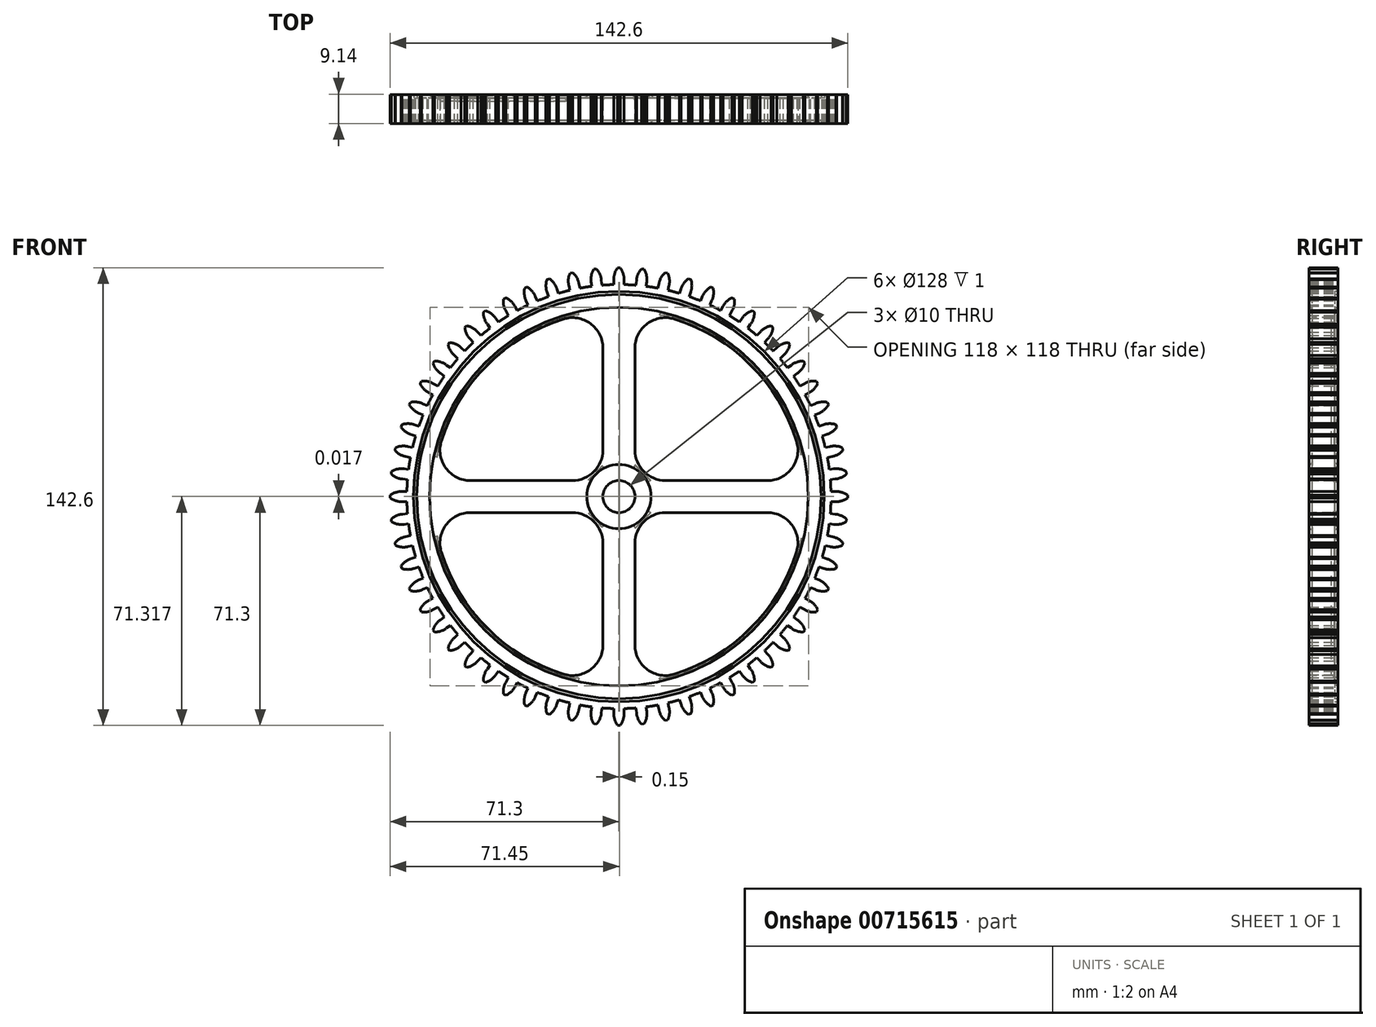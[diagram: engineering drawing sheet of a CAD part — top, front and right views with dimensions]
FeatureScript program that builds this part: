
annotation { "Feature Type Name" : "Feature", "Feature Type Description" : "" }
export const myFeature = defineFeature(function(context is Context, id is Id, definition is map)
    precondition{}
    {
        {
            var Q0;
            Q0=qCreatedBy(makeId("Front.planeOp"),FACE);
            var sketch = newSketch(context, id + "F0", { "sketchPlane" : qUnion([Q0])});
            skCircle(sketch, "E0", {"center": v(0, 0) * mm, "radius": 5 * mm});
            skCircle(sketch, "E1", {"center": v(0, 0) * mm, "radius": 66.1 * mm});
            skLineSegment(sketch, "E2", {"start": v(0, -77.77) * mm, "end": v(0, 74.62) * mm, "construction": true});
            skLineSegment(sketch, "E3", {"start": v(1.6, 66.08) * mm, "end": v(1.6, 67.83) * mm});
            skLineSegment(sketch, "E4", {"start": v(-1.6, 67.83) * mm, "end": v(-1.6, 66.08) * mm});
            skArc(sketch, "E5", {"start": v(-0.4, 71.3) * mm, "mid": v(-1.31, 69.54) * mm, "end": v(-1.6, 67.58) * mm});
            skArc(sketch, "E6.trimOffspring", {"start": v(1.6, 67.58) * mm, "mid": v(1.31, 69.54) * mm, "end": v(0.4, 71.3) * mm});
            skLineSegment(sketch, "E7", {"start": v(-0.4, 71.3) * mm, "end": v(0.4, 71.3) * mm});
            skLineSegment(sketch, "E8.1.0", {"start": v(-7.86, 70.87) * mm, "end": v(-7.05, 70.95) * mm});
            skArc(sketch, "E8.1.1", {"start": v(-5.47, 67.38) * mm, "mid": v(-5.96, 69.3) * mm, "end": v(-7.05, 70.95) * mm});
            skArc(sketch, "E8.1.2", {"start": v(-7.86, 70.87) * mm, "mid": v(-8.58, 69.02) * mm, "end": v(-8.66, 67.05) * mm});
            skLineSegment(sketch, "E8.1.3", {"start": v(-8.68, 67.3) * mm, "end": v(-8.5, 65.55) * mm});
            skLineSegment(sketch, "E8.1.4", {"start": v(-5.32, 65.89) * mm, "end": v(-5.5, 67.63) * mm});
            skLineSegment(sketch, "E8.2.0", {"start": v(-15.22, 69.66) * mm, "end": v(-14.43, 69.83) * mm});
            skArc(sketch, "E8.2.1", {"start": v(-12.49, 66.44) * mm, "mid": v(-13.17, 68.3) * mm, "end": v(-14.43, 69.83) * mm});
            skArc(sketch, "E8.2.2", {"start": v(-15.22, 69.66) * mm, "mid": v(-15.74, 67.75) * mm, "end": v(-15.62, 65.77) * mm});
            skLineSegment(sketch, "E8.2.3", {"start": v(-15.67, 66.02) * mm, "end": v(-15.3, 64.3) * mm});
            skLineSegment(sketch, "E8.2.4", {"start": v(-12.17, 64.97) * mm, "end": v(-12.54, 66.68) * mm});
            skLineSegment(sketch, "E9.1.3.0", {"start": v(-22.42, 67.68) * mm, "end": v(-21.64, 67.94) * mm});
            skArc(sketch, "E9.3.3.0", {"start": v(-19.36, 64.77) * mm, "mid": v(-20.24, 66.54) * mm, "end": v(-21.64, 67.94) * mm});
            skArc(sketch, "E9.7.3.0", {"start": v(-22.42, 67.68) * mm, "mid": v(-22.74, 65.73) * mm, "end": v(-22.4, 63.78) * mm});
            skLineSegment(sketch, "E9.11.3.0", {"start": v(-22.48, 64.02) * mm, "end": v(-21.94, 62.35) * mm});
            skLineSegment(sketch, "E9.14.3.0", {"start": v(-18.9, 63.34) * mm, "end": v(-19.44, 65) * mm});
            skLineSegment(sketch, "E9.1.4.0", {"start": v(-29.37, 64.97) * mm, "end": v(-28.63, 65.3) * mm});
            skArc(sketch, "E9.3.4.0", {"start": v(-26.03, 62.4) * mm, "mid": v(-27.08, 64.06) * mm, "end": v(-28.63, 65.3) * mm});
            skArc(sketch, "E9.7.4.0", {"start": v(-29.37, 64.97) * mm, "mid": v(-29.49, 63) * mm, "end": v(-28.95, 61.09) * mm});
            skLineSegment(sketch, "E9.11.4.0", {"start": v(-29.05, 61.32) * mm, "end": v(-28.34, 59.72) * mm});
            skLineSegment(sketch, "E9.14.4.0", {"start": v(-25.42, 61.02) * mm, "end": v(-26.13, 62.62) * mm});
            skLineSegment(sketch, "E9.1.5.0", {"start": v(-36, 61.54) * mm, "end": v(-35.3, 61.95) * mm});
            skArc(sketch, "E9.3.5.0", {"start": v(-32.4, 59.33) * mm, "mid": v(-33.63, 60.88) * mm, "end": v(-35.3, 61.95) * mm});
            skArc(sketch, "E9.7.5.0", {"start": v(-36, 61.54) * mm, "mid": v(-35.9, 59.57) * mm, "end": v(-35.18, 57.73) * mm});
            skLineSegment(sketch, "E9.11.5.0", {"start": v(-35.3, 57.94) * mm, "end": v(-34.43, 56.43) * mm});
            skLineSegment(sketch, "E9.14.5.0", {"start": v(-31.65, 58.03) * mm, "end": v(-32.53, 59.54) * mm});
            skLineSegment(sketch, "E9.1.6.0", {"start": v(-42.24, 57.44) * mm, "end": v(-41.58, 57.92) * mm});
            skArc(sketch, "E9.3.6.0", {"start": v(-38.43, 55.62) * mm, "mid": v(-39.81, 57.03) * mm, "end": v(-41.58, 57.92) * mm});
            skArc(sketch, "E9.7.6.0", {"start": v(-42.24, 57.44) * mm, "mid": v(-41.94, 55.49) * mm, "end": v(-41.02, 53.74) * mm});
            skLineSegment(sketch, "E9.11.6.0", {"start": v(-41.16, 53.94) * mm, "end": v(-40.14, 52.52) * mm});
            skLineSegment(sketch, "E9.14.6.0", {"start": v(-37.55, 54.4) * mm, "end": v(-38.58, 55.82) * mm});
            skLineSegment(sketch, "E9.1.7.0", {"start": v(-48.01, 52.71) * mm, "end": v(-47.4, 53.26) * mm});
            skArc(sketch, "E9.3.7.0", {"start": v(-44.03, 51.3) * mm, "mid": v(-45.56, 52.56) * mm, "end": v(-47.4, 53.26) * mm});
            skArc(sketch, "E9.7.7.0", {"start": v(-48.01, 52.71) * mm, "mid": v(-47.5, 50.8) * mm, "end": v(-46.41, 49.15) * mm});
            skLineSegment(sketch, "E9.11.7.0", {"start": v(-46.58, 49.34) * mm, "end": v(-45.4, 48.04) * mm});
            skLineSegment(sketch, "E9.14.7.0", {"start": v(-43.03, 50.18) * mm, "end": v(-44.2, 51.48) * mm});
            skLineSegment(sketch, "E9.1.8.0", {"start": v(-53.26, 47.4) * mm, "end": v(-52.71, 48.01) * mm});
            skArc(sketch, "E9.3.8.0", {"start": v(-49.15, 46.41) * mm, "mid": v(-50.8, 47.5) * mm, "end": v(-52.71, 48.01) * mm});
            skArc(sketch, "E9.7.8.0", {"start": v(-53.26, 47.4) * mm, "mid": v(-52.56, 45.56) * mm, "end": v(-51.3, 44.03) * mm});
            skLineSegment(sketch, "E9.11.8.0", {"start": v(-51.48, 44.2) * mm, "end": v(-50.18, 43.03) * mm});
            skLineSegment(sketch, "E9.14.8.0", {"start": v(-48.04, 45.4) * mm, "end": v(-49.34, 46.58) * mm});
            skLineSegment(sketch, "E9.1.9.0", {"start": v(-57.92, 41.58) * mm, "end": v(-57.44, 42.24) * mm});
            skArc(sketch, "E9.3.9.0", {"start": v(-53.74, 41.02) * mm, "mid": v(-55.49, 41.94) * mm, "end": v(-57.44, 42.24) * mm});
            skArc(sketch, "E9.7.9.0", {"start": v(-57.92, 41.58) * mm, "mid": v(-57.03, 39.81) * mm, "end": v(-55.62, 38.43) * mm});
            skLineSegment(sketch, "E9.11.9.0", {"start": v(-55.82, 38.58) * mm, "end": v(-54.4, 37.55) * mm});
            skLineSegment(sketch, "E9.14.9.0", {"start": v(-52.52, 40.14) * mm, "end": v(-53.94, 41.16) * mm});
            skLineSegment(sketch, "E9.1.10.0", {"start": v(-61.95, 35.3) * mm, "end": v(-61.54, 36) * mm});
            skArc(sketch, "E9.3.10.0", {"start": v(-57.73, 35.18) * mm, "mid": v(-59.57, 35.9) * mm, "end": v(-61.54, 36) * mm});
            skArc(sketch, "E9.7.10.0", {"start": v(-61.95, 35.3) * mm, "mid": v(-60.88, 33.63) * mm, "end": v(-59.33, 32.4) * mm});
            skLineSegment(sketch, "E9.11.10.0", {"start": v(-59.54, 32.53) * mm, "end": v(-58.03, 31.65) * mm});
            skLineSegment(sketch, "E9.14.10.0", {"start": v(-56.43, 34.43) * mm, "end": v(-57.94, 35.3) * mm});
            skLineSegment(sketch, "E9.1.11.0", {"start": v(-65.3, 28.63) * mm, "end": v(-64.97, 29.37) * mm});
            skArc(sketch, "E9.3.11.0", {"start": v(-61.09, 28.95) * mm, "mid": v(-63, 29.49) * mm, "end": v(-64.97, 29.37) * mm});
            skArc(sketch, "E9.7.11.0", {"start": v(-65.3, 28.63) * mm, "mid": v(-64.06, 27.08) * mm, "end": v(-62.4, 26.03) * mm});
            skLineSegment(sketch, "E9.11.11.0", {"start": v(-62.62, 26.13) * mm, "end": v(-61.02, 25.42) * mm});
            skLineSegment(sketch, "E9.14.11.0", {"start": v(-59.72, 28.34) * mm, "end": v(-61.32, 29.05) * mm});
            skLineSegment(sketch, "E9.1.12.0", {"start": v(-67.94, 21.64) * mm, "end": v(-67.68, 22.42) * mm});
            skArc(sketch, "E9.3.12.0", {"start": v(-63.78, 22.4) * mm, "mid": v(-65.73, 22.74) * mm, "end": v(-67.68, 22.42) * mm});
            skArc(sketch, "E9.7.12.0", {"start": v(-67.94, 21.64) * mm, "mid": v(-66.54, 20.24) * mm, "end": v(-64.77, 19.36) * mm});
            skLineSegment(sketch, "E9.11.12.0", {"start": v(-65, 19.44) * mm, "end": v(-63.34, 18.9) * mm});
            skLineSegment(sketch, "E9.14.12.0", {"start": v(-62.35, 21.94) * mm, "end": v(-64.02, 22.48) * mm});
            skLineSegment(sketch, "E9.1.13.0", {"start": v(-69.83, 14.43) * mm, "end": v(-69.66, 15.22) * mm});
            skArc(sketch, "E9.3.13.0", {"start": v(-65.77, 15.62) * mm, "mid": v(-67.75, 15.74) * mm, "end": v(-69.66, 15.22) * mm});
            skArc(sketch, "E9.7.13.0", {"start": v(-69.83, 14.43) * mm, "mid": v(-68.3, 13.17) * mm, "end": v(-66.44, 12.49) * mm});
            skLineSegment(sketch, "E9.11.13.0", {"start": v(-66.68, 12.54) * mm, "end": v(-64.97, 12.17) * mm});
            skLineSegment(sketch, "E9.14.13.0", {"start": v(-64.3, 15.3) * mm, "end": v(-66.02, 15.67) * mm});
            skLineSegment(sketch, "E9.1.14.0", {"start": v(-70.95, 7.05) * mm, "end": v(-70.87, 7.86) * mm});
            skArc(sketch, "E9.3.14.0", {"start": v(-67.05, 8.66) * mm, "mid": v(-69.02, 8.58) * mm, "end": v(-70.87, 7.86) * mm});
            skArc(sketch, "E9.7.14.0", {"start": v(-70.95, 7.05) * mm, "mid": v(-69.3, 5.96) * mm, "end": v(-67.38, 5.47) * mm});
            skLineSegment(sketch, "E9.11.14.0", {"start": v(-67.63, 5.5) * mm, "end": v(-65.89, 5.32) * mm});
            skLineSegment(sketch, "E9.14.14.0", {"start": v(-65.55, 8.5) * mm, "end": v(-67.3, 8.68) * mm});
            skLineSegment(sketch, "E9.1.15.0", {"start": v(-71.3, -0.4) * mm, "end": v(-71.3, 0.4) * mm});
            skArc(sketch, "E9.3.15.0", {"start": v(-67.58, 1.6) * mm, "mid": v(-69.54, 1.31) * mm, "end": v(-71.3, 0.4) * mm});
            skArc(sketch, "E9.7.15.0", {"start": v(-71.3, -0.4) * mm, "mid": v(-69.54, -1.31) * mm, "end": v(-67.58, -1.6) * mm});
            skLineSegment(sketch, "E9.11.15.0", {"start": v(-67.83, -1.6) * mm, "end": v(-66.08, -1.6) * mm});
            skLineSegment(sketch, "E9.14.15.0", {"start": v(-66.08, 1.6) * mm, "end": v(-67.83, 1.6) * mm});
            skLineSegment(sketch, "E9.1.16.0", {"start": v(-70.87, -7.86) * mm, "end": v(-70.95, -7.05) * mm});
            skArc(sketch, "E9.3.16.0", {"start": v(-67.38, -5.47) * mm, "mid": v(-69.3, -5.96) * mm, "end": v(-70.95, -7.05) * mm});
            skArc(sketch, "E9.7.16.0", {"start": v(-70.87, -7.86) * mm, "mid": v(-69.02, -8.58) * mm, "end": v(-67.05, -8.66) * mm});
            skLineSegment(sketch, "E9.11.16.0", {"start": v(-67.3, -8.68) * mm, "end": v(-65.55, -8.5) * mm});
            skLineSegment(sketch, "E9.14.16.0", {"start": v(-65.89, -5.32) * mm, "end": v(-67.63, -5.5) * mm});
            skLineSegment(sketch, "E9.1.17.0", {"start": v(-69.66, -15.22) * mm, "end": v(-69.83, -14.43) * mm});
            skArc(sketch, "E9.3.17.0", {"start": v(-66.44, -12.49) * mm, "mid": v(-68.3, -13.17) * mm, "end": v(-69.83, -14.43) * mm});
            skArc(sketch, "E9.7.17.0", {"start": v(-69.66, -15.22) * mm, "mid": v(-67.75, -15.74) * mm, "end": v(-65.77, -15.62) * mm});
            skLineSegment(sketch, "E9.11.17.0", {"start": v(-66.02, -15.67) * mm, "end": v(-64.3, -15.3) * mm});
            skLineSegment(sketch, "E9.14.17.0", {"start": v(-64.97, -12.17) * mm, "end": v(-66.68, -12.54) * mm});
            skLineSegment(sketch, "E9.1.18.0", {"start": v(-67.68, -22.42) * mm, "end": v(-67.94, -21.64) * mm});
            skArc(sketch, "E9.3.18.0", {"start": v(-64.77, -19.36) * mm, "mid": v(-66.54, -20.24) * mm, "end": v(-67.94, -21.64) * mm});
            skArc(sketch, "E9.7.18.0", {"start": v(-67.68, -22.42) * mm, "mid": v(-65.73, -22.74) * mm, "end": v(-63.78, -22.4) * mm});
            skLineSegment(sketch, "E9.11.18.0", {"start": v(-64.02, -22.48) * mm, "end": v(-62.35, -21.94) * mm});
            skLineSegment(sketch, "E9.14.18.0", {"start": v(-63.34, -18.9) * mm, "end": v(-65, -19.44) * mm});
            skLineSegment(sketch, "E9.1.19.0", {"start": v(-64.97, -29.37) * mm, "end": v(-65.3, -28.63) * mm});
            skArc(sketch, "E9.3.19.0", {"start": v(-62.4, -26.03) * mm, "mid": v(-64.06, -27.08) * mm, "end": v(-65.3, -28.63) * mm});
            skArc(sketch, "E9.7.19.0", {"start": v(-64.97, -29.37) * mm, "mid": v(-63, -29.49) * mm, "end": v(-61.09, -28.95) * mm});
            skLineSegment(sketch, "E9.11.19.0", {"start": v(-61.32, -29.05) * mm, "end": v(-59.72, -28.34) * mm});
            skLineSegment(sketch, "E9.14.19.0", {"start": v(-61.02, -25.42) * mm, "end": v(-62.62, -26.13) * mm});
            skLineSegment(sketch, "E9.1.20.0", {"start": v(-61.54, -36) * mm, "end": v(-61.95, -35.3) * mm});
            skArc(sketch, "E9.3.20.0", {"start": v(-59.33, -32.4) * mm, "mid": v(-60.88, -33.63) * mm, "end": v(-61.95, -35.3) * mm});
            skArc(sketch, "E9.7.20.0", {"start": v(-61.54, -36) * mm, "mid": v(-59.57, -35.9) * mm, "end": v(-57.73, -35.18) * mm});
            skLineSegment(sketch, "E9.11.20.0", {"start": v(-57.94, -35.3) * mm, "end": v(-56.43, -34.43) * mm});
            skLineSegment(sketch, "E9.14.20.0", {"start": v(-58.03, -31.65) * mm, "end": v(-59.54, -32.53) * mm});
            skLineSegment(sketch, "E9.1.21.0", {"start": v(-57.44, -42.24) * mm, "end": v(-57.92, -41.58) * mm});
            skArc(sketch, "E9.3.21.0", {"start": v(-55.62, -38.43) * mm, "mid": v(-57.03, -39.81) * mm, "end": v(-57.92, -41.58) * mm});
            skArc(sketch, "E9.7.21.0", {"start": v(-57.44, -42.24) * mm, "mid": v(-55.49, -41.94) * mm, "end": v(-53.74, -41.02) * mm});
            skLineSegment(sketch, "E9.11.21.0", {"start": v(-53.94, -41.16) * mm, "end": v(-52.52, -40.14) * mm});
            skLineSegment(sketch, "E9.14.21.0", {"start": v(-54.4, -37.55) * mm, "end": v(-55.82, -38.58) * mm});
            skLineSegment(sketch, "E9.1.22.0", {"start": v(-52.71, -48.01) * mm, "end": v(-53.26, -47.4) * mm});
            skArc(sketch, "E9.3.22.0", {"start": v(-51.3, -44.03) * mm, "mid": v(-52.56, -45.56) * mm, "end": v(-53.26, -47.4) * mm});
            skArc(sketch, "E9.7.22.0", {"start": v(-52.71, -48.01) * mm, "mid": v(-50.8, -47.5) * mm, "end": v(-49.15, -46.41) * mm});
            skLineSegment(sketch, "E9.11.22.0", {"start": v(-49.34, -46.58) * mm, "end": v(-48.04, -45.4) * mm});
            skLineSegment(sketch, "E9.14.22.0", {"start": v(-50.18, -43.03) * mm, "end": v(-51.48, -44.2) * mm});
            skLineSegment(sketch, "E9.1.23.0", {"start": v(-47.4, -53.26) * mm, "end": v(-48.01, -52.71) * mm});
            skArc(sketch, "E9.3.23.0", {"start": v(-46.41, -49.15) * mm, "mid": v(-47.5, -50.8) * mm, "end": v(-48.01, -52.71) * mm});
            skArc(sketch, "E9.7.23.0", {"start": v(-47.4, -53.26) * mm, "mid": v(-45.56, -52.56) * mm, "end": v(-44.03, -51.3) * mm});
            skLineSegment(sketch, "E9.11.23.0", {"start": v(-44.2, -51.48) * mm, "end": v(-43.03, -50.18) * mm});
            skLineSegment(sketch, "E9.14.23.0", {"start": v(-45.4, -48.04) * mm, "end": v(-46.58, -49.34) * mm});
            skLineSegment(sketch, "E9.1.24.0", {"start": v(-41.58, -57.92) * mm, "end": v(-42.24, -57.44) * mm});
            skArc(sketch, "E9.3.24.0", {"start": v(-41.02, -53.74) * mm, "mid": v(-41.94, -55.49) * mm, "end": v(-42.24, -57.44) * mm});
            skArc(sketch, "E9.7.24.0", {"start": v(-41.58, -57.92) * mm, "mid": v(-39.81, -57.03) * mm, "end": v(-38.43, -55.62) * mm});
            skLineSegment(sketch, "E9.11.24.0", {"start": v(-38.58, -55.82) * mm, "end": v(-37.55, -54.4) * mm});
            skLineSegment(sketch, "E9.14.24.0", {"start": v(-40.14, -52.52) * mm, "end": v(-41.16, -53.94) * mm});
            skLineSegment(sketch, "E9.1.25.0", {"start": v(-35.3, -61.95) * mm, "end": v(-36, -61.54) * mm});
            skArc(sketch, "E9.3.25.0", {"start": v(-35.18, -57.73) * mm, "mid": v(-35.9, -59.57) * mm, "end": v(-36, -61.54) * mm});
            skArc(sketch, "E9.7.25.0", {"start": v(-35.3, -61.95) * mm, "mid": v(-33.63, -60.88) * mm, "end": v(-32.4, -59.33) * mm});
            skLineSegment(sketch, "E9.11.25.0", {"start": v(-32.53, -59.54) * mm, "end": v(-31.65, -58.03) * mm});
            skLineSegment(sketch, "E9.14.25.0", {"start": v(-34.43, -56.43) * mm, "end": v(-35.3, -57.94) * mm});
            skLineSegment(sketch, "E9.1.26.0", {"start": v(-28.63, -65.3) * mm, "end": v(-29.37, -64.97) * mm});
            skArc(sketch, "E9.3.26.0", {"start": v(-28.95, -61.09) * mm, "mid": v(-29.49, -63) * mm, "end": v(-29.37, -64.97) * mm});
            skArc(sketch, "E9.7.26.0", {"start": v(-28.63, -65.3) * mm, "mid": v(-27.08, -64.06) * mm, "end": v(-26.03, -62.4) * mm});
            skLineSegment(sketch, "E9.11.26.0", {"start": v(-26.13, -62.62) * mm, "end": v(-25.42, -61.02) * mm});
            skLineSegment(sketch, "E9.14.26.0", {"start": v(-28.34, -59.72) * mm, "end": v(-29.05, -61.32) * mm});
            skLineSegment(sketch, "E9.1.27.0", {"start": v(-21.64, -67.94) * mm, "end": v(-22.42, -67.68) * mm});
            skArc(sketch, "E9.3.27.0", {"start": v(-22.4, -63.78) * mm, "mid": v(-22.74, -65.73) * mm, "end": v(-22.42, -67.68) * mm});
            skArc(sketch, "E9.7.27.0", {"start": v(-21.64, -67.94) * mm, "mid": v(-20.24, -66.54) * mm, "end": v(-19.36, -64.77) * mm});
            skLineSegment(sketch, "E9.11.27.0", {"start": v(-19.44, -65) * mm, "end": v(-18.9, -63.34) * mm});
            skLineSegment(sketch, "E9.14.27.0", {"start": v(-21.94, -62.35) * mm, "end": v(-22.48, -64.02) * mm});
            skLineSegment(sketch, "E9.1.28.0", {"start": v(-14.43, -69.83) * mm, "end": v(-15.22, -69.66) * mm});
            skArc(sketch, "E9.3.28.0", {"start": v(-15.62, -65.77) * mm, "mid": v(-15.74, -67.75) * mm, "end": v(-15.22, -69.66) * mm});
            skArc(sketch, "E9.7.28.0", {"start": v(-14.43, -69.83) * mm, "mid": v(-13.17, -68.3) * mm, "end": v(-12.49, -66.44) * mm});
            skLineSegment(sketch, "E9.11.28.0", {"start": v(-12.54, -66.68) * mm, "end": v(-12.17, -64.97) * mm});
            skLineSegment(sketch, "E9.14.28.0", {"start": v(-15.3, -64.3) * mm, "end": v(-15.67, -66.02) * mm});
            skLineSegment(sketch, "E9.1.29.0", {"start": v(-7.05, -70.95) * mm, "end": v(-7.86, -70.87) * mm});
            skArc(sketch, "E9.3.29.0", {"start": v(-8.66, -67.05) * mm, "mid": v(-8.58, -69.02) * mm, "end": v(-7.86, -70.87) * mm});
            skArc(sketch, "E9.7.29.0", {"start": v(-7.05, -70.95) * mm, "mid": v(-5.96, -69.3) * mm, "end": v(-5.47, -67.38) * mm});
            skLineSegment(sketch, "E9.11.29.0", {"start": v(-5.5, -67.63) * mm, "end": v(-5.32, -65.89) * mm});
            skLineSegment(sketch, "E9.14.29.0", {"start": v(-8.5, -65.55) * mm, "end": v(-8.68, -67.3) * mm});
            skLineSegment(sketch, "E9.1.30.0", {"start": v(0.4, -71.3) * mm, "end": v(-0.4, -71.3) * mm});
            skArc(sketch, "E9.3.30.0", {"start": v(-1.6, -67.58) * mm, "mid": v(-1.31, -69.54) * mm, "end": v(-0.4, -71.3) * mm});
            skArc(sketch, "E9.7.30.0", {"start": v(0.4, -71.3) * mm, "mid": v(1.31, -69.54) * mm, "end": v(1.6, -67.58) * mm});
            skLineSegment(sketch, "E9.11.30.0", {"start": v(1.6, -67.83) * mm, "end": v(1.6, -66.08) * mm});
            skLineSegment(sketch, "E9.14.30.0", {"start": v(-1.6, -66.08) * mm, "end": v(-1.6, -67.83) * mm});
            skLineSegment(sketch, "E9.1.31.0", {"start": v(7.86, -70.87) * mm, "end": v(7.05, -70.95) * mm});
            skArc(sketch, "E9.3.31.0", {"start": v(5.47, -67.38) * mm, "mid": v(5.96, -69.3) * mm, "end": v(7.05, -70.95) * mm});
            skArc(sketch, "E9.7.31.0", {"start": v(7.86, -70.87) * mm, "mid": v(8.58, -69.02) * mm, "end": v(8.66, -67.05) * mm});
            skLineSegment(sketch, "E9.11.31.0", {"start": v(8.68, -67.3) * mm, "end": v(8.5, -65.55) * mm});
            skLineSegment(sketch, "E9.14.31.0", {"start": v(5.32, -65.89) * mm, "end": v(5.5, -67.63) * mm});
            skLineSegment(sketch, "E9.1.32.0", {"start": v(15.22, -69.66) * mm, "end": v(14.43, -69.83) * mm});
            skArc(sketch, "E9.3.32.0", {"start": v(12.49, -66.44) * mm, "mid": v(13.17, -68.3) * mm, "end": v(14.43, -69.83) * mm});
            skArc(sketch, "E9.7.32.0", {"start": v(15.22, -69.66) * mm, "mid": v(15.74, -67.75) * mm, "end": v(15.62, -65.77) * mm});
            skLineSegment(sketch, "E9.11.32.0", {"start": v(15.67, -66.02) * mm, "end": v(15.3, -64.3) * mm});
            skLineSegment(sketch, "E9.14.32.0", {"start": v(12.17, -64.97) * mm, "end": v(12.54, -66.68) * mm});
            skLineSegment(sketch, "E9.1.33.0", {"start": v(22.42, -67.68) * mm, "end": v(21.64, -67.94) * mm});
            skArc(sketch, "E9.3.33.0", {"start": v(19.36, -64.77) * mm, "mid": v(20.24, -66.54) * mm, "end": v(21.64, -67.94) * mm});
            skArc(sketch, "E9.7.33.0", {"start": v(22.42, -67.68) * mm, "mid": v(22.74, -65.73) * mm, "end": v(22.4, -63.78) * mm});
            skLineSegment(sketch, "E9.11.33.0", {"start": v(22.48, -64.02) * mm, "end": v(21.94, -62.35) * mm});
            skLineSegment(sketch, "E9.14.33.0", {"start": v(18.9, -63.34) * mm, "end": v(19.44, -65) * mm});
            skLineSegment(sketch, "E9.1.34.0", {"start": v(29.37, -64.97) * mm, "end": v(28.63, -65.3) * mm});
            skArc(sketch, "E9.3.34.0", {"start": v(26.03, -62.4) * mm, "mid": v(27.08, -64.06) * mm, "end": v(28.63, -65.3) * mm});
            skArc(sketch, "E9.7.34.0", {"start": v(29.37, -64.97) * mm, "mid": v(29.49, -63) * mm, "end": v(28.95, -61.09) * mm});
            skLineSegment(sketch, "E9.11.34.0", {"start": v(29.05, -61.32) * mm, "end": v(28.34, -59.72) * mm});
            skLineSegment(sketch, "E9.14.34.0", {"start": v(25.42, -61.02) * mm, "end": v(26.13, -62.62) * mm});
            skLineSegment(sketch, "E9.1.35.0", {"start": v(36, -61.54) * mm, "end": v(35.3, -61.95) * mm});
            skArc(sketch, "E9.3.35.0", {"start": v(32.4, -59.33) * mm, "mid": v(33.63, -60.88) * mm, "end": v(35.3, -61.95) * mm});
            skArc(sketch, "E9.7.35.0", {"start": v(36, -61.54) * mm, "mid": v(35.9, -59.57) * mm, "end": v(35.18, -57.73) * mm});
            skLineSegment(sketch, "E9.11.35.0", {"start": v(35.3, -57.94) * mm, "end": v(34.43, -56.43) * mm});
            skLineSegment(sketch, "E9.14.35.0", {"start": v(31.65, -58.03) * mm, "end": v(32.53, -59.54) * mm});
            skLineSegment(sketch, "E9.1.36.0", {"start": v(42.24, -57.44) * mm, "end": v(41.58, -57.92) * mm});
            skArc(sketch, "E9.3.36.0", {"start": v(38.43, -55.62) * mm, "mid": v(39.81, -57.03) * mm, "end": v(41.58, -57.92) * mm});
            skArc(sketch, "E9.7.36.0", {"start": v(42.24, -57.44) * mm, "mid": v(41.94, -55.49) * mm, "end": v(41.02, -53.74) * mm});
            skLineSegment(sketch, "E9.11.36.0", {"start": v(41.16, -53.94) * mm, "end": v(40.14, -52.52) * mm});
            skLineSegment(sketch, "E9.14.36.0", {"start": v(37.55, -54.4) * mm, "end": v(38.58, -55.82) * mm});
            skLineSegment(sketch, "E9.1.37.0", {"start": v(48.01, -52.71) * mm, "end": v(47.4, -53.26) * mm});
            skArc(sketch, "E9.3.37.0", {"start": v(44.03, -51.3) * mm, "mid": v(45.56, -52.56) * mm, "end": v(47.4, -53.26) * mm});
            skArc(sketch, "E9.7.37.0", {"start": v(48.01, -52.71) * mm, "mid": v(47.5, -50.8) * mm, "end": v(46.41, -49.15) * mm});
            skLineSegment(sketch, "E9.11.37.0", {"start": v(46.58, -49.34) * mm, "end": v(45.4, -48.04) * mm});
            skLineSegment(sketch, "E9.14.37.0", {"start": v(43.03, -50.18) * mm, "end": v(44.2, -51.48) * mm});
            skLineSegment(sketch, "E9.1.38.0", {"start": v(53.26, -47.4) * mm, "end": v(52.71, -48.01) * mm});
            skArc(sketch, "E9.3.38.0", {"start": v(49.15, -46.41) * mm, "mid": v(50.8, -47.5) * mm, "end": v(52.71, -48.01) * mm});
            skArc(sketch, "E9.7.38.0", {"start": v(53.26, -47.4) * mm, "mid": v(52.56, -45.56) * mm, "end": v(51.3, -44.03) * mm});
            skLineSegment(sketch, "E9.11.38.0", {"start": v(51.48, -44.2) * mm, "end": v(50.18, -43.03) * mm});
            skLineSegment(sketch, "E9.14.38.0", {"start": v(48.04, -45.4) * mm, "end": v(49.34, -46.58) * mm});
            skLineSegment(sketch, "E9.1.39.0", {"start": v(57.92, -41.58) * mm, "end": v(57.44, -42.24) * mm});
            skArc(sketch, "E9.3.39.0", {"start": v(53.74, -41.02) * mm, "mid": v(55.49, -41.94) * mm, "end": v(57.44, -42.24) * mm});
            skArc(sketch, "E9.7.39.0", {"start": v(57.92, -41.58) * mm, "mid": v(57.03, -39.81) * mm, "end": v(55.62, -38.43) * mm});
            skLineSegment(sketch, "E9.11.39.0", {"start": v(55.82, -38.58) * mm, "end": v(54.4, -37.55) * mm});
            skLineSegment(sketch, "E9.14.39.0", {"start": v(52.52, -40.14) * mm, "end": v(53.94, -41.16) * mm});
            skLineSegment(sketch, "E9.1.40.0", {"start": v(61.95, -35.3) * mm, "end": v(61.54, -36) * mm});
            skArc(sketch, "E9.3.40.0", {"start": v(57.73, -35.18) * mm, "mid": v(59.57, -35.9) * mm, "end": v(61.54, -36) * mm});
            skArc(sketch, "E9.7.40.0", {"start": v(61.95, -35.3) * mm, "mid": v(60.88, -33.63) * mm, "end": v(59.33, -32.4) * mm});
            skLineSegment(sketch, "E9.11.40.0", {"start": v(59.54, -32.53) * mm, "end": v(58.03, -31.65) * mm});
            skLineSegment(sketch, "E9.14.40.0", {"start": v(56.43, -34.43) * mm, "end": v(57.94, -35.3) * mm});
            skLineSegment(sketch, "E9.1.41.0", {"start": v(65.3, -28.63) * mm, "end": v(64.97, -29.37) * mm});
            skArc(sketch, "E9.3.41.0", {"start": v(61.09, -28.95) * mm, "mid": v(63, -29.49) * mm, "end": v(64.97, -29.37) * mm});
            skArc(sketch, "E9.7.41.0", {"start": v(65.3, -28.63) * mm, "mid": v(64.06, -27.08) * mm, "end": v(62.4, -26.03) * mm});
            skLineSegment(sketch, "E9.11.41.0", {"start": v(62.62, -26.13) * mm, "end": v(61.02, -25.42) * mm});
            skLineSegment(sketch, "E9.14.41.0", {"start": v(59.72, -28.34) * mm, "end": v(61.32, -29.05) * mm});
            skLineSegment(sketch, "E9.1.42.0", {"start": v(67.94, -21.64) * mm, "end": v(67.68, -22.42) * mm});
            skArc(sketch, "E9.3.42.0", {"start": v(63.78, -22.4) * mm, "mid": v(65.73, -22.74) * mm, "end": v(67.68, -22.42) * mm});
            skArc(sketch, "E9.7.42.0", {"start": v(67.94, -21.64) * mm, "mid": v(66.54, -20.24) * mm, "end": v(64.77, -19.36) * mm});
            skLineSegment(sketch, "E9.11.42.0", {"start": v(65, -19.44) * mm, "end": v(63.34, -18.9) * mm});
            skLineSegment(sketch, "E9.14.42.0", {"start": v(62.35, -21.94) * mm, "end": v(64.02, -22.48) * mm});
            skLineSegment(sketch, "E9.1.43.0", {"start": v(69.83, -14.43) * mm, "end": v(69.66, -15.22) * mm});
            skArc(sketch, "E9.3.43.0", {"start": v(65.77, -15.62) * mm, "mid": v(67.75, -15.74) * mm, "end": v(69.66, -15.22) * mm});
            skArc(sketch, "E9.7.43.0", {"start": v(69.83, -14.43) * mm, "mid": v(68.3, -13.17) * mm, "end": v(66.44, -12.49) * mm});
            skLineSegment(sketch, "E9.11.43.0", {"start": v(66.68, -12.54) * mm, "end": v(64.97, -12.17) * mm});
            skLineSegment(sketch, "E9.14.43.0", {"start": v(64.3, -15.3) * mm, "end": v(66.02, -15.67) * mm});
            skLineSegment(sketch, "E9.1.44.0", {"start": v(70.95, -7.05) * mm, "end": v(70.87, -7.86) * mm});
            skArc(sketch, "E9.3.44.0", {"start": v(67.05, -8.66) * mm, "mid": v(69.02, -8.58) * mm, "end": v(70.87, -7.86) * mm});
            skArc(sketch, "E9.7.44.0", {"start": v(70.95, -7.05) * mm, "mid": v(69.3, -5.96) * mm, "end": v(67.38, -5.47) * mm});
            skLineSegment(sketch, "E9.11.44.0", {"start": v(67.63, -5.5) * mm, "end": v(65.89, -5.32) * mm});
            skLineSegment(sketch, "E9.14.44.0", {"start": v(65.55, -8.5) * mm, "end": v(67.3, -8.68) * mm});
            skLineSegment(sketch, "E9.1.45.0", {"start": v(71.3, 0.4) * mm, "end": v(71.3, -0.4) * mm});
            skArc(sketch, "E9.3.45.0", {"start": v(67.58, -1.6) * mm, "mid": v(69.54, -1.31) * mm, "end": v(71.3, -0.4) * mm});
            skArc(sketch, "E9.7.45.0", {"start": v(71.3, 0.4) * mm, "mid": v(69.54, 1.31) * mm, "end": v(67.58, 1.6) * mm});
            skLineSegment(sketch, "E9.11.45.0", {"start": v(67.83, 1.6) * mm, "end": v(66.08, 1.6) * mm});
            skLineSegment(sketch, "E9.14.45.0", {"start": v(66.08, -1.6) * mm, "end": v(67.83, -1.6) * mm});
            skLineSegment(sketch, "E9.1.46.0", {"start": v(70.87, 7.86) * mm, "end": v(70.95, 7.05) * mm});
            skArc(sketch, "E9.3.46.0", {"start": v(67.38, 5.47) * mm, "mid": v(69.3, 5.96) * mm, "end": v(70.95, 7.05) * mm});
            skArc(sketch, "E9.7.46.0", {"start": v(70.87, 7.86) * mm, "mid": v(69.02, 8.58) * mm, "end": v(67.05, 8.66) * mm});
            skLineSegment(sketch, "E9.11.46.0", {"start": v(67.3, 8.68) * mm, "end": v(65.55, 8.5) * mm});
            skLineSegment(sketch, "E9.14.46.0", {"start": v(65.89, 5.32) * mm, "end": v(67.63, 5.5) * mm});
            skLineSegment(sketch, "E9.1.47.0", {"start": v(69.66, 15.22) * mm, "end": v(69.83, 14.43) * mm});
            skArc(sketch, "E9.3.47.0", {"start": v(66.44, 12.49) * mm, "mid": v(68.3, 13.17) * mm, "end": v(69.83, 14.43) * mm});
            skArc(sketch, "E9.7.47.0", {"start": v(69.66, 15.22) * mm, "mid": v(67.75, 15.74) * mm, "end": v(65.77, 15.62) * mm});
            skLineSegment(sketch, "E9.11.47.0", {"start": v(66.02, 15.67) * mm, "end": v(64.3, 15.3) * mm});
            skLineSegment(sketch, "E9.14.47.0", {"start": v(64.97, 12.17) * mm, "end": v(66.68, 12.54) * mm});
            skLineSegment(sketch, "E9.1.48.0", {"start": v(67.68, 22.42) * mm, "end": v(67.94, 21.64) * mm});
            skArc(sketch, "E9.3.48.0", {"start": v(64.77, 19.36) * mm, "mid": v(66.54, 20.24) * mm, "end": v(67.94, 21.64) * mm});
            skArc(sketch, "E9.7.48.0", {"start": v(67.68, 22.42) * mm, "mid": v(65.73, 22.74) * mm, "end": v(63.78, 22.4) * mm});
            skLineSegment(sketch, "E9.11.48.0", {"start": v(64.02, 22.48) * mm, "end": v(62.35, 21.94) * mm});
            skLineSegment(sketch, "E9.14.48.0", {"start": v(63.34, 18.9) * mm, "end": v(65, 19.44) * mm});
            skLineSegment(sketch, "E9.1.49.0", {"start": v(64.97, 29.37) * mm, "end": v(65.3, 28.63) * mm});
            skArc(sketch, "E9.3.49.0", {"start": v(62.4, 26.03) * mm, "mid": v(64.06, 27.08) * mm, "end": v(65.3, 28.63) * mm});
            skArc(sketch, "E9.7.49.0", {"start": v(64.97, 29.37) * mm, "mid": v(63, 29.49) * mm, "end": v(61.09, 28.95) * mm});
            skLineSegment(sketch, "E9.11.49.0", {"start": v(61.32, 29.05) * mm, "end": v(59.72, 28.34) * mm});
            skLineSegment(sketch, "E9.14.49.0", {"start": v(61.02, 25.42) * mm, "end": v(62.62, 26.13) * mm});
            skLineSegment(sketch, "E9.1.50.0", {"start": v(61.54, 36) * mm, "end": v(61.95, 35.3) * mm});
            skArc(sketch, "E9.3.50.0", {"start": v(59.33, 32.4) * mm, "mid": v(60.88, 33.63) * mm, "end": v(61.95, 35.3) * mm});
            skArc(sketch, "E9.7.50.0", {"start": v(61.54, 36) * mm, "mid": v(59.57, 35.9) * mm, "end": v(57.73, 35.18) * mm});
            skLineSegment(sketch, "E9.11.50.0", {"start": v(57.94, 35.3) * mm, "end": v(56.43, 34.43) * mm});
            skLineSegment(sketch, "E9.14.50.0", {"start": v(58.03, 31.65) * mm, "end": v(59.54, 32.53) * mm});
            skLineSegment(sketch, "E9.1.51.0", {"start": v(57.44, 42.24) * mm, "end": v(57.92, 41.58) * mm});
            skArc(sketch, "E9.3.51.0", {"start": v(55.62, 38.43) * mm, "mid": v(57.03, 39.81) * mm, "end": v(57.92, 41.58) * mm});
            skArc(sketch, "E9.7.51.0", {"start": v(57.44, 42.24) * mm, "mid": v(55.49, 41.94) * mm, "end": v(53.74, 41.02) * mm});
            skLineSegment(sketch, "E9.11.51.0", {"start": v(53.94, 41.16) * mm, "end": v(52.52, 40.14) * mm});
            skLineSegment(sketch, "E9.14.51.0", {"start": v(54.4, 37.55) * mm, "end": v(55.82, 38.58) * mm});
            skLineSegment(sketch, "E9.1.52.0", {"start": v(52.71, 48.01) * mm, "end": v(53.26, 47.4) * mm});
            skArc(sketch, "E9.3.52.0", {"start": v(51.3, 44.03) * mm, "mid": v(52.56, 45.56) * mm, "end": v(53.26, 47.4) * mm});
            skArc(sketch, "E9.7.52.0", {"start": v(52.71, 48.01) * mm, "mid": v(50.8, 47.5) * mm, "end": v(49.15, 46.41) * mm});
            skLineSegment(sketch, "E9.11.52.0", {"start": v(49.34, 46.58) * mm, "end": v(48.04, 45.4) * mm});
            skLineSegment(sketch, "E9.14.52.0", {"start": v(50.18, 43.03) * mm, "end": v(51.48, 44.2) * mm});
            skLineSegment(sketch, "E9.1.53.0", {"start": v(47.4, 53.26) * mm, "end": v(48.01, 52.71) * mm});
            skArc(sketch, "E9.3.53.0", {"start": v(46.41, 49.15) * mm, "mid": v(47.5, 50.8) * mm, "end": v(48.01, 52.71) * mm});
            skArc(sketch, "E9.7.53.0", {"start": v(47.4, 53.26) * mm, "mid": v(45.56, 52.56) * mm, "end": v(44.03, 51.3) * mm});
            skLineSegment(sketch, "E9.11.53.0", {"start": v(44.2, 51.48) * mm, "end": v(43.03, 50.18) * mm});
            skLineSegment(sketch, "E9.14.53.0", {"start": v(45.4, 48.04) * mm, "end": v(46.58, 49.34) * mm});
            skLineSegment(sketch, "E9.1.54.0", {"start": v(41.58, 57.92) * mm, "end": v(42.24, 57.44) * mm});
            skArc(sketch, "E9.3.54.0", {"start": v(41.02, 53.74) * mm, "mid": v(41.94, 55.49) * mm, "end": v(42.24, 57.44) * mm});
            skArc(sketch, "E9.7.54.0", {"start": v(41.58, 57.92) * mm, "mid": v(39.81, 57.03) * mm, "end": v(38.43, 55.62) * mm});
            skLineSegment(sketch, "E9.11.54.0", {"start": v(38.58, 55.82) * mm, "end": v(37.55, 54.4) * mm});
            skLineSegment(sketch, "E9.14.54.0", {"start": v(40.14, 52.52) * mm, "end": v(41.16, 53.94) * mm});
            skLineSegment(sketch, "E9.1.55.0", {"start": v(35.3, 61.95) * mm, "end": v(36, 61.54) * mm});
            skArc(sketch, "E9.3.55.0", {"start": v(35.18, 57.73) * mm, "mid": v(35.9, 59.57) * mm, "end": v(36, 61.54) * mm});
            skArc(sketch, "E9.7.55.0", {"start": v(35.3, 61.95) * mm, "mid": v(33.63, 60.88) * mm, "end": v(32.4, 59.33) * mm});
            skLineSegment(sketch, "E9.11.55.0", {"start": v(32.53, 59.54) * mm, "end": v(31.65, 58.03) * mm});
            skLineSegment(sketch, "E9.14.55.0", {"start": v(34.43, 56.43) * mm, "end": v(35.3, 57.94) * mm});
            skLineSegment(sketch, "E9.1.56.0", {"start": v(28.63, 65.3) * mm, "end": v(29.37, 64.97) * mm});
            skArc(sketch, "E9.3.56.0", {"start": v(28.95, 61.09) * mm, "mid": v(29.49, 63) * mm, "end": v(29.37, 64.97) * mm});
            skArc(sketch, "E9.7.56.0", {"start": v(28.63, 65.3) * mm, "mid": v(27.08, 64.06) * mm, "end": v(26.03, 62.4) * mm});
            skLineSegment(sketch, "E9.11.56.0", {"start": v(26.13, 62.62) * mm, "end": v(25.42, 61.02) * mm});
            skLineSegment(sketch, "E9.14.56.0", {"start": v(28.34, 59.72) * mm, "end": v(29.05, 61.32) * mm});
            skLineSegment(sketch, "E9.1.57.0", {"start": v(21.64, 67.94) * mm, "end": v(22.42, 67.68) * mm});
            skArc(sketch, "E9.3.57.0", {"start": v(22.4, 63.78) * mm, "mid": v(22.74, 65.73) * mm, "end": v(22.42, 67.68) * mm});
            skArc(sketch, "E9.7.57.0", {"start": v(21.64, 67.94) * mm, "mid": v(20.24, 66.54) * mm, "end": v(19.36, 64.77) * mm});
            skLineSegment(sketch, "E9.11.57.0", {"start": v(19.44, 65) * mm, "end": v(18.9, 63.34) * mm});
            skLineSegment(sketch, "E9.14.57.0", {"start": v(21.94, 62.35) * mm, "end": v(22.48, 64.02) * mm});
            skLineSegment(sketch, "E9.1.58.0", {"start": v(14.43, 69.83) * mm, "end": v(15.22, 69.66) * mm});
            skArc(sketch, "E9.3.58.0", {"start": v(15.62, 65.77) * mm, "mid": v(15.74, 67.75) * mm, "end": v(15.22, 69.66) * mm});
            skArc(sketch, "E9.7.58.0", {"start": v(14.43, 69.83) * mm, "mid": v(13.17, 68.3) * mm, "end": v(12.49, 66.44) * mm});
            skLineSegment(sketch, "E9.11.58.0", {"start": v(12.54, 66.68) * mm, "end": v(12.17, 64.97) * mm});
            skLineSegment(sketch, "E9.14.58.0", {"start": v(15.3, 64.3) * mm, "end": v(15.67, 66.02) * mm});
            skLineSegment(sketch, "E9.1.59.0", {"start": v(7.05, 70.95) * mm, "end": v(7.86, 70.87) * mm});
            skArc(sketch, "E9.3.59.0", {"start": v(8.66, 67.05) * mm, "mid": v(8.58, 69.02) * mm, "end": v(7.86, 70.87) * mm});
            skArc(sketch, "E9.7.59.0", {"start": v(7.05, 70.95) * mm, "mid": v(5.96, 69.3) * mm, "end": v(5.47, 67.38) * mm});
            skLineSegment(sketch, "E9.11.59.0", {"start": v(5.5, 67.63) * mm, "end": v(5.32, 65.89) * mm});
            skLineSegment(sketch, "E9.14.59.0", {"start": v(8.5, 65.55) * mm, "end": v(8.68, 67.3) * mm});
            skSolve(sketch);
        }
        {
            var Q0;
            Q0 = qSketchRegion(id + "F0", true);
            extrude(context, id + "F1", {"entities" : qUnion([Q0]), "depth" : 10 * mm, "offsetDistance" : 25 * mm});
        }
        {
            var Q0;
            Q0=makeQuery(id+"F1.opExtrude","CAP_FACE",FACE,{"disambiguationData":[OSD([sQuery(id+"F0.wireOp",EDGE,"E0"),sQuery(id+"F0.wireOp",EDGE,"E1"),sQuery(id+"F0.wireOp",EDGE,"E3"),sQuery(id+"F0.wireOp",EDGE,"E4"),sQuery(id+"F0.wireOp",EDGE,"E5"),sQuery(id+"F0.wireOp",EDGE,"E6.trimOffspring"),sQuery(id+"F0.wireOp",EDGE,"E7"),sQuery(id+"F0.wireOp",EDGE,"E8.1.0"),sQuery(id+"F0.wireOp",EDGE,"E8.1.1"),sQuery(id+"F0.wireOp",EDGE,"E8.1.2"),sQuery(id+"F0.wireOp",EDGE,"E8.1.3"),sQuery(id+"F0.wireOp",EDGE,"E8.1.4"),sQuery(id+"F0.wireOp",EDGE,"E8.2.0"),sQuery(id+"F0.wireOp",EDGE,"E8.2.1"),sQuery(id+"F0.wireOp",EDGE,"E8.2.2"),sQuery(id+"F0.wireOp",EDGE,"E8.2.3"),sQuery(id+"F0.wireOp",EDGE,"E8.2.4"),sQuery(id+"F0.wireOp",EDGE,"E9.1.3.0"),sQuery(id+"F0.wireOp",EDGE,"E9.3.3.0"),sQuery(id+"F0.wireOp",EDGE,"E9.7.3.0"),sQuery(id+"F0.wireOp",EDGE,"E9.11.3.0"),sQuery(id+"F0.wireOp",EDGE,"E9.14.3.0"),sQuery(id+"F0.wireOp",EDGE,"E9.1.4.0"),sQuery(id+"F0.wireOp",EDGE,"E9.3.4.0"),sQuery(id+"F0.wireOp",EDGE,"E9.7.4.0"),sQuery(id+"F0.wireOp",EDGE,"E9.11.4.0"),sQuery(id+"F0.wireOp",EDGE,"E9.14.4.0"),sQuery(id+"F0.wireOp",EDGE,"E9.1.5.0"),sQuery(id+"F0.wireOp",EDGE,"E9.3.5.0"),sQuery(id+"F0.wireOp",EDGE,"E9.7.5.0"),sQuery(id+"F0.wireOp",EDGE,"E9.11.5.0"),sQuery(id+"F0.wireOp",EDGE,"E9.14.5.0"),sQuery(id+"F0.wireOp",EDGE,"E9.1.6.0"),sQuery(id+"F0.wireOp",EDGE,"E9.3.6.0"),sQuery(id+"F0.wireOp",EDGE,"E9.7.6.0"),sQuery(id+"F0.wireOp",EDGE,"E9.11.6.0"),sQuery(id+"F0.wireOp",EDGE,"E9.14.6.0"),sQuery(id+"F0.wireOp",EDGE,"E9.1.7.0"),sQuery(id+"F0.wireOp",EDGE,"E9.3.7.0"),sQuery(id+"F0.wireOp",EDGE,"E9.7.7.0"),sQuery(id+"F0.wireOp",EDGE,"E9.11.7.0"),sQuery(id+"F0.wireOp",EDGE,"E9.14.7.0"),sQuery(id+"F0.wireOp",EDGE,"E9.1.8.0"),sQuery(id+"F0.wireOp",EDGE,"E9.3.8.0"),sQuery(id+"F0.wireOp",EDGE,"E9.7.8.0"),sQuery(id+"F0.wireOp",EDGE,"E9.11.8.0"),sQuery(id+"F0.wireOp",EDGE,"E9.14.8.0"),sQuery(id+"F0.wireOp",EDGE,"E9.1.9.0"),sQuery(id+"F0.wireOp",EDGE,"E9.3.9.0"),sQuery(id+"F0.wireOp",EDGE,"E9.7.9.0"),sQuery(id+"F0.wireOp",EDGE,"E9.11.9.0"),sQuery(id+"F0.wireOp",EDGE,"E9.14.9.0"),sQuery(id+"F0.wireOp",EDGE,"E9.1.10.0"),sQuery(id+"F0.wireOp",EDGE,"E9.3.10.0"),sQuery(id+"F0.wireOp",EDGE,"E9.7.10.0"),sQuery(id+"F0.wireOp",EDGE,"E9.11.10.0"),sQuery(id+"F0.wireOp",EDGE,"E9.14.10.0"),sQuery(id+"F0.wireOp",EDGE,"E9.1.11.0"),sQuery(id+"F0.wireOp",EDGE,"E9.3.11.0"),sQuery(id+"F0.wireOp",EDGE,"E9.7.11.0"),sQuery(id+"F0.wireOp",EDGE,"E9.11.11.0"),sQuery(id+"F0.wireOp",EDGE,"E9.14.11.0"),sQuery(id+"F0.wireOp",EDGE,"E9.1.12.0"),sQuery(id+"F0.wireOp",EDGE,"E9.3.12.0"),sQuery(id+"F0.wireOp",EDGE,"E9.7.12.0"),sQuery(id+"F0.wireOp",EDGE,"E9.11.12.0"),sQuery(id+"F0.wireOp",EDGE,"E9.14.12.0"),sQuery(id+"F0.wireOp",EDGE,"E9.1.13.0"),sQuery(id+"F0.wireOp",EDGE,"E9.3.13.0"),sQuery(id+"F0.wireOp",EDGE,"E9.7.13.0"),sQuery(id+"F0.wireOp",EDGE,"E9.11.13.0"),sQuery(id+"F0.wireOp",EDGE,"E9.14.13.0"),sQuery(id+"F0.wireOp",EDGE,"E9.1.14.0"),sQuery(id+"F0.wireOp",EDGE,"E9.3.14.0"),sQuery(id+"F0.wireOp",EDGE,"E9.7.14.0"),sQuery(id+"F0.wireOp",EDGE,"E9.11.14.0"),sQuery(id+"F0.wireOp",EDGE,"E9.14.14.0"),sQuery(id+"F0.wireOp",EDGE,"E9.1.15.0"),sQuery(id+"F0.wireOp",EDGE,"E9.3.15.0"),sQuery(id+"F0.wireOp",EDGE,"E9.7.15.0"),sQuery(id+"F0.wireOp",EDGE,"E9.11.15.0"),sQuery(id+"F0.wireOp",EDGE,"E9.14.15.0"),sQuery(id+"F0.wireOp",EDGE,"E9.1.16.0"),sQuery(id+"F0.wireOp",EDGE,"E9.3.16.0"),sQuery(id+"F0.wireOp",EDGE,"E9.7.16.0"),sQuery(id+"F0.wireOp",EDGE,"E9.11.16.0"),sQuery(id+"F0.wireOp",EDGE,"E9.14.16.0"),sQuery(id+"F0.wireOp",EDGE,"E9.1.17.0"),sQuery(id+"F0.wireOp",EDGE,"E9.3.17.0"),sQuery(id+"F0.wireOp",EDGE,"E9.7.17.0"),sQuery(id+"F0.wireOp",EDGE,"E9.11.17.0"),sQuery(id+"F0.wireOp",EDGE,"E9.14.17.0"),sQuery(id+"F0.wireOp",EDGE,"E9.1.18.0"),sQuery(id+"F0.wireOp",EDGE,"E9.3.18.0"),sQuery(id+"F0.wireOp",EDGE,"E9.7.18.0"),sQuery(id+"F0.wireOp",EDGE,"E9.11.18.0"),sQuery(id+"F0.wireOp",EDGE,"E9.14.18.0"),sQuery(id+"F0.wireOp",EDGE,"E9.1.19.0"),sQuery(id+"F0.wireOp",EDGE,"E9.3.19.0"),sQuery(id+"F0.wireOp",EDGE,"E9.7.19.0"),sQuery(id+"F0.wireOp",EDGE,"E9.11.19.0"),sQuery(id+"F0.wireOp",EDGE,"E9.14.19.0"),sQuery(id+"F0.wireOp",EDGE,"E9.1.20.0"),sQuery(id+"F0.wireOp",EDGE,"E9.3.20.0"),sQuery(id+"F0.wireOp",EDGE,"E9.7.20.0"),sQuery(id+"F0.wireOp",EDGE,"E9.11.20.0"),sQuery(id+"F0.wireOp",EDGE,"E9.14.20.0"),sQuery(id+"F0.wireOp",EDGE,"E9.1.21.0"),sQuery(id+"F0.wireOp",EDGE,"E9.3.21.0"),sQuery(id+"F0.wireOp",EDGE,"E9.7.21.0"),sQuery(id+"F0.wireOp",EDGE,"E9.11.21.0"),sQuery(id+"F0.wireOp",EDGE,"E9.14.21.0"),sQuery(id+"F0.wireOp",EDGE,"E9.1.22.0"),sQuery(id+"F0.wireOp",EDGE,"E9.3.22.0"),sQuery(id+"F0.wireOp",EDGE,"E9.7.22.0"),sQuery(id+"F0.wireOp",EDGE,"E9.11.22.0"),sQuery(id+"F0.wireOp",EDGE,"E9.14.22.0"),sQuery(id+"F0.wireOp",EDGE,"E9.1.23.0"),sQuery(id+"F0.wireOp",EDGE,"E9.3.23.0"),sQuery(id+"F0.wireOp",EDGE,"E9.7.23.0"),sQuery(id+"F0.wireOp",EDGE,"E9.11.23.0"),sQuery(id+"F0.wireOp",EDGE,"E9.14.23.0"),sQuery(id+"F0.wireOp",EDGE,"E9.1.24.0"),sQuery(id+"F0.wireOp",EDGE,"E9.3.24.0"),sQuery(id+"F0.wireOp",EDGE,"E9.7.24.0"),sQuery(id+"F0.wireOp",EDGE,"E9.11.24.0"),sQuery(id+"F0.wireOp",EDGE,"E9.14.24.0"),sQuery(id+"F0.wireOp",EDGE,"E9.1.25.0"),sQuery(id+"F0.wireOp",EDGE,"E9.3.25.0"),sQuery(id+"F0.wireOp",EDGE,"E9.7.25.0"),sQuery(id+"F0.wireOp",EDGE,"E9.11.25.0"),sQuery(id+"F0.wireOp",EDGE,"E9.14.25.0"),sQuery(id+"F0.wireOp",EDGE,"E9.1.26.0"),sQuery(id+"F0.wireOp",EDGE,"E9.3.26.0"),sQuery(id+"F0.wireOp",EDGE,"E9.7.26.0"),sQuery(id+"F0.wireOp",EDGE,"E9.11.26.0"),sQuery(id+"F0.wireOp",EDGE,"E9.14.26.0"),sQuery(id+"F0.wireOp",EDGE,"E9.1.27.0"),sQuery(id+"F0.wireOp",EDGE,"E9.3.27.0"),sQuery(id+"F0.wireOp",EDGE,"E9.7.27.0"),sQuery(id+"F0.wireOp",EDGE,"E9.11.27.0"),sQuery(id+"F0.wireOp",EDGE,"E9.14.27.0"),sQuery(id+"F0.wireOp",EDGE,"E9.1.28.0"),sQuery(id+"F0.wireOp",EDGE,"E9.3.28.0"),sQuery(id+"F0.wireOp",EDGE,"E9.7.28.0"),sQuery(id+"F0.wireOp",EDGE,"E9.11.28.0"),sQuery(id+"F0.wireOp",EDGE,"E9.14.28.0"),sQuery(id+"F0.wireOp",EDGE,"E9.1.29.0"),sQuery(id+"F0.wireOp",EDGE,"E9.3.29.0"),sQuery(id+"F0.wireOp",EDGE,"E9.7.29.0"),sQuery(id+"F0.wireOp",EDGE,"E9.11.29.0"),sQuery(id+"F0.wireOp",EDGE,"E9.14.29.0"),sQuery(id+"F0.wireOp",EDGE,"E9.1.30.0"),sQuery(id+"F0.wireOp",EDGE,"E9.3.30.0"),sQuery(id+"F0.wireOp",EDGE,"E9.7.30.0"),sQuery(id+"F0.wireOp",EDGE,"E9.11.30.0"),sQuery(id+"F0.wireOp",EDGE,"E9.14.30.0"),sQuery(id+"F0.wireOp",EDGE,"E9.1.31.0"),sQuery(id+"F0.wireOp",EDGE,"E9.3.31.0"),sQuery(id+"F0.wireOp",EDGE,"E9.7.31.0"),sQuery(id+"F0.wireOp",EDGE,"E9.11.31.0"),sQuery(id+"F0.wireOp",EDGE,"E9.14.31.0"),sQuery(id+"F0.wireOp",EDGE,"E9.1.32.0"),sQuery(id+"F0.wireOp",EDGE,"E9.3.32.0"),sQuery(id+"F0.wireOp",EDGE,"E9.7.32.0"),sQuery(id+"F0.wireOp",EDGE,"E9.11.32.0"),sQuery(id+"F0.wireOp",EDGE,"E9.14.32.0"),sQuery(id+"F0.wireOp",EDGE,"E9.1.33.0"),sQuery(id+"F0.wireOp",EDGE,"E9.3.33.0"),sQuery(id+"F0.wireOp",EDGE,"E9.7.33.0"),sQuery(id+"F0.wireOp",EDGE,"E9.11.33.0"),sQuery(id+"F0.wireOp",EDGE,"E9.14.33.0"),sQuery(id+"F0.wireOp",EDGE,"E9.1.34.0"),sQuery(id+"F0.wireOp",EDGE,"E9.3.34.0"),sQuery(id+"F0.wireOp",EDGE,"E9.7.34.0"),sQuery(id+"F0.wireOp",EDGE,"E9.11.34.0"),sQuery(id+"F0.wireOp",EDGE,"E9.14.34.0"),sQuery(id+"F0.wireOp",EDGE,"E9.1.35.0"),sQuery(id+"F0.wireOp",EDGE,"E9.3.35.0"),sQuery(id+"F0.wireOp",EDGE,"E9.7.35.0"),sQuery(id+"F0.wireOp",EDGE,"E9.11.35.0"),sQuery(id+"F0.wireOp",EDGE,"E9.14.35.0"),sQuery(id+"F0.wireOp",EDGE,"E9.1.36.0"),sQuery(id+"F0.wireOp",EDGE,"E9.3.36.0"),sQuery(id+"F0.wireOp",EDGE,"E9.7.36.0"),sQuery(id+"F0.wireOp",EDGE,"E9.11.36.0"),sQuery(id+"F0.wireOp",EDGE,"E9.14.36.0"),sQuery(id+"F0.wireOp",EDGE,"E9.1.37.0"),sQuery(id+"F0.wireOp",EDGE,"E9.3.37.0"),sQuery(id+"F0.wireOp",EDGE,"E9.7.37.0"),sQuery(id+"F0.wireOp",EDGE,"E9.11.37.0"),sQuery(id+"F0.wireOp",EDGE,"E9.14.37.0"),sQuery(id+"F0.wireOp",EDGE,"E9.1.38.0"),sQuery(id+"F0.wireOp",EDGE,"E9.3.38.0"),sQuery(id+"F0.wireOp",EDGE,"E9.7.38.0"),sQuery(id+"F0.wireOp",EDGE,"E9.11.38.0"),sQuery(id+"F0.wireOp",EDGE,"E9.14.38.0"),sQuery(id+"F0.wireOp",EDGE,"E9.1.39.0"),sQuery(id+"F0.wireOp",EDGE,"E9.3.39.0"),sQuery(id+"F0.wireOp",EDGE,"E9.7.39.0"),sQuery(id+"F0.wireOp",EDGE,"E9.11.39.0"),sQuery(id+"F0.wireOp",EDGE,"E9.14.39.0"),sQuery(id+"F0.wireOp",EDGE,"E9.1.40.0"),sQuery(id+"F0.wireOp",EDGE,"E9.3.40.0"),sQuery(id+"F0.wireOp",EDGE,"E9.7.40.0"),sQuery(id+"F0.wireOp",EDGE,"E9.11.40.0"),sQuery(id+"F0.wireOp",EDGE,"E9.14.40.0"),sQuery(id+"F0.wireOp",EDGE,"E9.1.41.0"),sQuery(id+"F0.wireOp",EDGE,"E9.3.41.0"),sQuery(id+"F0.wireOp",EDGE,"E9.7.41.0"),sQuery(id+"F0.wireOp",EDGE,"E9.11.41.0"),sQuery(id+"F0.wireOp",EDGE,"E9.14.41.0"),sQuery(id+"F0.wireOp",EDGE,"E9.1.42.0"),sQuery(id+"F0.wireOp",EDGE,"E9.3.42.0"),sQuery(id+"F0.wireOp",EDGE,"E9.7.42.0"),sQuery(id+"F0.wireOp",EDGE,"E9.11.42.0"),sQuery(id+"F0.wireOp",EDGE,"E9.14.42.0"),sQuery(id+"F0.wireOp",EDGE,"E9.1.43.0"),sQuery(id+"F0.wireOp",EDGE,"E9.3.43.0"),sQuery(id+"F0.wireOp",EDGE,"E9.7.43.0"),sQuery(id+"F0.wireOp",EDGE,"E9.11.43.0"),sQuery(id+"F0.wireOp",EDGE,"E9.14.43.0"),sQuery(id+"F0.wireOp",EDGE,"E9.1.44.0"),sQuery(id+"F0.wireOp",EDGE,"E9.3.44.0"),sQuery(id+"F0.wireOp",EDGE,"E9.7.44.0"),sQuery(id+"F0.wireOp",EDGE,"E9.11.44.0"),sQuery(id+"F0.wireOp",EDGE,"E9.14.44.0"),sQuery(id+"F0.wireOp",EDGE,"E9.1.45.0"),sQuery(id+"F0.wireOp",EDGE,"E9.3.45.0"),sQuery(id+"F0.wireOp",EDGE,"E9.7.45.0"),sQuery(id+"F0.wireOp",EDGE,"E9.11.45.0"),sQuery(id+"F0.wireOp",EDGE,"E9.14.45.0"),sQuery(id+"F0.wireOp",EDGE,"E9.1.46.0"),sQuery(id+"F0.wireOp",EDGE,"E9.3.46.0"),sQuery(id+"F0.wireOp",EDGE,"E9.7.46.0"),sQuery(id+"F0.wireOp",EDGE,"E9.11.46.0"),sQuery(id+"F0.wireOp",EDGE,"E9.14.46.0"),sQuery(id+"F0.wireOp",EDGE,"E9.1.47.0"),sQuery(id+"F0.wireOp",EDGE,"E9.3.47.0"),sQuery(id+"F0.wireOp",EDGE,"E9.7.47.0"),sQuery(id+"F0.wireOp",EDGE,"E9.11.47.0"),sQuery(id+"F0.wireOp",EDGE,"E9.14.47.0"),sQuery(id+"F0.wireOp",EDGE,"E9.1.48.0"),sQuery(id+"F0.wireOp",EDGE,"E9.3.48.0"),sQuery(id+"F0.wireOp",EDGE,"E9.7.48.0"),sQuery(id+"F0.wireOp",EDGE,"E9.11.48.0"),sQuery(id+"F0.wireOp",EDGE,"E9.14.48.0"),sQuery(id+"F0.wireOp",EDGE,"E9.1.49.0"),sQuery(id+"F0.wireOp",EDGE,"E9.3.49.0"),sQuery(id+"F0.wireOp",EDGE,"E9.7.49.0"),sQuery(id+"F0.wireOp",EDGE,"E9.11.49.0"),sQuery(id+"F0.wireOp",EDGE,"E9.14.49.0"),sQuery(id+"F0.wireOp",EDGE,"E9.1.50.0"),sQuery(id+"F0.wireOp",EDGE,"E9.3.50.0"),sQuery(id+"F0.wireOp",EDGE,"E9.7.50.0"),sQuery(id+"F0.wireOp",EDGE,"E9.11.50.0"),sQuery(id+"F0.wireOp",EDGE,"E9.14.50.0"),sQuery(id+"F0.wireOp",EDGE,"E9.1.51.0"),sQuery(id+"F0.wireOp",EDGE,"E9.3.51.0"),sQuery(id+"F0.wireOp",EDGE,"E9.7.51.0"),sQuery(id+"F0.wireOp",EDGE,"E9.11.51.0"),sQuery(id+"F0.wireOp",EDGE,"E9.14.51.0"),sQuery(id+"F0.wireOp",EDGE,"E9.1.52.0"),sQuery(id+"F0.wireOp",EDGE,"E9.3.52.0"),sQuery(id+"F0.wireOp",EDGE,"E9.7.52.0"),sQuery(id+"F0.wireOp",EDGE,"E9.11.52.0"),sQuery(id+"F0.wireOp",EDGE,"E9.14.52.0"),sQuery(id+"F0.wireOp",EDGE,"E9.1.53.0"),sQuery(id+"F0.wireOp",EDGE,"E9.3.53.0"),sQuery(id+"F0.wireOp",EDGE,"E9.7.53.0"),sQuery(id+"F0.wireOp",EDGE,"E9.11.53.0"),sQuery(id+"F0.wireOp",EDGE,"E9.14.53.0"),sQuery(id+"F0.wireOp",EDGE,"E9.1.54.0"),sQuery(id+"F0.wireOp",EDGE,"E9.3.54.0"),sQuery(id+"F0.wireOp",EDGE,"E9.7.54.0"),sQuery(id+"F0.wireOp",EDGE,"E9.11.54.0"),sQuery(id+"F0.wireOp",EDGE,"E9.14.54.0"),sQuery(id+"F0.wireOp",EDGE,"E9.1.55.0"),sQuery(id+"F0.wireOp",EDGE,"E9.3.55.0"),sQuery(id+"F0.wireOp",EDGE,"E9.7.55.0"),sQuery(id+"F0.wireOp",EDGE,"E9.11.55.0"),sQuery(id+"F0.wireOp",EDGE,"E9.14.55.0"),sQuery(id+"F0.wireOp",EDGE,"E9.1.56.0"),sQuery(id+"F0.wireOp",EDGE,"E9.3.56.0"),sQuery(id+"F0.wireOp",EDGE,"E9.7.56.0"),sQuery(id+"F0.wireOp",EDGE,"E9.11.56.0"),sQuery(id+"F0.wireOp",EDGE,"E9.14.56.0"),sQuery(id+"F0.wireOp",EDGE,"E9.1.57.0"),sQuery(id+"F0.wireOp",EDGE,"E9.3.57.0"),sQuery(id+"F0.wireOp",EDGE,"E9.7.57.0"),sQuery(id+"F0.wireOp",EDGE,"E9.11.57.0"),sQuery(id+"F0.wireOp",EDGE,"E9.14.57.0"),sQuery(id+"F0.wireOp",EDGE,"E9.1.58.0"),sQuery(id+"F0.wireOp",EDGE,"E9.3.58.0"),sQuery(id+"F0.wireOp",EDGE,"E9.7.58.0"),sQuery(id+"F0.wireOp",EDGE,"E9.11.58.0"),sQuery(id+"F0.wireOp",EDGE,"E9.14.58.0"),sQuery(id+"F0.wireOp",EDGE,"E9.1.59.0"),sQuery(id+"F0.wireOp",EDGE,"E9.3.59.0"),sQuery(id+"F0.wireOp",EDGE,"E9.7.59.0"),sQuery(id+"F0.wireOp",EDGE,"E9.11.59.0"),sQuery(id+"F0.wireOp",EDGE,"E9.14.59.0")])],"isStart":false});
            var sketch = newSketch(context, id + "F2", { "sketchPlane" : qUnion([Q0])});
            skCircle(sketch, "E10", {"center": v(0, 0) * mm, "radius": 64 * mm});
            skCircle(sketch, "E11", {"center": v(0, 0) * mm, "radius": 63 * mm});
            skCircle(sketch, "E12", {"center": v(0, 0) * mm, "radius": 60 * mm});
            skCircle(sketch, "E13", {"center": v(0, 0) * mm, "radius": 59 * mm});
            skCircle(sketch, "E14", {"center": v(0, 0) * mm, "radius": 10 * mm});
            skCircle(sketch, "E15", {"center": v(0, 0) * mm, "radius": 58 * mm});
            skCircle(sketch, "E16", {"center": v(0, 0) * mm, "radius": 11 * mm});
            skLineSegment(sketch, "E17", {"start": v(0, -58) * mm, "end": v(0, 58) * mm, "construction": true});
            skLineSegment(sketch, "E18", {"start": v(58, 0) * mm, "end": v(-58, 0) * mm, "construction": true});
            skLineSegment(sketch, "E19", {"start": v(-46.28, 5) * mm, "end": v(-14.5, 5) * mm});
            skLineSegment(sketch, "E20.0", {"start": v(-46.28, -5) * mm, "end": v(-14.5, -5) * mm});
            skLineSegment(sketch, "E21", {"start": v(-5, -46.28) * mm, "end": v(-5, -14.5) * mm});
            skLineSegment(sketch, "E22.0", {"start": v(5, -46.28) * mm, "end": v(5, -14.5) * mm});
            skArc(sketch, "E23", {"start": v(5, 14.5) * mm, "mid": v(7.78, 7.78) * mm, "end": v(14.5, 5) * mm});
            skArc(sketch, "E24", {"start": v(-14.5, 5) * mm, "mid": v(-7.78, 7.78) * mm, "end": v(-5, 14.5) * mm});
            skArc(sketch, "E25", {"start": v(-5, -14.5) * mm, "mid": v(-7.78, -7.78) * mm, "end": v(-14.5, -5) * mm});
            skArc(sketch, "E26", {"start": v(14.5, -5) * mm, "mid": v(7.78, -7.78) * mm, "end": v(5, -14.5) * mm});
            skArc(sketch, "E27", {"start": v(46.28, 5) * mm, "mid": v(53.94, 8.88) * mm, "end": v(55.35, 17.34) * mm});
            skArc(sketch, "E28", {"start": v(17.34, 55.35) * mm, "mid": v(8.88, 53.94) * mm, "end": v(5, 46.28) * mm});
            skArc(sketch, "E29", {"start": v(-5, 46.28) * mm, "mid": v(-8.88, 53.94) * mm, "end": v(-17.34, 55.35) * mm});
            skArc(sketch, "E30", {"start": v(-55.35, 17.34) * mm, "mid": v(-53.94, 8.88) * mm, "end": v(-46.28, 5) * mm});
            skArc(sketch, "E31", {"start": v(-46.28, -5) * mm, "mid": v(-53.94, -8.88) * mm, "end": v(-55.35, -17.34) * mm});
            skArc(sketch, "E32", {"start": v(-17.34, -55.35) * mm, "mid": v(-8.88, -53.94) * mm, "end": v(-5, -46.28) * mm});
            skArc(sketch, "E33", {"start": v(5, -46.28) * mm, "mid": v(8.88, -53.94) * mm, "end": v(17.34, -55.35) * mm});
            skArc(sketch, "E34", {"start": v(55.35, -17.34) * mm, "mid": v(53.94, -8.88) * mm, "end": v(46.28, -5) * mm});
            skLineSegment(sketch, "E35.trimOffspring", {"start": v(-5, 14.5) * mm, "end": v(-5, 46.28) * mm});
            skLineSegment(sketch, "E36.trimOffspring", {"start": v(14.5, 5) * mm, "end": v(46.28, 5) * mm});
            skLineSegment(sketch, "E37.trimOffspring", {"start": v(5, 14.5) * mm, "end": v(5, 46.28) * mm});
            skLineSegment(sketch, "E38.trimOffspring", {"start": v(14.5, -5) * mm, "end": v(46.28, -5) * mm});
            skSolve(sketch);
        }
        {
            var Q0;
            Q0=makeQuery(id+"F1.opExtrude","CAP_FACE",FACE,{"disambiguationData":[OSD([sQuery(id+"F0.wireOp",EDGE,"E0"),sQuery(id+"F0.wireOp",EDGE,"E1"),sQuery(id+"F0.wireOp",EDGE,"E3"),sQuery(id+"F0.wireOp",EDGE,"E4"),sQuery(id+"F0.wireOp",EDGE,"E5"),sQuery(id+"F0.wireOp",EDGE,"E6.trimOffspring"),sQuery(id+"F0.wireOp",EDGE,"E7"),sQuery(id+"F0.wireOp",EDGE,"E8.1.0"),sQuery(id+"F0.wireOp",EDGE,"E8.1.1"),sQuery(id+"F0.wireOp",EDGE,"E8.1.2"),sQuery(id+"F0.wireOp",EDGE,"E8.1.3"),sQuery(id+"F0.wireOp",EDGE,"E8.1.4"),sQuery(id+"F0.wireOp",EDGE,"E8.2.0"),sQuery(id+"F0.wireOp",EDGE,"E8.2.1"),sQuery(id+"F0.wireOp",EDGE,"E8.2.2"),sQuery(id+"F0.wireOp",EDGE,"E8.2.3"),sQuery(id+"F0.wireOp",EDGE,"E8.2.4"),sQuery(id+"F0.wireOp",EDGE,"E9.1.3.0"),sQuery(id+"F0.wireOp",EDGE,"E9.3.3.0"),sQuery(id+"F0.wireOp",EDGE,"E9.7.3.0"),sQuery(id+"F0.wireOp",EDGE,"E9.11.3.0"),sQuery(id+"F0.wireOp",EDGE,"E9.14.3.0"),sQuery(id+"F0.wireOp",EDGE,"E9.1.4.0"),sQuery(id+"F0.wireOp",EDGE,"E9.3.4.0"),sQuery(id+"F0.wireOp",EDGE,"E9.7.4.0"),sQuery(id+"F0.wireOp",EDGE,"E9.11.4.0"),sQuery(id+"F0.wireOp",EDGE,"E9.14.4.0"),sQuery(id+"F0.wireOp",EDGE,"E9.1.5.0"),sQuery(id+"F0.wireOp",EDGE,"E9.3.5.0"),sQuery(id+"F0.wireOp",EDGE,"E9.7.5.0"),sQuery(id+"F0.wireOp",EDGE,"E9.11.5.0"),sQuery(id+"F0.wireOp",EDGE,"E9.14.5.0"),sQuery(id+"F0.wireOp",EDGE,"E9.1.6.0"),sQuery(id+"F0.wireOp",EDGE,"E9.3.6.0"),sQuery(id+"F0.wireOp",EDGE,"E9.7.6.0"),sQuery(id+"F0.wireOp",EDGE,"E9.11.6.0"),sQuery(id+"F0.wireOp",EDGE,"E9.14.6.0"),sQuery(id+"F0.wireOp",EDGE,"E9.1.7.0"),sQuery(id+"F0.wireOp",EDGE,"E9.3.7.0"),sQuery(id+"F0.wireOp",EDGE,"E9.7.7.0"),sQuery(id+"F0.wireOp",EDGE,"E9.11.7.0"),sQuery(id+"F0.wireOp",EDGE,"E9.14.7.0"),sQuery(id+"F0.wireOp",EDGE,"E9.1.8.0"),sQuery(id+"F0.wireOp",EDGE,"E9.3.8.0"),sQuery(id+"F0.wireOp",EDGE,"E9.7.8.0"),sQuery(id+"F0.wireOp",EDGE,"E9.11.8.0"),sQuery(id+"F0.wireOp",EDGE,"E9.14.8.0"),sQuery(id+"F0.wireOp",EDGE,"E9.1.9.0"),sQuery(id+"F0.wireOp",EDGE,"E9.3.9.0"),sQuery(id+"F0.wireOp",EDGE,"E9.7.9.0"),sQuery(id+"F0.wireOp",EDGE,"E9.11.9.0"),sQuery(id+"F0.wireOp",EDGE,"E9.14.9.0"),sQuery(id+"F0.wireOp",EDGE,"E9.1.10.0"),sQuery(id+"F0.wireOp",EDGE,"E9.3.10.0"),sQuery(id+"F0.wireOp",EDGE,"E9.7.10.0"),sQuery(id+"F0.wireOp",EDGE,"E9.11.10.0"),sQuery(id+"F0.wireOp",EDGE,"E9.14.10.0"),sQuery(id+"F0.wireOp",EDGE,"E9.1.11.0"),sQuery(id+"F0.wireOp",EDGE,"E9.3.11.0"),sQuery(id+"F0.wireOp",EDGE,"E9.7.11.0"),sQuery(id+"F0.wireOp",EDGE,"E9.11.11.0"),sQuery(id+"F0.wireOp",EDGE,"E9.14.11.0"),sQuery(id+"F0.wireOp",EDGE,"E9.1.12.0"),sQuery(id+"F0.wireOp",EDGE,"E9.3.12.0"),sQuery(id+"F0.wireOp",EDGE,"E9.7.12.0"),sQuery(id+"F0.wireOp",EDGE,"E9.11.12.0"),sQuery(id+"F0.wireOp",EDGE,"E9.14.12.0"),sQuery(id+"F0.wireOp",EDGE,"E9.1.13.0"),sQuery(id+"F0.wireOp",EDGE,"E9.3.13.0"),sQuery(id+"F0.wireOp",EDGE,"E9.7.13.0"),sQuery(id+"F0.wireOp",EDGE,"E9.11.13.0"),sQuery(id+"F0.wireOp",EDGE,"E9.14.13.0"),sQuery(id+"F0.wireOp",EDGE,"E9.1.14.0"),sQuery(id+"F0.wireOp",EDGE,"E9.3.14.0"),sQuery(id+"F0.wireOp",EDGE,"E9.7.14.0"),sQuery(id+"F0.wireOp",EDGE,"E9.11.14.0"),sQuery(id+"F0.wireOp",EDGE,"E9.14.14.0"),sQuery(id+"F0.wireOp",EDGE,"E9.1.15.0"),sQuery(id+"F0.wireOp",EDGE,"E9.3.15.0"),sQuery(id+"F0.wireOp",EDGE,"E9.7.15.0"),sQuery(id+"F0.wireOp",EDGE,"E9.11.15.0"),sQuery(id+"F0.wireOp",EDGE,"E9.14.15.0"),sQuery(id+"F0.wireOp",EDGE,"E9.1.16.0"),sQuery(id+"F0.wireOp",EDGE,"E9.3.16.0"),sQuery(id+"F0.wireOp",EDGE,"E9.7.16.0"),sQuery(id+"F0.wireOp",EDGE,"E9.11.16.0"),sQuery(id+"F0.wireOp",EDGE,"E9.14.16.0"),sQuery(id+"F0.wireOp",EDGE,"E9.1.17.0"),sQuery(id+"F0.wireOp",EDGE,"E9.3.17.0"),sQuery(id+"F0.wireOp",EDGE,"E9.7.17.0"),sQuery(id+"F0.wireOp",EDGE,"E9.11.17.0"),sQuery(id+"F0.wireOp",EDGE,"E9.14.17.0"),sQuery(id+"F0.wireOp",EDGE,"E9.1.18.0"),sQuery(id+"F0.wireOp",EDGE,"E9.3.18.0"),sQuery(id+"F0.wireOp",EDGE,"E9.7.18.0"),sQuery(id+"F0.wireOp",EDGE,"E9.11.18.0"),sQuery(id+"F0.wireOp",EDGE,"E9.14.18.0"),sQuery(id+"F0.wireOp",EDGE,"E9.1.19.0"),sQuery(id+"F0.wireOp",EDGE,"E9.3.19.0"),sQuery(id+"F0.wireOp",EDGE,"E9.7.19.0"),sQuery(id+"F0.wireOp",EDGE,"E9.11.19.0"),sQuery(id+"F0.wireOp",EDGE,"E9.14.19.0"),sQuery(id+"F0.wireOp",EDGE,"E9.1.20.0"),sQuery(id+"F0.wireOp",EDGE,"E9.3.20.0"),sQuery(id+"F0.wireOp",EDGE,"E9.7.20.0"),sQuery(id+"F0.wireOp",EDGE,"E9.11.20.0"),sQuery(id+"F0.wireOp",EDGE,"E9.14.20.0"),sQuery(id+"F0.wireOp",EDGE,"E9.1.21.0"),sQuery(id+"F0.wireOp",EDGE,"E9.3.21.0"),sQuery(id+"F0.wireOp",EDGE,"E9.7.21.0"),sQuery(id+"F0.wireOp",EDGE,"E9.11.21.0"),sQuery(id+"F0.wireOp",EDGE,"E9.14.21.0"),sQuery(id+"F0.wireOp",EDGE,"E9.1.22.0"),sQuery(id+"F0.wireOp",EDGE,"E9.3.22.0"),sQuery(id+"F0.wireOp",EDGE,"E9.7.22.0"),sQuery(id+"F0.wireOp",EDGE,"E9.11.22.0"),sQuery(id+"F0.wireOp",EDGE,"E9.14.22.0"),sQuery(id+"F0.wireOp",EDGE,"E9.1.23.0"),sQuery(id+"F0.wireOp",EDGE,"E9.3.23.0"),sQuery(id+"F0.wireOp",EDGE,"E9.7.23.0"),sQuery(id+"F0.wireOp",EDGE,"E9.11.23.0"),sQuery(id+"F0.wireOp",EDGE,"E9.14.23.0"),sQuery(id+"F0.wireOp",EDGE,"E9.1.24.0"),sQuery(id+"F0.wireOp",EDGE,"E9.3.24.0"),sQuery(id+"F0.wireOp",EDGE,"E9.7.24.0"),sQuery(id+"F0.wireOp",EDGE,"E9.11.24.0"),sQuery(id+"F0.wireOp",EDGE,"E9.14.24.0"),sQuery(id+"F0.wireOp",EDGE,"E9.1.25.0"),sQuery(id+"F0.wireOp",EDGE,"E9.3.25.0"),sQuery(id+"F0.wireOp",EDGE,"E9.7.25.0"),sQuery(id+"F0.wireOp",EDGE,"E9.11.25.0"),sQuery(id+"F0.wireOp",EDGE,"E9.14.25.0"),sQuery(id+"F0.wireOp",EDGE,"E9.1.26.0"),sQuery(id+"F0.wireOp",EDGE,"E9.3.26.0"),sQuery(id+"F0.wireOp",EDGE,"E9.7.26.0"),sQuery(id+"F0.wireOp",EDGE,"E9.11.26.0"),sQuery(id+"F0.wireOp",EDGE,"E9.14.26.0"),sQuery(id+"F0.wireOp",EDGE,"E9.1.27.0"),sQuery(id+"F0.wireOp",EDGE,"E9.3.27.0"),sQuery(id+"F0.wireOp",EDGE,"E9.7.27.0"),sQuery(id+"F0.wireOp",EDGE,"E9.11.27.0"),sQuery(id+"F0.wireOp",EDGE,"E9.14.27.0"),sQuery(id+"F0.wireOp",EDGE,"E9.1.28.0"),sQuery(id+"F0.wireOp",EDGE,"E9.3.28.0"),sQuery(id+"F0.wireOp",EDGE,"E9.7.28.0"),sQuery(id+"F0.wireOp",EDGE,"E9.11.28.0"),sQuery(id+"F0.wireOp",EDGE,"E9.14.28.0"),sQuery(id+"F0.wireOp",EDGE,"E9.1.29.0"),sQuery(id+"F0.wireOp",EDGE,"E9.3.29.0"),sQuery(id+"F0.wireOp",EDGE,"E9.7.29.0"),sQuery(id+"F0.wireOp",EDGE,"E9.11.29.0"),sQuery(id+"F0.wireOp",EDGE,"E9.14.29.0"),sQuery(id+"F0.wireOp",EDGE,"E9.1.30.0"),sQuery(id+"F0.wireOp",EDGE,"E9.3.30.0"),sQuery(id+"F0.wireOp",EDGE,"E9.7.30.0"),sQuery(id+"F0.wireOp",EDGE,"E9.11.30.0"),sQuery(id+"F0.wireOp",EDGE,"E9.14.30.0"),sQuery(id+"F0.wireOp",EDGE,"E9.1.31.0"),sQuery(id+"F0.wireOp",EDGE,"E9.3.31.0"),sQuery(id+"F0.wireOp",EDGE,"E9.7.31.0"),sQuery(id+"F0.wireOp",EDGE,"E9.11.31.0"),sQuery(id+"F0.wireOp",EDGE,"E9.14.31.0"),sQuery(id+"F0.wireOp",EDGE,"E9.1.32.0"),sQuery(id+"F0.wireOp",EDGE,"E9.3.32.0"),sQuery(id+"F0.wireOp",EDGE,"E9.7.32.0"),sQuery(id+"F0.wireOp",EDGE,"E9.11.32.0"),sQuery(id+"F0.wireOp",EDGE,"E9.14.32.0"),sQuery(id+"F0.wireOp",EDGE,"E9.1.33.0"),sQuery(id+"F0.wireOp",EDGE,"E9.3.33.0"),sQuery(id+"F0.wireOp",EDGE,"E9.7.33.0"),sQuery(id+"F0.wireOp",EDGE,"E9.11.33.0"),sQuery(id+"F0.wireOp",EDGE,"E9.14.33.0"),sQuery(id+"F0.wireOp",EDGE,"E9.1.34.0"),sQuery(id+"F0.wireOp",EDGE,"E9.3.34.0"),sQuery(id+"F0.wireOp",EDGE,"E9.7.34.0"),sQuery(id+"F0.wireOp",EDGE,"E9.11.34.0"),sQuery(id+"F0.wireOp",EDGE,"E9.14.34.0"),sQuery(id+"F0.wireOp",EDGE,"E9.1.35.0"),sQuery(id+"F0.wireOp",EDGE,"E9.3.35.0"),sQuery(id+"F0.wireOp",EDGE,"E9.7.35.0"),sQuery(id+"F0.wireOp",EDGE,"E9.11.35.0"),sQuery(id+"F0.wireOp",EDGE,"E9.14.35.0"),sQuery(id+"F0.wireOp",EDGE,"E9.1.36.0"),sQuery(id+"F0.wireOp",EDGE,"E9.3.36.0"),sQuery(id+"F0.wireOp",EDGE,"E9.7.36.0"),sQuery(id+"F0.wireOp",EDGE,"E9.11.36.0"),sQuery(id+"F0.wireOp",EDGE,"E9.14.36.0"),sQuery(id+"F0.wireOp",EDGE,"E9.1.37.0"),sQuery(id+"F0.wireOp",EDGE,"E9.3.37.0"),sQuery(id+"F0.wireOp",EDGE,"E9.7.37.0"),sQuery(id+"F0.wireOp",EDGE,"E9.11.37.0"),sQuery(id+"F0.wireOp",EDGE,"E9.14.37.0"),sQuery(id+"F0.wireOp",EDGE,"E9.1.38.0"),sQuery(id+"F0.wireOp",EDGE,"E9.3.38.0"),sQuery(id+"F0.wireOp",EDGE,"E9.7.38.0"),sQuery(id+"F0.wireOp",EDGE,"E9.11.38.0"),sQuery(id+"F0.wireOp",EDGE,"E9.14.38.0"),sQuery(id+"F0.wireOp",EDGE,"E9.1.39.0"),sQuery(id+"F0.wireOp",EDGE,"E9.3.39.0"),sQuery(id+"F0.wireOp",EDGE,"E9.7.39.0"),sQuery(id+"F0.wireOp",EDGE,"E9.11.39.0"),sQuery(id+"F0.wireOp",EDGE,"E9.14.39.0"),sQuery(id+"F0.wireOp",EDGE,"E9.1.40.0"),sQuery(id+"F0.wireOp",EDGE,"E9.3.40.0"),sQuery(id+"F0.wireOp",EDGE,"E9.7.40.0"),sQuery(id+"F0.wireOp",EDGE,"E9.11.40.0"),sQuery(id+"F0.wireOp",EDGE,"E9.14.40.0"),sQuery(id+"F0.wireOp",EDGE,"E9.1.41.0"),sQuery(id+"F0.wireOp",EDGE,"E9.3.41.0"),sQuery(id+"F0.wireOp",EDGE,"E9.7.41.0"),sQuery(id+"F0.wireOp",EDGE,"E9.11.41.0"),sQuery(id+"F0.wireOp",EDGE,"E9.14.41.0"),sQuery(id+"F0.wireOp",EDGE,"E9.1.42.0"),sQuery(id+"F0.wireOp",EDGE,"E9.3.42.0"),sQuery(id+"F0.wireOp",EDGE,"E9.7.42.0"),sQuery(id+"F0.wireOp",EDGE,"E9.11.42.0"),sQuery(id+"F0.wireOp",EDGE,"E9.14.42.0"),sQuery(id+"F0.wireOp",EDGE,"E9.1.43.0"),sQuery(id+"F0.wireOp",EDGE,"E9.3.43.0"),sQuery(id+"F0.wireOp",EDGE,"E9.7.43.0"),sQuery(id+"F0.wireOp",EDGE,"E9.11.43.0"),sQuery(id+"F0.wireOp",EDGE,"E9.14.43.0"),sQuery(id+"F0.wireOp",EDGE,"E9.1.44.0"),sQuery(id+"F0.wireOp",EDGE,"E9.3.44.0"),sQuery(id+"F0.wireOp",EDGE,"E9.7.44.0"),sQuery(id+"F0.wireOp",EDGE,"E9.11.44.0"),sQuery(id+"F0.wireOp",EDGE,"E9.14.44.0"),sQuery(id+"F0.wireOp",EDGE,"E9.1.45.0"),sQuery(id+"F0.wireOp",EDGE,"E9.3.45.0"),sQuery(id+"F0.wireOp",EDGE,"E9.7.45.0"),sQuery(id+"F0.wireOp",EDGE,"E9.11.45.0"),sQuery(id+"F0.wireOp",EDGE,"E9.14.45.0"),sQuery(id+"F0.wireOp",EDGE,"E9.1.46.0"),sQuery(id+"F0.wireOp",EDGE,"E9.3.46.0"),sQuery(id+"F0.wireOp",EDGE,"E9.7.46.0"),sQuery(id+"F0.wireOp",EDGE,"E9.11.46.0"),sQuery(id+"F0.wireOp",EDGE,"E9.14.46.0"),sQuery(id+"F0.wireOp",EDGE,"E9.1.47.0"),sQuery(id+"F0.wireOp",EDGE,"E9.3.47.0"),sQuery(id+"F0.wireOp",EDGE,"E9.7.47.0"),sQuery(id+"F0.wireOp",EDGE,"E9.11.47.0"),sQuery(id+"F0.wireOp",EDGE,"E9.14.47.0"),sQuery(id+"F0.wireOp",EDGE,"E9.1.48.0"),sQuery(id+"F0.wireOp",EDGE,"E9.3.48.0"),sQuery(id+"F0.wireOp",EDGE,"E9.7.48.0"),sQuery(id+"F0.wireOp",EDGE,"E9.11.48.0"),sQuery(id+"F0.wireOp",EDGE,"E9.14.48.0"),sQuery(id+"F0.wireOp",EDGE,"E9.1.49.0"),sQuery(id+"F0.wireOp",EDGE,"E9.3.49.0"),sQuery(id+"F0.wireOp",EDGE,"E9.7.49.0"),sQuery(id+"F0.wireOp",EDGE,"E9.11.49.0"),sQuery(id+"F0.wireOp",EDGE,"E9.14.49.0"),sQuery(id+"F0.wireOp",EDGE,"E9.1.50.0"),sQuery(id+"F0.wireOp",EDGE,"E9.3.50.0"),sQuery(id+"F0.wireOp",EDGE,"E9.7.50.0"),sQuery(id+"F0.wireOp",EDGE,"E9.11.50.0"),sQuery(id+"F0.wireOp",EDGE,"E9.14.50.0"),sQuery(id+"F0.wireOp",EDGE,"E9.1.51.0"),sQuery(id+"F0.wireOp",EDGE,"E9.3.51.0"),sQuery(id+"F0.wireOp",EDGE,"E9.7.51.0"),sQuery(id+"F0.wireOp",EDGE,"E9.11.51.0"),sQuery(id+"F0.wireOp",EDGE,"E9.14.51.0"),sQuery(id+"F0.wireOp",EDGE,"E9.1.52.0"),sQuery(id+"F0.wireOp",EDGE,"E9.3.52.0"),sQuery(id+"F0.wireOp",EDGE,"E9.7.52.0"),sQuery(id+"F0.wireOp",EDGE,"E9.11.52.0"),sQuery(id+"F0.wireOp",EDGE,"E9.14.52.0"),sQuery(id+"F0.wireOp",EDGE,"E9.1.53.0"),sQuery(id+"F0.wireOp",EDGE,"E9.3.53.0"),sQuery(id+"F0.wireOp",EDGE,"E9.7.53.0"),sQuery(id+"F0.wireOp",EDGE,"E9.11.53.0"),sQuery(id+"F0.wireOp",EDGE,"E9.14.53.0"),sQuery(id+"F0.wireOp",EDGE,"E9.1.54.0"),sQuery(id+"F0.wireOp",EDGE,"E9.3.54.0"),sQuery(id+"F0.wireOp",EDGE,"E9.7.54.0"),sQuery(id+"F0.wireOp",EDGE,"E9.11.54.0"),sQuery(id+"F0.wireOp",EDGE,"E9.14.54.0"),sQuery(id+"F0.wireOp",EDGE,"E9.1.55.0"),sQuery(id+"F0.wireOp",EDGE,"E9.3.55.0"),sQuery(id+"F0.wireOp",EDGE,"E9.7.55.0"),sQuery(id+"F0.wireOp",EDGE,"E9.11.55.0"),sQuery(id+"F0.wireOp",EDGE,"E9.14.55.0"),sQuery(id+"F0.wireOp",EDGE,"E9.1.56.0"),sQuery(id+"F0.wireOp",EDGE,"E9.3.56.0"),sQuery(id+"F0.wireOp",EDGE,"E9.7.56.0"),sQuery(id+"F0.wireOp",EDGE,"E9.11.56.0"),sQuery(id+"F0.wireOp",EDGE,"E9.14.56.0"),sQuery(id+"F0.wireOp",EDGE,"E9.1.57.0"),sQuery(id+"F0.wireOp",EDGE,"E9.3.57.0"),sQuery(id+"F0.wireOp",EDGE,"E9.7.57.0"),sQuery(id+"F0.wireOp",EDGE,"E9.11.57.0"),sQuery(id+"F0.wireOp",EDGE,"E9.14.57.0"),sQuery(id+"F0.wireOp",EDGE,"E9.1.58.0"),sQuery(id+"F0.wireOp",EDGE,"E9.3.58.0"),sQuery(id+"F0.wireOp",EDGE,"E9.7.58.0"),sQuery(id+"F0.wireOp",EDGE,"E9.11.58.0"),sQuery(id+"F0.wireOp",EDGE,"E9.14.58.0"),sQuery(id+"F0.wireOp",EDGE,"E9.1.59.0"),sQuery(id+"F0.wireOp",EDGE,"E9.3.59.0"),sQuery(id+"F0.wireOp",EDGE,"E9.7.59.0"),sQuery(id+"F0.wireOp",EDGE,"E9.11.59.0"),sQuery(id+"F0.wireOp",EDGE,"E9.14.59.0")])],"isStart":true});
            var sketch = newSketch(context, id + "F3", { "sketchPlane" : qUnion([Q0])});
            skCircle(sketch, "E39", {"center": v(-0.15, 0.02) * mm, "radius": 64 * mm});
            skCircle(sketch, "E40", {"center": v(-0.15, 0.02) * mm, "radius": 63 * mm});
            skCircle(sketch, "E41", {"center": v(-0.15, 0.02) * mm, "radius": 60 * mm});
            skCircle(sketch, "E42", {"center": v(-0.15, 0.02) * mm, "radius": 59 * mm});
            skCircle(sketch, "E43", {"center": v(-0.15, 0.02) * mm, "radius": 10 * mm});
            skSolve(sketch);
        }
        {
            var Q0;
            Q0=makeQuery(id+"F3.imprint","IMPRINT",FACE,{"disambiguationData":[TD([[makeQuery(id+"F3.imprint","IMPRINT",EDGE,{"derivedFrom":sQuery(id+"F3.wireOp",EDGE,"E39")}),1.0]])]});
            var Q1;
            Q1=makeQuery(id+"F3.imprint","IMPRINT",FACE,{"disambiguationData":[TD([[makeQuery(id+"F3.imprint","IMPRINT",EDGE,{"derivedFrom":sQuery(id+"F3.wireOp",EDGE,"E42")}),1.0]])]});
            var Q2;
            Q2 = qConstructionFilter(qBodyType(qCreatedBy(id + "F3" ,EDGE), BodyType.WIRE), ConstructionObject.NO);
            extrude(context, id + "F4", {"entities" : qUnion([Q0, Q1]), "operationType" : NewBodyOperationType.REMOVE, "surfaceEntities" : qUnion([Q2]), "oppositeDirection" : true, "depth" : 1 * mm, "offsetDistance" : 25 * mm});
        }
        {
            var Q0;
            Q0=makeQuery(id+"FLAiNYIGUJVPJrN_1.boolean.opBoolean","SPLIT",FACE,{"disambiguationData":[TD([makeQuery(id+"FLAiNYIGUJVPJrN_1.opExtrude","SWEPT_FACE",FACE,{"disambiguationData":[OSD([sQuery(id+"F2.wireOp",EDGE,"E15")])]})])],"derivedFrom":makeQuery(id+"F1.opExtrude","CAP_FACE",FACE,{"disambiguationData":[OSD([sQuery(id+"F0.wireOp",EDGE,"E0"),sQuery(id+"F0.wireOp",EDGE,"E1"),sQuery(id+"F0.wireOp",EDGE,"E3"),sQuery(id+"F0.wireOp",EDGE,"E4"),sQuery(id+"F0.wireOp",EDGE,"E5"),sQuery(id+"F0.wireOp",EDGE,"E6.trimOffspring"),sQuery(id+"F0.wireOp",EDGE,"E7"),sQuery(id+"F0.wireOp",EDGE,"E8.1.0"),sQuery(id+"F0.wireOp",EDGE,"E8.1.1"),sQuery(id+"F0.wireOp",EDGE,"E8.1.2"),sQuery(id+"F0.wireOp",EDGE,"E8.1.3"),sQuery(id+"F0.wireOp",EDGE,"E8.1.4"),sQuery(id+"F0.wireOp",EDGE,"E8.2.0"),sQuery(id+"F0.wireOp",EDGE,"E8.2.1"),sQuery(id+"F0.wireOp",EDGE,"E8.2.2"),sQuery(id+"F0.wireOp",EDGE,"E8.2.3"),sQuery(id+"F0.wireOp",EDGE,"E8.2.4"),sQuery(id+"F0.wireOp",EDGE,"E9.1.3.0"),sQuery(id+"F0.wireOp",EDGE,"E9.3.3.0"),sQuery(id+"F0.wireOp",EDGE,"E9.7.3.0"),sQuery(id+"F0.wireOp",EDGE,"E9.11.3.0"),sQuery(id+"F0.wireOp",EDGE,"E9.14.3.0"),sQuery(id+"F0.wireOp",EDGE,"E9.1.4.0"),sQuery(id+"F0.wireOp",EDGE,"E9.3.4.0"),sQuery(id+"F0.wireOp",EDGE,"E9.7.4.0"),sQuery(id+"F0.wireOp",EDGE,"E9.11.4.0"),sQuery(id+"F0.wireOp",EDGE,"E9.14.4.0"),sQuery(id+"F0.wireOp",EDGE,"E9.1.5.0"),sQuery(id+"F0.wireOp",EDGE,"E9.3.5.0"),sQuery(id+"F0.wireOp",EDGE,"E9.7.5.0"),sQuery(id+"F0.wireOp",EDGE,"E9.11.5.0"),sQuery(id+"F0.wireOp",EDGE,"E9.14.5.0"),sQuery(id+"F0.wireOp",EDGE,"E9.1.6.0"),sQuery(id+"F0.wireOp",EDGE,"E9.3.6.0"),sQuery(id+"F0.wireOp",EDGE,"E9.7.6.0"),sQuery(id+"F0.wireOp",EDGE,"E9.11.6.0"),sQuery(id+"F0.wireOp",EDGE,"E9.14.6.0"),sQuery(id+"F0.wireOp",EDGE,"E9.1.7.0"),sQuery(id+"F0.wireOp",EDGE,"E9.3.7.0"),sQuery(id+"F0.wireOp",EDGE,"E9.7.7.0"),sQuery(id+"F0.wireOp",EDGE,"E9.11.7.0"),sQuery(id+"F0.wireOp",EDGE,"E9.14.7.0"),sQuery(id+"F0.wireOp",EDGE,"E9.1.8.0"),sQuery(id+"F0.wireOp",EDGE,"E9.3.8.0"),sQuery(id+"F0.wireOp",EDGE,"E9.7.8.0"),sQuery(id+"F0.wireOp",EDGE,"E9.11.8.0"),sQuery(id+"F0.wireOp",EDGE,"E9.14.8.0"),sQuery(id+"F0.wireOp",EDGE,"E9.1.9.0"),sQuery(id+"F0.wireOp",EDGE,"E9.3.9.0"),sQuery(id+"F0.wireOp",EDGE,"E9.7.9.0"),sQuery(id+"F0.wireOp",EDGE,"E9.11.9.0"),sQuery(id+"F0.wireOp",EDGE,"E9.14.9.0"),sQuery(id+"F0.wireOp",EDGE,"E9.1.10.0"),sQuery(id+"F0.wireOp",EDGE,"E9.3.10.0"),sQuery(id+"F0.wireOp",EDGE,"E9.7.10.0"),sQuery(id+"F0.wireOp",EDGE,"E9.11.10.0"),sQuery(id+"F0.wireOp",EDGE,"E9.14.10.0"),sQuery(id+"F0.wireOp",EDGE,"E9.1.11.0"),sQuery(id+"F0.wireOp",EDGE,"E9.3.11.0"),sQuery(id+"F0.wireOp",EDGE,"E9.7.11.0"),sQuery(id+"F0.wireOp",EDGE,"E9.11.11.0"),sQuery(id+"F0.wireOp",EDGE,"E9.14.11.0"),sQuery(id+"F0.wireOp",EDGE,"E9.1.12.0"),sQuery(id+"F0.wireOp",EDGE,"E9.3.12.0"),sQuery(id+"F0.wireOp",EDGE,"E9.7.12.0"),sQuery(id+"F0.wireOp",EDGE,"E9.11.12.0"),sQuery(id+"F0.wireOp",EDGE,"E9.14.12.0"),sQuery(id+"F0.wireOp",EDGE,"E9.1.13.0"),sQuery(id+"F0.wireOp",EDGE,"E9.3.13.0"),sQuery(id+"F0.wireOp",EDGE,"E9.7.13.0"),sQuery(id+"F0.wireOp",EDGE,"E9.11.13.0"),sQuery(id+"F0.wireOp",EDGE,"E9.14.13.0"),sQuery(id+"F0.wireOp",EDGE,"E9.1.14.0"),sQuery(id+"F0.wireOp",EDGE,"E9.3.14.0"),sQuery(id+"F0.wireOp",EDGE,"E9.7.14.0"),sQuery(id+"F0.wireOp",EDGE,"E9.11.14.0"),sQuery(id+"F0.wireOp",EDGE,"E9.14.14.0"),sQuery(id+"F0.wireOp",EDGE,"E9.1.15.0"),sQuery(id+"F0.wireOp",EDGE,"E9.3.15.0"),sQuery(id+"F0.wireOp",EDGE,"E9.7.15.0"),sQuery(id+"F0.wireOp",EDGE,"E9.11.15.0"),sQuery(id+"F0.wireOp",EDGE,"E9.14.15.0"),sQuery(id+"F0.wireOp",EDGE,"E9.1.16.0"),sQuery(id+"F0.wireOp",EDGE,"E9.3.16.0"),sQuery(id+"F0.wireOp",EDGE,"E9.7.16.0"),sQuery(id+"F0.wireOp",EDGE,"E9.11.16.0"),sQuery(id+"F0.wireOp",EDGE,"E9.14.16.0"),sQuery(id+"F0.wireOp",EDGE,"E9.1.17.0"),sQuery(id+"F0.wireOp",EDGE,"E9.3.17.0"),sQuery(id+"F0.wireOp",EDGE,"E9.7.17.0"),sQuery(id+"F0.wireOp",EDGE,"E9.11.17.0"),sQuery(id+"F0.wireOp",EDGE,"E9.14.17.0"),sQuery(id+"F0.wireOp",EDGE,"E9.1.18.0"),sQuery(id+"F0.wireOp",EDGE,"E9.3.18.0"),sQuery(id+"F0.wireOp",EDGE,"E9.7.18.0"),sQuery(id+"F0.wireOp",EDGE,"E9.11.18.0"),sQuery(id+"F0.wireOp",EDGE,"E9.14.18.0"),sQuery(id+"F0.wireOp",EDGE,"E9.1.19.0"),sQuery(id+"F0.wireOp",EDGE,"E9.3.19.0"),sQuery(id+"F0.wireOp",EDGE,"E9.7.19.0"),sQuery(id+"F0.wireOp",EDGE,"E9.11.19.0"),sQuery(id+"F0.wireOp",EDGE,"E9.14.19.0"),sQuery(id+"F0.wireOp",EDGE,"E9.1.20.0"),sQuery(id+"F0.wireOp",EDGE,"E9.3.20.0"),sQuery(id+"F0.wireOp",EDGE,"E9.7.20.0"),sQuery(id+"F0.wireOp",EDGE,"E9.11.20.0"),sQuery(id+"F0.wireOp",EDGE,"E9.14.20.0"),sQuery(id+"F0.wireOp",EDGE,"E9.1.21.0"),sQuery(id+"F0.wireOp",EDGE,"E9.3.21.0"),sQuery(id+"F0.wireOp",EDGE,"E9.7.21.0"),sQuery(id+"F0.wireOp",EDGE,"E9.11.21.0"),sQuery(id+"F0.wireOp",EDGE,"E9.14.21.0"),sQuery(id+"F0.wireOp",EDGE,"E9.1.22.0"),sQuery(id+"F0.wireOp",EDGE,"E9.3.22.0"),sQuery(id+"F0.wireOp",EDGE,"E9.7.22.0"),sQuery(id+"F0.wireOp",EDGE,"E9.11.22.0"),sQuery(id+"F0.wireOp",EDGE,"E9.14.22.0"),sQuery(id+"F0.wireOp",EDGE,"E9.1.23.0"),sQuery(id+"F0.wireOp",EDGE,"E9.3.23.0"),sQuery(id+"F0.wireOp",EDGE,"E9.7.23.0"),sQuery(id+"F0.wireOp",EDGE,"E9.11.23.0"),sQuery(id+"F0.wireOp",EDGE,"E9.14.23.0"),sQuery(id+"F0.wireOp",EDGE,"E9.1.24.0"),sQuery(id+"F0.wireOp",EDGE,"E9.3.24.0"),sQuery(id+"F0.wireOp",EDGE,"E9.7.24.0"),sQuery(id+"F0.wireOp",EDGE,"E9.11.24.0"),sQuery(id+"F0.wireOp",EDGE,"E9.14.24.0"),sQuery(id+"F0.wireOp",EDGE,"E9.1.25.0"),sQuery(id+"F0.wireOp",EDGE,"E9.3.25.0"),sQuery(id+"F0.wireOp",EDGE,"E9.7.25.0"),sQuery(id+"F0.wireOp",EDGE,"E9.11.25.0"),sQuery(id+"F0.wireOp",EDGE,"E9.14.25.0"),sQuery(id+"F0.wireOp",EDGE,"E9.1.26.0"),sQuery(id+"F0.wireOp",EDGE,"E9.3.26.0"),sQuery(id+"F0.wireOp",EDGE,"E9.7.26.0"),sQuery(id+"F0.wireOp",EDGE,"E9.11.26.0"),sQuery(id+"F0.wireOp",EDGE,"E9.14.26.0"),sQuery(id+"F0.wireOp",EDGE,"E9.1.27.0"),sQuery(id+"F0.wireOp",EDGE,"E9.3.27.0"),sQuery(id+"F0.wireOp",EDGE,"E9.7.27.0"),sQuery(id+"F0.wireOp",EDGE,"E9.11.27.0"),sQuery(id+"F0.wireOp",EDGE,"E9.14.27.0"),sQuery(id+"F0.wireOp",EDGE,"E9.1.28.0"),sQuery(id+"F0.wireOp",EDGE,"E9.3.28.0"),sQuery(id+"F0.wireOp",EDGE,"E9.7.28.0"),sQuery(id+"F0.wireOp",EDGE,"E9.11.28.0"),sQuery(id+"F0.wireOp",EDGE,"E9.14.28.0"),sQuery(id+"F0.wireOp",EDGE,"E9.1.29.0"),sQuery(id+"F0.wireOp",EDGE,"E9.3.29.0"),sQuery(id+"F0.wireOp",EDGE,"E9.7.29.0"),sQuery(id+"F0.wireOp",EDGE,"E9.11.29.0"),sQuery(id+"F0.wireOp",EDGE,"E9.14.29.0"),sQuery(id+"F0.wireOp",EDGE,"E9.1.30.0"),sQuery(id+"F0.wireOp",EDGE,"E9.3.30.0"),sQuery(id+"F0.wireOp",EDGE,"E9.7.30.0"),sQuery(id+"F0.wireOp",EDGE,"E9.11.30.0"),sQuery(id+"F0.wireOp",EDGE,"E9.14.30.0"),sQuery(id+"F0.wireOp",EDGE,"E9.1.31.0"),sQuery(id+"F0.wireOp",EDGE,"E9.3.31.0"),sQuery(id+"F0.wireOp",EDGE,"E9.7.31.0"),sQuery(id+"F0.wireOp",EDGE,"E9.11.31.0"),sQuery(id+"F0.wireOp",EDGE,"E9.14.31.0"),sQuery(id+"F0.wireOp",EDGE,"E9.1.32.0"),sQuery(id+"F0.wireOp",EDGE,"E9.3.32.0"),sQuery(id+"F0.wireOp",EDGE,"E9.7.32.0"),sQuery(id+"F0.wireOp",EDGE,"E9.11.32.0"),sQuery(id+"F0.wireOp",EDGE,"E9.14.32.0"),sQuery(id+"F0.wireOp",EDGE,"E9.1.33.0"),sQuery(id+"F0.wireOp",EDGE,"E9.3.33.0"),sQuery(id+"F0.wireOp",EDGE,"E9.7.33.0"),sQuery(id+"F0.wireOp",EDGE,"E9.11.33.0"),sQuery(id+"F0.wireOp",EDGE,"E9.14.33.0"),sQuery(id+"F0.wireOp",EDGE,"E9.1.34.0"),sQuery(id+"F0.wireOp",EDGE,"E9.3.34.0"),sQuery(id+"F0.wireOp",EDGE,"E9.7.34.0"),sQuery(id+"F0.wireOp",EDGE,"E9.11.34.0"),sQuery(id+"F0.wireOp",EDGE,"E9.14.34.0"),sQuery(id+"F0.wireOp",EDGE,"E9.1.35.0"),sQuery(id+"F0.wireOp",EDGE,"E9.3.35.0"),sQuery(id+"F0.wireOp",EDGE,"E9.7.35.0"),sQuery(id+"F0.wireOp",EDGE,"E9.11.35.0"),sQuery(id+"F0.wireOp",EDGE,"E9.14.35.0"),sQuery(id+"F0.wireOp",EDGE,"E9.1.36.0"),sQuery(id+"F0.wireOp",EDGE,"E9.3.36.0"),sQuery(id+"F0.wireOp",EDGE,"E9.7.36.0"),sQuery(id+"F0.wireOp",EDGE,"E9.11.36.0"),sQuery(id+"F0.wireOp",EDGE,"E9.14.36.0"),sQuery(id+"F0.wireOp",EDGE,"E9.1.37.0"),sQuery(id+"F0.wireOp",EDGE,"E9.3.37.0"),sQuery(id+"F0.wireOp",EDGE,"E9.7.37.0"),sQuery(id+"F0.wireOp",EDGE,"E9.11.37.0"),sQuery(id+"F0.wireOp",EDGE,"E9.14.37.0"),sQuery(id+"F0.wireOp",EDGE,"E9.1.38.0"),sQuery(id+"F0.wireOp",EDGE,"E9.3.38.0"),sQuery(id+"F0.wireOp",EDGE,"E9.7.38.0"),sQuery(id+"F0.wireOp",EDGE,"E9.11.38.0"),sQuery(id+"F0.wireOp",EDGE,"E9.14.38.0"),sQuery(id+"F0.wireOp",EDGE,"E9.1.39.0"),sQuery(id+"F0.wireOp",EDGE,"E9.3.39.0"),sQuery(id+"F0.wireOp",EDGE,"E9.7.39.0"),sQuery(id+"F0.wireOp",EDGE,"E9.11.39.0"),sQuery(id+"F0.wireOp",EDGE,"E9.14.39.0"),sQuery(id+"F0.wireOp",EDGE,"E9.1.40.0"),sQuery(id+"F0.wireOp",EDGE,"E9.3.40.0"),sQuery(id+"F0.wireOp",EDGE,"E9.7.40.0"),sQuery(id+"F0.wireOp",EDGE,"E9.11.40.0"),sQuery(id+"F0.wireOp",EDGE,"E9.14.40.0"),sQuery(id+"F0.wireOp",EDGE,"E9.1.41.0"),sQuery(id+"F0.wireOp",EDGE,"E9.3.41.0"),sQuery(id+"F0.wireOp",EDGE,"E9.7.41.0"),sQuery(id+"F0.wireOp",EDGE,"E9.11.41.0"),sQuery(id+"F0.wireOp",EDGE,"E9.14.41.0"),sQuery(id+"F0.wireOp",EDGE,"E9.1.42.0"),sQuery(id+"F0.wireOp",EDGE,"E9.3.42.0"),sQuery(id+"F0.wireOp",EDGE,"E9.7.42.0"),sQuery(id+"F0.wireOp",EDGE,"E9.11.42.0"),sQuery(id+"F0.wireOp",EDGE,"E9.14.42.0"),sQuery(id+"F0.wireOp",EDGE,"E9.1.43.0"),sQuery(id+"F0.wireOp",EDGE,"E9.3.43.0"),sQuery(id+"F0.wireOp",EDGE,"E9.7.43.0"),sQuery(id+"F0.wireOp",EDGE,"E9.11.43.0"),sQuery(id+"F0.wireOp",EDGE,"E9.14.43.0"),sQuery(id+"F0.wireOp",EDGE,"E9.1.44.0"),sQuery(id+"F0.wireOp",EDGE,"E9.3.44.0"),sQuery(id+"F0.wireOp",EDGE,"E9.7.44.0"),sQuery(id+"F0.wireOp",EDGE,"E9.11.44.0"),sQuery(id+"F0.wireOp",EDGE,"E9.14.44.0"),sQuery(id+"F0.wireOp",EDGE,"E9.1.45.0"),sQuery(id+"F0.wireOp",EDGE,"E9.3.45.0"),sQuery(id+"F0.wireOp",EDGE,"E9.7.45.0"),sQuery(id+"F0.wireOp",EDGE,"E9.11.45.0"),sQuery(id+"F0.wireOp",EDGE,"E9.14.45.0"),sQuery(id+"F0.wireOp",EDGE,"E9.1.46.0"),sQuery(id+"F0.wireOp",EDGE,"E9.3.46.0"),sQuery(id+"F0.wireOp",EDGE,"E9.7.46.0"),sQuery(id+"F0.wireOp",EDGE,"E9.11.46.0"),sQuery(id+"F0.wireOp",EDGE,"E9.14.46.0"),sQuery(id+"F0.wireOp",EDGE,"E9.1.47.0"),sQuery(id+"F0.wireOp",EDGE,"E9.3.47.0"),sQuery(id+"F0.wireOp",EDGE,"E9.7.47.0"),sQuery(id+"F0.wireOp",EDGE,"E9.11.47.0"),sQuery(id+"F0.wireOp",EDGE,"E9.14.47.0"),sQuery(id+"F0.wireOp",EDGE,"E9.1.48.0"),sQuery(id+"F0.wireOp",EDGE,"E9.3.48.0"),sQuery(id+"F0.wireOp",EDGE,"E9.7.48.0"),sQuery(id+"F0.wireOp",EDGE,"E9.11.48.0"),sQuery(id+"F0.wireOp",EDGE,"E9.14.48.0"),sQuery(id+"F0.wireOp",EDGE,"E9.1.49.0"),sQuery(id+"F0.wireOp",EDGE,"E9.3.49.0"),sQuery(id+"F0.wireOp",EDGE,"E9.7.49.0"),sQuery(id+"F0.wireOp",EDGE,"E9.11.49.0"),sQuery(id+"F0.wireOp",EDGE,"E9.14.49.0"),sQuery(id+"F0.wireOp",EDGE,"E9.1.50.0"),sQuery(id+"F0.wireOp",EDGE,"E9.3.50.0"),sQuery(id+"F0.wireOp",EDGE,"E9.7.50.0"),sQuery(id+"F0.wireOp",EDGE,"E9.11.50.0"),sQuery(id+"F0.wireOp",EDGE,"E9.14.50.0"),sQuery(id+"F0.wireOp",EDGE,"E9.1.51.0"),sQuery(id+"F0.wireOp",EDGE,"E9.3.51.0"),sQuery(id+"F0.wireOp",EDGE,"E9.7.51.0"),sQuery(id+"F0.wireOp",EDGE,"E9.11.51.0"),sQuery(id+"F0.wireOp",EDGE,"E9.14.51.0"),sQuery(id+"F0.wireOp",EDGE,"E9.1.52.0"),sQuery(id+"F0.wireOp",EDGE,"E9.3.52.0"),sQuery(id+"F0.wireOp",EDGE,"E9.7.52.0"),sQuery(id+"F0.wireOp",EDGE,"E9.11.52.0"),sQuery(id+"F0.wireOp",EDGE,"E9.14.52.0"),sQuery(id+"F0.wireOp",EDGE,"E9.1.53.0"),sQuery(id+"F0.wireOp",EDGE,"E9.3.53.0"),sQuery(id+"F0.wireOp",EDGE,"E9.7.53.0"),sQuery(id+"F0.wireOp",EDGE,"E9.11.53.0"),sQuery(id+"F0.wireOp",EDGE,"E9.14.53.0"),sQuery(id+"F0.wireOp",EDGE,"E9.1.54.0"),sQuery(id+"F0.wireOp",EDGE,"E9.3.54.0"),sQuery(id+"F0.wireOp",EDGE,"E9.7.54.0"),sQuery(id+"F0.wireOp",EDGE,"E9.11.54.0"),sQuery(id+"F0.wireOp",EDGE,"E9.14.54.0"),sQuery(id+"F0.wireOp",EDGE,"E9.1.55.0"),sQuery(id+"F0.wireOp",EDGE,"E9.3.55.0"),sQuery(id+"F0.wireOp",EDGE,"E9.7.55.0"),sQuery(id+"F0.wireOp",EDGE,"E9.11.55.0"),sQuery(id+"F0.wireOp",EDGE,"E9.14.55.0"),sQuery(id+"F0.wireOp",EDGE,"E9.1.56.0"),sQuery(id+"F0.wireOp",EDGE,"E9.3.56.0"),sQuery(id+"F0.wireOp",EDGE,"E9.7.56.0"),sQuery(id+"F0.wireOp",EDGE,"E9.11.56.0"),sQuery(id+"F0.wireOp",EDGE,"E9.14.56.0"),sQuery(id+"F0.wireOp",EDGE,"E9.1.57.0"),sQuery(id+"F0.wireOp",EDGE,"E9.3.57.0"),sQuery(id+"F0.wireOp",EDGE,"E9.7.57.0"),sQuery(id+"F0.wireOp",EDGE,"E9.11.57.0"),sQuery(id+"F0.wireOp",EDGE,"E9.14.57.0"),sQuery(id+"F0.wireOp",EDGE,"E9.1.58.0"),sQuery(id+"F0.wireOp",EDGE,"E9.3.58.0"),sQuery(id+"F0.wireOp",EDGE,"E9.7.58.0"),sQuery(id+"F0.wireOp",EDGE,"E9.11.58.0"),sQuery(id+"F0.wireOp",EDGE,"E9.14.58.0"),sQuery(id+"F0.wireOp",EDGE,"E9.1.59.0"),sQuery(id+"F0.wireOp",EDGE,"E9.3.59.0"),sQuery(id+"F0.wireOp",EDGE,"E9.7.59.0"),sQuery(id+"F0.wireOp",EDGE,"E9.11.59.0"),sQuery(id+"F0.wireOp",EDGE,"E9.14.59.0")])],"isStart":false})});
            extrude(context, id + "F5", {"entities" : qUnion([Q0]), "operationType" : NewBodyOperationType.REMOVE, "oppositeDirection" : true, "depth" : 1 * mm, "offsetDistance" : 25 * mm});
        }
        {
            var Q0;
            Q0=makeQuery(id+"F2.imprint","IMPRINT",FACE,{"disambiguationData":[TD([[makeQuery(id+"F2.imprint","IMPRINT",EDGE,{"derivedFrom":sQuery(id+"F2.wireOp",EDGE,"E19")}),1.0]])]});
            var Q1;
            Q1=makeQuery(id+"F2.imprint","IMPRINT",FACE,{"disambiguationData":[TD([[makeQuery(id+"F2.imprint","IMPRINT",EDGE,{"derivedFrom":sQuery(id+"F2.wireOp",EDGE,"E23")}),1.0]])]});
            var Q2;
            Q2=makeQuery(id+"F2.imprint","IMPRINT",FACE,{"disambiguationData":[TD([[makeQuery(id+"F2.imprint","IMPRINT",EDGE,{"derivedFrom":sQuery(id+"F2.wireOp",EDGE,"E22.0")}),-1.0]])]});
            var Q3;
            Q3=makeQuery(id+"F2.imprint","IMPRINT",FACE,{"disambiguationData":[TD([[makeQuery(id+"F2.imprint","IMPRINT",EDGE,{"derivedFrom":sQuery(id+"F2.wireOp",EDGE,"E20.0")}),-1.0]])]});
            extrude(context, id + "F6", {"entities" : qUnion([Q0, Q1, Q2, Q3]), "operationType" : NewBodyOperationType.REMOVE, "endBound" : BoundingType.THROUGH_ALL, "oppositeDirection" : true, "depth" : 25 * mm, "offsetDistance" : 25 * mm});
        }
        {
            var Q0;
            Q0=makeQuery(id+"F5.boolean.opBoolean","COPY",FACE,{"derivedFrom":makeQuery(id+"F5.opExtrude","CAP_FACE",FACE,{"disambiguationData":[OSD([sQuery(id+"F0.wireOp",EDGE,"E0"),sQuery(id+"F0.wireOp",EDGE,"E1"),sQuery(id+"F0.wireOp",EDGE,"E3"),sQuery(id+"F0.wireOp",EDGE,"E4"),sQuery(id+"F0.wireOp",EDGE,"E5"),sQuery(id+"F0.wireOp",EDGE,"E6.trimOffspring"),sQuery(id+"F0.wireOp",EDGE,"E7"),sQuery(id+"F0.wireOp",EDGE,"E8.1.0"),sQuery(id+"F0.wireOp",EDGE,"E8.1.1"),sQuery(id+"F0.wireOp",EDGE,"E8.1.2"),sQuery(id+"F0.wireOp",EDGE,"E8.1.3"),sQuery(id+"F0.wireOp",EDGE,"E8.1.4"),sQuery(id+"F0.wireOp",EDGE,"E8.2.0"),sQuery(id+"F0.wireOp",EDGE,"E8.2.1"),sQuery(id+"F0.wireOp",EDGE,"E8.2.2"),sQuery(id+"F0.wireOp",EDGE,"E8.2.3"),sQuery(id+"F0.wireOp",EDGE,"E8.2.4"),sQuery(id+"F0.wireOp",EDGE,"E9.1.3.0"),sQuery(id+"F0.wireOp",EDGE,"E9.3.3.0"),sQuery(id+"F0.wireOp",EDGE,"E9.7.3.0"),sQuery(id+"F0.wireOp",EDGE,"E9.11.3.0"),sQuery(id+"F0.wireOp",EDGE,"E9.14.3.0"),sQuery(id+"F0.wireOp",EDGE,"E9.1.4.0"),sQuery(id+"F0.wireOp",EDGE,"E9.3.4.0"),sQuery(id+"F0.wireOp",EDGE,"E9.7.4.0"),sQuery(id+"F0.wireOp",EDGE,"E9.11.4.0"),sQuery(id+"F0.wireOp",EDGE,"E9.14.4.0"),sQuery(id+"F0.wireOp",EDGE,"E9.1.5.0"),sQuery(id+"F0.wireOp",EDGE,"E9.3.5.0"),sQuery(id+"F0.wireOp",EDGE,"E9.7.5.0"),sQuery(id+"F0.wireOp",EDGE,"E9.11.5.0"),sQuery(id+"F0.wireOp",EDGE,"E9.14.5.0"),sQuery(id+"F0.wireOp",EDGE,"E9.1.6.0"),sQuery(id+"F0.wireOp",EDGE,"E9.3.6.0"),sQuery(id+"F0.wireOp",EDGE,"E9.7.6.0"),sQuery(id+"F0.wireOp",EDGE,"E9.11.6.0"),sQuery(id+"F0.wireOp",EDGE,"E9.14.6.0"),sQuery(id+"F0.wireOp",EDGE,"E9.1.7.0"),sQuery(id+"F0.wireOp",EDGE,"E9.3.7.0"),sQuery(id+"F0.wireOp",EDGE,"E9.7.7.0"),sQuery(id+"F0.wireOp",EDGE,"E9.11.7.0"),sQuery(id+"F0.wireOp",EDGE,"E9.14.7.0"),sQuery(id+"F0.wireOp",EDGE,"E9.1.8.0"),sQuery(id+"F0.wireOp",EDGE,"E9.3.8.0"),sQuery(id+"F0.wireOp",EDGE,"E9.7.8.0"),sQuery(id+"F0.wireOp",EDGE,"E9.11.8.0"),sQuery(id+"F0.wireOp",EDGE,"E9.14.8.0"),sQuery(id+"F0.wireOp",EDGE,"E9.1.9.0"),sQuery(id+"F0.wireOp",EDGE,"E9.3.9.0"),sQuery(id+"F0.wireOp",EDGE,"E9.7.9.0"),sQuery(id+"F0.wireOp",EDGE,"E9.11.9.0"),sQuery(id+"F0.wireOp",EDGE,"E9.14.9.0"),sQuery(id+"F0.wireOp",EDGE,"E9.1.10.0"),sQuery(id+"F0.wireOp",EDGE,"E9.3.10.0"),sQuery(id+"F0.wireOp",EDGE,"E9.7.10.0"),sQuery(id+"F0.wireOp",EDGE,"E9.11.10.0"),sQuery(id+"F0.wireOp",EDGE,"E9.14.10.0"),sQuery(id+"F0.wireOp",EDGE,"E9.1.11.0"),sQuery(id+"F0.wireOp",EDGE,"E9.3.11.0"),sQuery(id+"F0.wireOp",EDGE,"E9.7.11.0"),sQuery(id+"F0.wireOp",EDGE,"E9.11.11.0"),sQuery(id+"F0.wireOp",EDGE,"E9.14.11.0"),sQuery(id+"F0.wireOp",EDGE,"E9.1.12.0"),sQuery(id+"F0.wireOp",EDGE,"E9.3.12.0"),sQuery(id+"F0.wireOp",EDGE,"E9.7.12.0"),sQuery(id+"F0.wireOp",EDGE,"E9.11.12.0"),sQuery(id+"F0.wireOp",EDGE,"E9.14.12.0"),sQuery(id+"F0.wireOp",EDGE,"E9.1.13.0"),sQuery(id+"F0.wireOp",EDGE,"E9.3.13.0"),sQuery(id+"F0.wireOp",EDGE,"E9.7.13.0"),sQuery(id+"F0.wireOp",EDGE,"E9.11.13.0"),sQuery(id+"F0.wireOp",EDGE,"E9.14.13.0"),sQuery(id+"F0.wireOp",EDGE,"E9.1.14.0"),sQuery(id+"F0.wireOp",EDGE,"E9.3.14.0"),sQuery(id+"F0.wireOp",EDGE,"E9.7.14.0"),sQuery(id+"F0.wireOp",EDGE,"E9.11.14.0"),sQuery(id+"F0.wireOp",EDGE,"E9.14.14.0"),sQuery(id+"F0.wireOp",EDGE,"E9.1.15.0"),sQuery(id+"F0.wireOp",EDGE,"E9.3.15.0"),sQuery(id+"F0.wireOp",EDGE,"E9.7.15.0"),sQuery(id+"F0.wireOp",EDGE,"E9.11.15.0"),sQuery(id+"F0.wireOp",EDGE,"E9.14.15.0"),sQuery(id+"F0.wireOp",EDGE,"E9.1.16.0"),sQuery(id+"F0.wireOp",EDGE,"E9.3.16.0"),sQuery(id+"F0.wireOp",EDGE,"E9.7.16.0"),sQuery(id+"F0.wireOp",EDGE,"E9.11.16.0"),sQuery(id+"F0.wireOp",EDGE,"E9.14.16.0"),sQuery(id+"F0.wireOp",EDGE,"E9.1.17.0"),sQuery(id+"F0.wireOp",EDGE,"E9.3.17.0"),sQuery(id+"F0.wireOp",EDGE,"E9.7.17.0"),sQuery(id+"F0.wireOp",EDGE,"E9.11.17.0"),sQuery(id+"F0.wireOp",EDGE,"E9.14.17.0"),sQuery(id+"F0.wireOp",EDGE,"E9.1.18.0"),sQuery(id+"F0.wireOp",EDGE,"E9.3.18.0"),sQuery(id+"F0.wireOp",EDGE,"E9.7.18.0"),sQuery(id+"F0.wireOp",EDGE,"E9.11.18.0"),sQuery(id+"F0.wireOp",EDGE,"E9.14.18.0"),sQuery(id+"F0.wireOp",EDGE,"E9.1.19.0"),sQuery(id+"F0.wireOp",EDGE,"E9.3.19.0"),sQuery(id+"F0.wireOp",EDGE,"E9.7.19.0"),sQuery(id+"F0.wireOp",EDGE,"E9.11.19.0"),sQuery(id+"F0.wireOp",EDGE,"E9.14.19.0"),sQuery(id+"F0.wireOp",EDGE,"E9.1.20.0"),sQuery(id+"F0.wireOp",EDGE,"E9.3.20.0"),sQuery(id+"F0.wireOp",EDGE,"E9.7.20.0"),sQuery(id+"F0.wireOp",EDGE,"E9.11.20.0"),sQuery(id+"F0.wireOp",EDGE,"E9.14.20.0"),sQuery(id+"F0.wireOp",EDGE,"E9.1.21.0"),sQuery(id+"F0.wireOp",EDGE,"E9.3.21.0"),sQuery(id+"F0.wireOp",EDGE,"E9.7.21.0"),sQuery(id+"F0.wireOp",EDGE,"E9.11.21.0"),sQuery(id+"F0.wireOp",EDGE,"E9.14.21.0"),sQuery(id+"F0.wireOp",EDGE,"E9.1.22.0"),sQuery(id+"F0.wireOp",EDGE,"E9.3.22.0"),sQuery(id+"F0.wireOp",EDGE,"E9.7.22.0"),sQuery(id+"F0.wireOp",EDGE,"E9.11.22.0"),sQuery(id+"F0.wireOp",EDGE,"E9.14.22.0"),sQuery(id+"F0.wireOp",EDGE,"E9.1.23.0"),sQuery(id+"F0.wireOp",EDGE,"E9.3.23.0"),sQuery(id+"F0.wireOp",EDGE,"E9.7.23.0"),sQuery(id+"F0.wireOp",EDGE,"E9.11.23.0"),sQuery(id+"F0.wireOp",EDGE,"E9.14.23.0"),sQuery(id+"F0.wireOp",EDGE,"E9.1.24.0"),sQuery(id+"F0.wireOp",EDGE,"E9.3.24.0"),sQuery(id+"F0.wireOp",EDGE,"E9.7.24.0"),sQuery(id+"F0.wireOp",EDGE,"E9.11.24.0"),sQuery(id+"F0.wireOp",EDGE,"E9.14.24.0"),sQuery(id+"F0.wireOp",EDGE,"E9.1.25.0"),sQuery(id+"F0.wireOp",EDGE,"E9.3.25.0"),sQuery(id+"F0.wireOp",EDGE,"E9.7.25.0"),sQuery(id+"F0.wireOp",EDGE,"E9.11.25.0"),sQuery(id+"F0.wireOp",EDGE,"E9.14.25.0"),sQuery(id+"F0.wireOp",EDGE,"E9.1.26.0"),sQuery(id+"F0.wireOp",EDGE,"E9.3.26.0"),sQuery(id+"F0.wireOp",EDGE,"E9.7.26.0"),sQuery(id+"F0.wireOp",EDGE,"E9.11.26.0"),sQuery(id+"F0.wireOp",EDGE,"E9.14.26.0"),sQuery(id+"F0.wireOp",EDGE,"E9.1.27.0"),sQuery(id+"F0.wireOp",EDGE,"E9.3.27.0"),sQuery(id+"F0.wireOp",EDGE,"E9.7.27.0"),sQuery(id+"F0.wireOp",EDGE,"E9.11.27.0"),sQuery(id+"F0.wireOp",EDGE,"E9.14.27.0"),sQuery(id+"F0.wireOp",EDGE,"E9.1.28.0"),sQuery(id+"F0.wireOp",EDGE,"E9.3.28.0"),sQuery(id+"F0.wireOp",EDGE,"E9.7.28.0"),sQuery(id+"F0.wireOp",EDGE,"E9.11.28.0"),sQuery(id+"F0.wireOp",EDGE,"E9.14.28.0"),sQuery(id+"F0.wireOp",EDGE,"E9.1.29.0"),sQuery(id+"F0.wireOp",EDGE,"E9.3.29.0"),sQuery(id+"F0.wireOp",EDGE,"E9.7.29.0"),sQuery(id+"F0.wireOp",EDGE,"E9.11.29.0"),sQuery(id+"F0.wireOp",EDGE,"E9.14.29.0"),sQuery(id+"F0.wireOp",EDGE,"E9.1.30.0"),sQuery(id+"F0.wireOp",EDGE,"E9.3.30.0"),sQuery(id+"F0.wireOp",EDGE,"E9.7.30.0"),sQuery(id+"F0.wireOp",EDGE,"E9.11.30.0"),sQuery(id+"F0.wireOp",EDGE,"E9.14.30.0"),sQuery(id+"F0.wireOp",EDGE,"E9.1.31.0"),sQuery(id+"F0.wireOp",EDGE,"E9.3.31.0"),sQuery(id+"F0.wireOp",EDGE,"E9.7.31.0"),sQuery(id+"F0.wireOp",EDGE,"E9.11.31.0"),sQuery(id+"F0.wireOp",EDGE,"E9.14.31.0"),sQuery(id+"F0.wireOp",EDGE,"E9.1.32.0"),sQuery(id+"F0.wireOp",EDGE,"E9.3.32.0"),sQuery(id+"F0.wireOp",EDGE,"E9.7.32.0"),sQuery(id+"F0.wireOp",EDGE,"E9.11.32.0"),sQuery(id+"F0.wireOp",EDGE,"E9.14.32.0"),sQuery(id+"F0.wireOp",EDGE,"E9.1.33.0"),sQuery(id+"F0.wireOp",EDGE,"E9.3.33.0"),sQuery(id+"F0.wireOp",EDGE,"E9.7.33.0"),sQuery(id+"F0.wireOp",EDGE,"E9.11.33.0"),sQuery(id+"F0.wireOp",EDGE,"E9.14.33.0"),sQuery(id+"F0.wireOp",EDGE,"E9.1.34.0"),sQuery(id+"F0.wireOp",EDGE,"E9.3.34.0"),sQuery(id+"F0.wireOp",EDGE,"E9.7.34.0"),sQuery(id+"F0.wireOp",EDGE,"E9.11.34.0"),sQuery(id+"F0.wireOp",EDGE,"E9.14.34.0"),sQuery(id+"F0.wireOp",EDGE,"E9.1.35.0"),sQuery(id+"F0.wireOp",EDGE,"E9.3.35.0"),sQuery(id+"F0.wireOp",EDGE,"E9.7.35.0"),sQuery(id+"F0.wireOp",EDGE,"E9.11.35.0"),sQuery(id+"F0.wireOp",EDGE,"E9.14.35.0"),sQuery(id+"F0.wireOp",EDGE,"E9.1.36.0"),sQuery(id+"F0.wireOp",EDGE,"E9.3.36.0"),sQuery(id+"F0.wireOp",EDGE,"E9.7.36.0"),sQuery(id+"F0.wireOp",EDGE,"E9.11.36.0"),sQuery(id+"F0.wireOp",EDGE,"E9.14.36.0"),sQuery(id+"F0.wireOp",EDGE,"E9.1.37.0"),sQuery(id+"F0.wireOp",EDGE,"E9.3.37.0"),sQuery(id+"F0.wireOp",EDGE,"E9.7.37.0"),sQuery(id+"F0.wireOp",EDGE,"E9.11.37.0"),sQuery(id+"F0.wireOp",EDGE,"E9.14.37.0"),sQuery(id+"F0.wireOp",EDGE,"E9.1.38.0"),sQuery(id+"F0.wireOp",EDGE,"E9.3.38.0"),sQuery(id+"F0.wireOp",EDGE,"E9.7.38.0"),sQuery(id+"F0.wireOp",EDGE,"E9.11.38.0"),sQuery(id+"F0.wireOp",EDGE,"E9.14.38.0"),sQuery(id+"F0.wireOp",EDGE,"E9.1.39.0"),sQuery(id+"F0.wireOp",EDGE,"E9.3.39.0"),sQuery(id+"F0.wireOp",EDGE,"E9.7.39.0"),sQuery(id+"F0.wireOp",EDGE,"E9.11.39.0"),sQuery(id+"F0.wireOp",EDGE,"E9.14.39.0"),sQuery(id+"F0.wireOp",EDGE,"E9.1.40.0"),sQuery(id+"F0.wireOp",EDGE,"E9.3.40.0"),sQuery(id+"F0.wireOp",EDGE,"E9.7.40.0"),sQuery(id+"F0.wireOp",EDGE,"E9.11.40.0"),sQuery(id+"F0.wireOp",EDGE,"E9.14.40.0"),sQuery(id+"F0.wireOp",EDGE,"E9.1.41.0"),sQuery(id+"F0.wireOp",EDGE,"E9.3.41.0"),sQuery(id+"F0.wireOp",EDGE,"E9.7.41.0"),sQuery(id+"F0.wireOp",EDGE,"E9.11.41.0"),sQuery(id+"F0.wireOp",EDGE,"E9.14.41.0"),sQuery(id+"F0.wireOp",EDGE,"E9.1.42.0"),sQuery(id+"F0.wireOp",EDGE,"E9.3.42.0"),sQuery(id+"F0.wireOp",EDGE,"E9.7.42.0"),sQuery(id+"F0.wireOp",EDGE,"E9.11.42.0"),sQuery(id+"F0.wireOp",EDGE,"E9.14.42.0"),sQuery(id+"F0.wireOp",EDGE,"E9.1.43.0"),sQuery(id+"F0.wireOp",EDGE,"E9.3.43.0"),sQuery(id+"F0.wireOp",EDGE,"E9.7.43.0"),sQuery(id+"F0.wireOp",EDGE,"E9.11.43.0"),sQuery(id+"F0.wireOp",EDGE,"E9.14.43.0"),sQuery(id+"F0.wireOp",EDGE,"E9.1.44.0"),sQuery(id+"F0.wireOp",EDGE,"E9.3.44.0"),sQuery(id+"F0.wireOp",EDGE,"E9.7.44.0"),sQuery(id+"F0.wireOp",EDGE,"E9.11.44.0"),sQuery(id+"F0.wireOp",EDGE,"E9.14.44.0"),sQuery(id+"F0.wireOp",EDGE,"E9.1.45.0"),sQuery(id+"F0.wireOp",EDGE,"E9.3.45.0"),sQuery(id+"F0.wireOp",EDGE,"E9.7.45.0"),sQuery(id+"F0.wireOp",EDGE,"E9.11.45.0"),sQuery(id+"F0.wireOp",EDGE,"E9.14.45.0"),sQuery(id+"F0.wireOp",EDGE,"E9.1.46.0"),sQuery(id+"F0.wireOp",EDGE,"E9.3.46.0"),sQuery(id+"F0.wireOp",EDGE,"E9.7.46.0"),sQuery(id+"F0.wireOp",EDGE,"E9.11.46.0"),sQuery(id+"F0.wireOp",EDGE,"E9.14.46.0"),sQuery(id+"F0.wireOp",EDGE,"E9.1.47.0"),sQuery(id+"F0.wireOp",EDGE,"E9.3.47.0"),sQuery(id+"F0.wireOp",EDGE,"E9.7.47.0"),sQuery(id+"F0.wireOp",EDGE,"E9.11.47.0"),sQuery(id+"F0.wireOp",EDGE,"E9.14.47.0"),sQuery(id+"F0.wireOp",EDGE,"E9.1.48.0"),sQuery(id+"F0.wireOp",EDGE,"E9.3.48.0"),sQuery(id+"F0.wireOp",EDGE,"E9.7.48.0"),sQuery(id+"F0.wireOp",EDGE,"E9.11.48.0"),sQuery(id+"F0.wireOp",EDGE,"E9.14.48.0"),sQuery(id+"F0.wireOp",EDGE,"E9.1.49.0"),sQuery(id+"F0.wireOp",EDGE,"E9.3.49.0"),sQuery(id+"F0.wireOp",EDGE,"E9.7.49.0"),sQuery(id+"F0.wireOp",EDGE,"E9.11.49.0"),sQuery(id+"F0.wireOp",EDGE,"E9.14.49.0"),sQuery(id+"F0.wireOp",EDGE,"E9.1.50.0"),sQuery(id+"F0.wireOp",EDGE,"E9.3.50.0"),sQuery(id+"F0.wireOp",EDGE,"E9.7.50.0"),sQuery(id+"F0.wireOp",EDGE,"E9.11.50.0"),sQuery(id+"F0.wireOp",EDGE,"E9.14.50.0"),sQuery(id+"F0.wireOp",EDGE,"E9.1.51.0"),sQuery(id+"F0.wireOp",EDGE,"E9.3.51.0"),sQuery(id+"F0.wireOp",EDGE,"E9.7.51.0"),sQuery(id+"F0.wireOp",EDGE,"E9.11.51.0"),sQuery(id+"F0.wireOp",EDGE,"E9.14.51.0"),sQuery(id+"F0.wireOp",EDGE,"E9.1.52.0"),sQuery(id+"F0.wireOp",EDGE,"E9.3.52.0"),sQuery(id+"F0.wireOp",EDGE,"E9.7.52.0"),sQuery(id+"F0.wireOp",EDGE,"E9.11.52.0"),sQuery(id+"F0.wireOp",EDGE,"E9.14.52.0"),sQuery(id+"F0.wireOp",EDGE,"E9.1.53.0"),sQuery(id+"F0.wireOp",EDGE,"E9.3.53.0"),sQuery(id+"F0.wireOp",EDGE,"E9.7.53.0"),sQuery(id+"F0.wireOp",EDGE,"E9.11.53.0"),sQuery(id+"F0.wireOp",EDGE,"E9.14.53.0"),sQuery(id+"F0.wireOp",EDGE,"E9.1.54.0"),sQuery(id+"F0.wireOp",EDGE,"E9.3.54.0"),sQuery(id+"F0.wireOp",EDGE,"E9.7.54.0"),sQuery(id+"F0.wireOp",EDGE,"E9.11.54.0"),sQuery(id+"F0.wireOp",EDGE,"E9.14.54.0"),sQuery(id+"F0.wireOp",EDGE,"E9.1.55.0"),sQuery(id+"F0.wireOp",EDGE,"E9.3.55.0"),sQuery(id+"F0.wireOp",EDGE,"E9.7.55.0"),sQuery(id+"F0.wireOp",EDGE,"E9.11.55.0"),sQuery(id+"F0.wireOp",EDGE,"E9.14.55.0"),sQuery(id+"F0.wireOp",EDGE,"E9.1.56.0"),sQuery(id+"F0.wireOp",EDGE,"E9.3.56.0"),sQuery(id+"F0.wireOp",EDGE,"E9.7.56.0"),sQuery(id+"F0.wireOp",EDGE,"E9.11.56.0"),sQuery(id+"F0.wireOp",EDGE,"E9.14.56.0"),sQuery(id+"F0.wireOp",EDGE,"E9.1.57.0"),sQuery(id+"F0.wireOp",EDGE,"E9.3.57.0"),sQuery(id+"F0.wireOp",EDGE,"E9.7.57.0"),sQuery(id+"F0.wireOp",EDGE,"E9.11.57.0"),sQuery(id+"F0.wireOp",EDGE,"E9.14.57.0"),sQuery(id+"F0.wireOp",EDGE,"E9.1.58.0"),sQuery(id+"F0.wireOp",EDGE,"E9.3.58.0"),sQuery(id+"F0.wireOp",EDGE,"E9.7.58.0"),sQuery(id+"F0.wireOp",EDGE,"E9.11.58.0"),sQuery(id+"F0.wireOp",EDGE,"E9.14.58.0"),sQuery(id+"F0.wireOp",EDGE,"E9.1.59.0"),sQuery(id+"F0.wireOp",EDGE,"E9.3.59.0"),sQuery(id+"F0.wireOp",EDGE,"E9.7.59.0"),sQuery(id+"F0.wireOp",EDGE,"E9.11.59.0"),sQuery(id+"F0.wireOp",EDGE,"E9.14.59.0")])],"isStart":false})});
            var sketch = newSketch(context, id + "F7", { "sketchPlane" : qUnion([Q0])});
            skCircle(sketch, "E44", {"center": v(0, 0) * mm, "radius": 59 * mm});
            skCircle(sketch, "E45", {"center": v(0, 0) * mm, "radius": 64 * mm});
            skCircle(sketch, "E46", {"center": v(0, 0) * mm, "radius": 63 * mm});
            skCircle(sketch, "E47", {"center": v(0, 0) * mm, "radius": 10 * mm});
            skSolve(sketch);
        }
        {
            var Q0;
            Q0 = qSketchRegion(id + "F7", true);
            var Q1;
            Q1=makeQuery(id+"F7.imprint","IMPRINT",FACE,{"disambiguationData":[TD([[makeQuery(id+"F7.imprint","IMPRINT",EDGE,{"derivedFrom":sQuery(id+"F7.wireOp",EDGE,"E44")}),1.0]])]});
            extrude(context, id + "F8", {"entities" : qUnion([Q0, Q1]), "operationType" : NewBodyOperationType.REMOVE, "oppositeDirection" : true, "depth" : 1 * mm, "offsetDistance" : 25 * mm});
        }
        {
            var Q0;
            Q0=makeQuery(id+"F8.boolean.opBoolean","COPY",EDGE,{"derivedFrom":makeQuery(id+"F8.opExtrude","CAP_EDGE",EDGE,{"disambiguationData":[OSD([sQuery(id+"F0.wireOp",EDGE,"E0"),sQuery(id+"F0.wireOp",EDGE,"E1"),sQuery(id+"F0.wireOp",EDGE,"E3"),sQuery(id+"F0.wireOp",EDGE,"E4"),sQuery(id+"F0.wireOp",EDGE,"E5"),sQuery(id+"F0.wireOp",EDGE,"E6.trimOffspring"),sQuery(id+"F0.wireOp",EDGE,"E7"),sQuery(id+"F0.wireOp",EDGE,"E8.1.0"),sQuery(id+"F0.wireOp",EDGE,"E8.1.1"),sQuery(id+"F0.wireOp",EDGE,"E8.1.2"),sQuery(id+"F0.wireOp",EDGE,"E8.1.3"),sQuery(id+"F0.wireOp",EDGE,"E8.1.4"),sQuery(id+"F0.wireOp",EDGE,"E8.2.0"),sQuery(id+"F0.wireOp",EDGE,"E8.2.1"),sQuery(id+"F0.wireOp",EDGE,"E8.2.2"),sQuery(id+"F0.wireOp",EDGE,"E8.2.3"),sQuery(id+"F0.wireOp",EDGE,"E8.2.4"),sQuery(id+"F0.wireOp",EDGE,"E9.1.3.0"),sQuery(id+"F0.wireOp",EDGE,"E9.3.3.0"),sQuery(id+"F0.wireOp",EDGE,"E9.7.3.0"),sQuery(id+"F0.wireOp",EDGE,"E9.11.3.0"),sQuery(id+"F0.wireOp",EDGE,"E9.14.3.0"),sQuery(id+"F0.wireOp",EDGE,"E9.1.4.0"),sQuery(id+"F0.wireOp",EDGE,"E9.3.4.0"),sQuery(id+"F0.wireOp",EDGE,"E9.7.4.0"),sQuery(id+"F0.wireOp",EDGE,"E9.11.4.0"),sQuery(id+"F0.wireOp",EDGE,"E9.14.4.0"),sQuery(id+"F0.wireOp",EDGE,"E9.1.5.0"),sQuery(id+"F0.wireOp",EDGE,"E9.3.5.0"),sQuery(id+"F0.wireOp",EDGE,"E9.7.5.0"),sQuery(id+"F0.wireOp",EDGE,"E9.11.5.0"),sQuery(id+"F0.wireOp",EDGE,"E9.14.5.0"),sQuery(id+"F0.wireOp",EDGE,"E9.1.6.0"),sQuery(id+"F0.wireOp",EDGE,"E9.3.6.0"),sQuery(id+"F0.wireOp",EDGE,"E9.7.6.0"),sQuery(id+"F0.wireOp",EDGE,"E9.11.6.0"),sQuery(id+"F0.wireOp",EDGE,"E9.14.6.0"),sQuery(id+"F0.wireOp",EDGE,"E9.1.7.0"),sQuery(id+"F0.wireOp",EDGE,"E9.3.7.0"),sQuery(id+"F0.wireOp",EDGE,"E9.7.7.0"),sQuery(id+"F0.wireOp",EDGE,"E9.11.7.0"),sQuery(id+"F0.wireOp",EDGE,"E9.14.7.0"),sQuery(id+"F0.wireOp",EDGE,"E9.1.8.0"),sQuery(id+"F0.wireOp",EDGE,"E9.3.8.0"),sQuery(id+"F0.wireOp",EDGE,"E9.7.8.0"),sQuery(id+"F0.wireOp",EDGE,"E9.11.8.0"),sQuery(id+"F0.wireOp",EDGE,"E9.14.8.0"),sQuery(id+"F0.wireOp",EDGE,"E9.1.9.0"),sQuery(id+"F0.wireOp",EDGE,"E9.3.9.0"),sQuery(id+"F0.wireOp",EDGE,"E9.7.9.0"),sQuery(id+"F0.wireOp",EDGE,"E9.11.9.0"),sQuery(id+"F0.wireOp",EDGE,"E9.14.9.0"),sQuery(id+"F0.wireOp",EDGE,"E9.1.10.0"),sQuery(id+"F0.wireOp",EDGE,"E9.3.10.0"),sQuery(id+"F0.wireOp",EDGE,"E9.7.10.0"),sQuery(id+"F0.wireOp",EDGE,"E9.11.10.0"),sQuery(id+"F0.wireOp",EDGE,"E9.14.10.0"),sQuery(id+"F0.wireOp",EDGE,"E9.1.11.0"),sQuery(id+"F0.wireOp",EDGE,"E9.3.11.0"),sQuery(id+"F0.wireOp",EDGE,"E9.7.11.0"),sQuery(id+"F0.wireOp",EDGE,"E9.11.11.0"),sQuery(id+"F0.wireOp",EDGE,"E9.14.11.0"),sQuery(id+"F0.wireOp",EDGE,"E9.1.12.0"),sQuery(id+"F0.wireOp",EDGE,"E9.3.12.0"),sQuery(id+"F0.wireOp",EDGE,"E9.7.12.0"),sQuery(id+"F0.wireOp",EDGE,"E9.11.12.0"),sQuery(id+"F0.wireOp",EDGE,"E9.14.12.0"),sQuery(id+"F0.wireOp",EDGE,"E9.1.13.0"),sQuery(id+"F0.wireOp",EDGE,"E9.3.13.0"),sQuery(id+"F0.wireOp",EDGE,"E9.7.13.0"),sQuery(id+"F0.wireOp",EDGE,"E9.11.13.0"),sQuery(id+"F0.wireOp",EDGE,"E9.14.13.0"),sQuery(id+"F0.wireOp",EDGE,"E9.1.14.0"),sQuery(id+"F0.wireOp",EDGE,"E9.3.14.0"),sQuery(id+"F0.wireOp",EDGE,"E9.7.14.0"),sQuery(id+"F0.wireOp",EDGE,"E9.11.14.0"),sQuery(id+"F0.wireOp",EDGE,"E9.14.14.0"),sQuery(id+"F0.wireOp",EDGE,"E9.1.15.0"),sQuery(id+"F0.wireOp",EDGE,"E9.3.15.0"),sQuery(id+"F0.wireOp",EDGE,"E9.7.15.0"),sQuery(id+"F0.wireOp",EDGE,"E9.11.15.0"),sQuery(id+"F0.wireOp",EDGE,"E9.14.15.0"),sQuery(id+"F0.wireOp",EDGE,"E9.1.16.0"),sQuery(id+"F0.wireOp",EDGE,"E9.3.16.0"),sQuery(id+"F0.wireOp",EDGE,"E9.7.16.0"),sQuery(id+"F0.wireOp",EDGE,"E9.11.16.0"),sQuery(id+"F0.wireOp",EDGE,"E9.14.16.0"),sQuery(id+"F0.wireOp",EDGE,"E9.1.17.0"),sQuery(id+"F0.wireOp",EDGE,"E9.3.17.0"),sQuery(id+"F0.wireOp",EDGE,"E9.7.17.0"),sQuery(id+"F0.wireOp",EDGE,"E9.11.17.0"),sQuery(id+"F0.wireOp",EDGE,"E9.14.17.0"),sQuery(id+"F0.wireOp",EDGE,"E9.1.18.0"),sQuery(id+"F0.wireOp",EDGE,"E9.3.18.0"),sQuery(id+"F0.wireOp",EDGE,"E9.7.18.0"),sQuery(id+"F0.wireOp",EDGE,"E9.11.18.0"),sQuery(id+"F0.wireOp",EDGE,"E9.14.18.0"),sQuery(id+"F0.wireOp",EDGE,"E9.1.19.0"),sQuery(id+"F0.wireOp",EDGE,"E9.3.19.0"),sQuery(id+"F0.wireOp",EDGE,"E9.7.19.0"),sQuery(id+"F0.wireOp",EDGE,"E9.11.19.0"),sQuery(id+"F0.wireOp",EDGE,"E9.14.19.0"),sQuery(id+"F0.wireOp",EDGE,"E9.1.20.0"),sQuery(id+"F0.wireOp",EDGE,"E9.3.20.0"),sQuery(id+"F0.wireOp",EDGE,"E9.7.20.0"),sQuery(id+"F0.wireOp",EDGE,"E9.11.20.0"),sQuery(id+"F0.wireOp",EDGE,"E9.14.20.0"),sQuery(id+"F0.wireOp",EDGE,"E9.1.21.0"),sQuery(id+"F0.wireOp",EDGE,"E9.3.21.0"),sQuery(id+"F0.wireOp",EDGE,"E9.7.21.0"),sQuery(id+"F0.wireOp",EDGE,"E9.11.21.0"),sQuery(id+"F0.wireOp",EDGE,"E9.14.21.0"),sQuery(id+"F0.wireOp",EDGE,"E9.1.22.0"),sQuery(id+"F0.wireOp",EDGE,"E9.3.22.0"),sQuery(id+"F0.wireOp",EDGE,"E9.7.22.0"),sQuery(id+"F0.wireOp",EDGE,"E9.11.22.0"),sQuery(id+"F0.wireOp",EDGE,"E9.14.22.0"),sQuery(id+"F0.wireOp",EDGE,"E9.1.23.0"),sQuery(id+"F0.wireOp",EDGE,"E9.3.23.0"),sQuery(id+"F0.wireOp",EDGE,"E9.7.23.0"),sQuery(id+"F0.wireOp",EDGE,"E9.11.23.0"),sQuery(id+"F0.wireOp",EDGE,"E9.14.23.0"),sQuery(id+"F0.wireOp",EDGE,"E9.1.24.0"),sQuery(id+"F0.wireOp",EDGE,"E9.3.24.0"),sQuery(id+"F0.wireOp",EDGE,"E9.7.24.0"),sQuery(id+"F0.wireOp",EDGE,"E9.11.24.0"),sQuery(id+"F0.wireOp",EDGE,"E9.14.24.0"),sQuery(id+"F0.wireOp",EDGE,"E9.1.25.0"),sQuery(id+"F0.wireOp",EDGE,"E9.3.25.0"),sQuery(id+"F0.wireOp",EDGE,"E9.7.25.0"),sQuery(id+"F0.wireOp",EDGE,"E9.11.25.0"),sQuery(id+"F0.wireOp",EDGE,"E9.14.25.0"),sQuery(id+"F0.wireOp",EDGE,"E9.1.26.0"),sQuery(id+"F0.wireOp",EDGE,"E9.3.26.0"),sQuery(id+"F0.wireOp",EDGE,"E9.7.26.0"),sQuery(id+"F0.wireOp",EDGE,"E9.11.26.0"),sQuery(id+"F0.wireOp",EDGE,"E9.14.26.0"),sQuery(id+"F0.wireOp",EDGE,"E9.1.27.0"),sQuery(id+"F0.wireOp",EDGE,"E9.3.27.0"),sQuery(id+"F0.wireOp",EDGE,"E9.7.27.0"),sQuery(id+"F0.wireOp",EDGE,"E9.11.27.0"),sQuery(id+"F0.wireOp",EDGE,"E9.14.27.0"),sQuery(id+"F0.wireOp",EDGE,"E9.1.28.0"),sQuery(id+"F0.wireOp",EDGE,"E9.3.28.0"),sQuery(id+"F0.wireOp",EDGE,"E9.7.28.0"),sQuery(id+"F0.wireOp",EDGE,"E9.11.28.0"),sQuery(id+"F0.wireOp",EDGE,"E9.14.28.0"),sQuery(id+"F0.wireOp",EDGE,"E9.1.29.0"),sQuery(id+"F0.wireOp",EDGE,"E9.3.29.0"),sQuery(id+"F0.wireOp",EDGE,"E9.7.29.0"),sQuery(id+"F0.wireOp",EDGE,"E9.11.29.0"),sQuery(id+"F0.wireOp",EDGE,"E9.14.29.0"),sQuery(id+"F0.wireOp",EDGE,"E9.1.30.0"),sQuery(id+"F0.wireOp",EDGE,"E9.3.30.0"),sQuery(id+"F0.wireOp",EDGE,"E9.7.30.0"),sQuery(id+"F0.wireOp",EDGE,"E9.11.30.0"),sQuery(id+"F0.wireOp",EDGE,"E9.14.30.0"),sQuery(id+"F0.wireOp",EDGE,"E9.1.31.0"),sQuery(id+"F0.wireOp",EDGE,"E9.3.31.0"),sQuery(id+"F0.wireOp",EDGE,"E9.7.31.0"),sQuery(id+"F0.wireOp",EDGE,"E9.11.31.0"),sQuery(id+"F0.wireOp",EDGE,"E9.14.31.0"),sQuery(id+"F0.wireOp",EDGE,"E9.1.32.0"),sQuery(id+"F0.wireOp",EDGE,"E9.3.32.0"),sQuery(id+"F0.wireOp",EDGE,"E9.7.32.0"),sQuery(id+"F0.wireOp",EDGE,"E9.11.32.0"),sQuery(id+"F0.wireOp",EDGE,"E9.14.32.0"),sQuery(id+"F0.wireOp",EDGE,"E9.1.33.0"),sQuery(id+"F0.wireOp",EDGE,"E9.3.33.0"),sQuery(id+"F0.wireOp",EDGE,"E9.7.33.0"),sQuery(id+"F0.wireOp",EDGE,"E9.11.33.0"),sQuery(id+"F0.wireOp",EDGE,"E9.14.33.0"),sQuery(id+"F0.wireOp",EDGE,"E9.1.34.0"),sQuery(id+"F0.wireOp",EDGE,"E9.3.34.0"),sQuery(id+"F0.wireOp",EDGE,"E9.7.34.0"),sQuery(id+"F0.wireOp",EDGE,"E9.11.34.0"),sQuery(id+"F0.wireOp",EDGE,"E9.14.34.0"),sQuery(id+"F0.wireOp",EDGE,"E9.1.35.0"),sQuery(id+"F0.wireOp",EDGE,"E9.3.35.0"),sQuery(id+"F0.wireOp",EDGE,"E9.7.35.0"),sQuery(id+"F0.wireOp",EDGE,"E9.11.35.0"),sQuery(id+"F0.wireOp",EDGE,"E9.14.35.0"),sQuery(id+"F0.wireOp",EDGE,"E9.1.36.0"),sQuery(id+"F0.wireOp",EDGE,"E9.3.36.0"),sQuery(id+"F0.wireOp",EDGE,"E9.7.36.0"),sQuery(id+"F0.wireOp",EDGE,"E9.11.36.0"),sQuery(id+"F0.wireOp",EDGE,"E9.14.36.0"),sQuery(id+"F0.wireOp",EDGE,"E9.1.37.0"),sQuery(id+"F0.wireOp",EDGE,"E9.3.37.0"),sQuery(id+"F0.wireOp",EDGE,"E9.7.37.0"),sQuery(id+"F0.wireOp",EDGE,"E9.11.37.0"),sQuery(id+"F0.wireOp",EDGE,"E9.14.37.0"),sQuery(id+"F0.wireOp",EDGE,"E9.1.38.0"),sQuery(id+"F0.wireOp",EDGE,"E9.3.38.0"),sQuery(id+"F0.wireOp",EDGE,"E9.7.38.0"),sQuery(id+"F0.wireOp",EDGE,"E9.11.38.0"),sQuery(id+"F0.wireOp",EDGE,"E9.14.38.0"),sQuery(id+"F0.wireOp",EDGE,"E9.1.39.0"),sQuery(id+"F0.wireOp",EDGE,"E9.3.39.0"),sQuery(id+"F0.wireOp",EDGE,"E9.7.39.0"),sQuery(id+"F0.wireOp",EDGE,"E9.11.39.0"),sQuery(id+"F0.wireOp",EDGE,"E9.14.39.0"),sQuery(id+"F0.wireOp",EDGE,"E9.1.40.0"),sQuery(id+"F0.wireOp",EDGE,"E9.3.40.0"),sQuery(id+"F0.wireOp",EDGE,"E9.7.40.0"),sQuery(id+"F0.wireOp",EDGE,"E9.11.40.0"),sQuery(id+"F0.wireOp",EDGE,"E9.14.40.0"),sQuery(id+"F0.wireOp",EDGE,"E9.1.41.0"),sQuery(id+"F0.wireOp",EDGE,"E9.3.41.0"),sQuery(id+"F0.wireOp",EDGE,"E9.7.41.0"),sQuery(id+"F0.wireOp",EDGE,"E9.11.41.0"),sQuery(id+"F0.wireOp",EDGE,"E9.14.41.0"),sQuery(id+"F0.wireOp",EDGE,"E9.1.42.0"),sQuery(id+"F0.wireOp",EDGE,"E9.3.42.0"),sQuery(id+"F0.wireOp",EDGE,"E9.7.42.0"),sQuery(id+"F0.wireOp",EDGE,"E9.11.42.0"),sQuery(id+"F0.wireOp",EDGE,"E9.14.42.0"),sQuery(id+"F0.wireOp",EDGE,"E9.1.43.0"),sQuery(id+"F0.wireOp",EDGE,"E9.3.43.0"),sQuery(id+"F0.wireOp",EDGE,"E9.7.43.0"),sQuery(id+"F0.wireOp",EDGE,"E9.11.43.0"),sQuery(id+"F0.wireOp",EDGE,"E9.14.43.0"),sQuery(id+"F0.wireOp",EDGE,"E9.1.44.0"),sQuery(id+"F0.wireOp",EDGE,"E9.3.44.0"),sQuery(id+"F0.wireOp",EDGE,"E9.7.44.0"),sQuery(id+"F0.wireOp",EDGE,"E9.11.44.0"),sQuery(id+"F0.wireOp",EDGE,"E9.14.44.0"),sQuery(id+"F0.wireOp",EDGE,"E9.1.45.0"),sQuery(id+"F0.wireOp",EDGE,"E9.3.45.0"),sQuery(id+"F0.wireOp",EDGE,"E9.7.45.0"),sQuery(id+"F0.wireOp",EDGE,"E9.11.45.0"),sQuery(id+"F0.wireOp",EDGE,"E9.14.45.0"),sQuery(id+"F0.wireOp",EDGE,"E9.1.46.0"),sQuery(id+"F0.wireOp",EDGE,"E9.3.46.0"),sQuery(id+"F0.wireOp",EDGE,"E9.7.46.0"),sQuery(id+"F0.wireOp",EDGE,"E9.11.46.0"),sQuery(id+"F0.wireOp",EDGE,"E9.14.46.0"),sQuery(id+"F0.wireOp",EDGE,"E9.1.47.0"),sQuery(id+"F0.wireOp",EDGE,"E9.3.47.0"),sQuery(id+"F0.wireOp",EDGE,"E9.7.47.0"),sQuery(id+"F0.wireOp",EDGE,"E9.11.47.0"),sQuery(id+"F0.wireOp",EDGE,"E9.14.47.0"),sQuery(id+"F0.wireOp",EDGE,"E9.1.48.0"),sQuery(id+"F0.wireOp",EDGE,"E9.3.48.0"),sQuery(id+"F0.wireOp",EDGE,"E9.7.48.0"),sQuery(id+"F0.wireOp",EDGE,"E9.11.48.0"),sQuery(id+"F0.wireOp",EDGE,"E9.14.48.0"),sQuery(id+"F0.wireOp",EDGE,"E9.1.49.0"),sQuery(id+"F0.wireOp",EDGE,"E9.3.49.0"),sQuery(id+"F0.wireOp",EDGE,"E9.7.49.0"),sQuery(id+"F0.wireOp",EDGE,"E9.11.49.0"),sQuery(id+"F0.wireOp",EDGE,"E9.14.49.0"),sQuery(id+"F0.wireOp",EDGE,"E9.1.50.0"),sQuery(id+"F0.wireOp",EDGE,"E9.3.50.0"),sQuery(id+"F0.wireOp",EDGE,"E9.7.50.0"),sQuery(id+"F0.wireOp",EDGE,"E9.11.50.0"),sQuery(id+"F0.wireOp",EDGE,"E9.14.50.0"),sQuery(id+"F0.wireOp",EDGE,"E9.1.51.0"),sQuery(id+"F0.wireOp",EDGE,"E9.3.51.0"),sQuery(id+"F0.wireOp",EDGE,"E9.7.51.0"),sQuery(id+"F0.wireOp",EDGE,"E9.11.51.0"),sQuery(id+"F0.wireOp",EDGE,"E9.14.51.0"),sQuery(id+"F0.wireOp",EDGE,"E9.1.52.0"),sQuery(id+"F0.wireOp",EDGE,"E9.3.52.0"),sQuery(id+"F0.wireOp",EDGE,"E9.7.52.0"),sQuery(id+"F0.wireOp",EDGE,"E9.11.52.0"),sQuery(id+"F0.wireOp",EDGE,"E9.14.52.0"),sQuery(id+"F0.wireOp",EDGE,"E9.1.53.0"),sQuery(id+"F0.wireOp",EDGE,"E9.3.53.0"),sQuery(id+"F0.wireOp",EDGE,"E9.7.53.0"),sQuery(id+"F0.wireOp",EDGE,"E9.11.53.0"),sQuery(id+"F0.wireOp",EDGE,"E9.14.53.0"),sQuery(id+"F0.wireOp",EDGE,"E9.1.54.0"),sQuery(id+"F0.wireOp",EDGE,"E9.3.54.0"),sQuery(id+"F0.wireOp",EDGE,"E9.7.54.0"),sQuery(id+"F0.wireOp",EDGE,"E9.11.54.0"),sQuery(id+"F0.wireOp",EDGE,"E9.14.54.0"),sQuery(id+"F0.wireOp",EDGE,"E9.1.55.0"),sQuery(id+"F0.wireOp",EDGE,"E9.3.55.0"),sQuery(id+"F0.wireOp",EDGE,"E9.7.55.0"),sQuery(id+"F0.wireOp",EDGE,"E9.11.55.0"),sQuery(id+"F0.wireOp",EDGE,"E9.14.55.0"),sQuery(id+"F0.wireOp",EDGE,"E9.1.56.0"),sQuery(id+"F0.wireOp",EDGE,"E9.3.56.0"),sQuery(id+"F0.wireOp",EDGE,"E9.7.56.0"),sQuery(id+"F0.wireOp",EDGE,"E9.11.56.0"),sQuery(id+"F0.wireOp",EDGE,"E9.14.56.0"),sQuery(id+"F0.wireOp",EDGE,"E9.1.57.0"),sQuery(id+"F0.wireOp",EDGE,"E9.3.57.0"),sQuery(id+"F0.wireOp",EDGE,"E9.7.57.0"),sQuery(id+"F0.wireOp",EDGE,"E9.11.57.0"),sQuery(id+"F0.wireOp",EDGE,"E9.14.57.0"),sQuery(id+"F0.wireOp",EDGE,"E9.1.58.0"),sQuery(id+"F0.wireOp",EDGE,"E9.3.58.0"),sQuery(id+"F0.wireOp",EDGE,"E9.7.58.0"),sQuery(id+"F0.wireOp",EDGE,"E9.11.58.0"),sQuery(id+"F0.wireOp",EDGE,"E9.14.58.0"),sQuery(id+"F0.wireOp",EDGE,"E9.1.59.0"),sQuery(id+"F0.wireOp",EDGE,"E9.3.59.0"),sQuery(id+"F0.wireOp",EDGE,"E9.7.59.0"),sQuery(id+"F0.wireOp",EDGE,"E9.11.59.0"),sQuery(id+"F0.wireOp",EDGE,"E9.14.59.0"),sQuery(id+"F2.wireOp",EDGE,"E19")])],"isStart":false})});
            var Q1;
            Q1=makeQuery(id+"F8.boolean.opBoolean","COPY",EDGE,{"derivedFrom":makeQuery(id+"F8.opExtrude","CAP_EDGE",EDGE,{"disambiguationData":[OSD([sQuery(id+"F0.wireOp",EDGE,"E0"),sQuery(id+"F0.wireOp",EDGE,"E1"),sQuery(id+"F0.wireOp",EDGE,"E3"),sQuery(id+"F0.wireOp",EDGE,"E4"),sQuery(id+"F0.wireOp",EDGE,"E5"),sQuery(id+"F0.wireOp",EDGE,"E6.trimOffspring"),sQuery(id+"F0.wireOp",EDGE,"E7"),sQuery(id+"F0.wireOp",EDGE,"E8.1.0"),sQuery(id+"F0.wireOp",EDGE,"E8.1.1"),sQuery(id+"F0.wireOp",EDGE,"E8.1.2"),sQuery(id+"F0.wireOp",EDGE,"E8.1.3"),sQuery(id+"F0.wireOp",EDGE,"E8.1.4"),sQuery(id+"F0.wireOp",EDGE,"E8.2.0"),sQuery(id+"F0.wireOp",EDGE,"E8.2.1"),sQuery(id+"F0.wireOp",EDGE,"E8.2.2"),sQuery(id+"F0.wireOp",EDGE,"E8.2.3"),sQuery(id+"F0.wireOp",EDGE,"E8.2.4"),sQuery(id+"F0.wireOp",EDGE,"E9.1.3.0"),sQuery(id+"F0.wireOp",EDGE,"E9.3.3.0"),sQuery(id+"F0.wireOp",EDGE,"E9.7.3.0"),sQuery(id+"F0.wireOp",EDGE,"E9.11.3.0"),sQuery(id+"F0.wireOp",EDGE,"E9.14.3.0"),sQuery(id+"F0.wireOp",EDGE,"E9.1.4.0"),sQuery(id+"F0.wireOp",EDGE,"E9.3.4.0"),sQuery(id+"F0.wireOp",EDGE,"E9.7.4.0"),sQuery(id+"F0.wireOp",EDGE,"E9.11.4.0"),sQuery(id+"F0.wireOp",EDGE,"E9.14.4.0"),sQuery(id+"F0.wireOp",EDGE,"E9.1.5.0"),sQuery(id+"F0.wireOp",EDGE,"E9.3.5.0"),sQuery(id+"F0.wireOp",EDGE,"E9.7.5.0"),sQuery(id+"F0.wireOp",EDGE,"E9.11.5.0"),sQuery(id+"F0.wireOp",EDGE,"E9.14.5.0"),sQuery(id+"F0.wireOp",EDGE,"E9.1.6.0"),sQuery(id+"F0.wireOp",EDGE,"E9.3.6.0"),sQuery(id+"F0.wireOp",EDGE,"E9.7.6.0"),sQuery(id+"F0.wireOp",EDGE,"E9.11.6.0"),sQuery(id+"F0.wireOp",EDGE,"E9.14.6.0"),sQuery(id+"F0.wireOp",EDGE,"E9.1.7.0"),sQuery(id+"F0.wireOp",EDGE,"E9.3.7.0"),sQuery(id+"F0.wireOp",EDGE,"E9.7.7.0"),sQuery(id+"F0.wireOp",EDGE,"E9.11.7.0"),sQuery(id+"F0.wireOp",EDGE,"E9.14.7.0"),sQuery(id+"F0.wireOp",EDGE,"E9.1.8.0"),sQuery(id+"F0.wireOp",EDGE,"E9.3.8.0"),sQuery(id+"F0.wireOp",EDGE,"E9.7.8.0"),sQuery(id+"F0.wireOp",EDGE,"E9.11.8.0"),sQuery(id+"F0.wireOp",EDGE,"E9.14.8.0"),sQuery(id+"F0.wireOp",EDGE,"E9.1.9.0"),sQuery(id+"F0.wireOp",EDGE,"E9.3.9.0"),sQuery(id+"F0.wireOp",EDGE,"E9.7.9.0"),sQuery(id+"F0.wireOp",EDGE,"E9.11.9.0"),sQuery(id+"F0.wireOp",EDGE,"E9.14.9.0"),sQuery(id+"F0.wireOp",EDGE,"E9.1.10.0"),sQuery(id+"F0.wireOp",EDGE,"E9.3.10.0"),sQuery(id+"F0.wireOp",EDGE,"E9.7.10.0"),sQuery(id+"F0.wireOp",EDGE,"E9.11.10.0"),sQuery(id+"F0.wireOp",EDGE,"E9.14.10.0"),sQuery(id+"F0.wireOp",EDGE,"E9.1.11.0"),sQuery(id+"F0.wireOp",EDGE,"E9.3.11.0"),sQuery(id+"F0.wireOp",EDGE,"E9.7.11.0"),sQuery(id+"F0.wireOp",EDGE,"E9.11.11.0"),sQuery(id+"F0.wireOp",EDGE,"E9.14.11.0"),sQuery(id+"F0.wireOp",EDGE,"E9.1.12.0"),sQuery(id+"F0.wireOp",EDGE,"E9.3.12.0"),sQuery(id+"F0.wireOp",EDGE,"E9.7.12.0"),sQuery(id+"F0.wireOp",EDGE,"E9.11.12.0"),sQuery(id+"F0.wireOp",EDGE,"E9.14.12.0"),sQuery(id+"F0.wireOp",EDGE,"E9.1.13.0"),sQuery(id+"F0.wireOp",EDGE,"E9.3.13.0"),sQuery(id+"F0.wireOp",EDGE,"E9.7.13.0"),sQuery(id+"F0.wireOp",EDGE,"E9.11.13.0"),sQuery(id+"F0.wireOp",EDGE,"E9.14.13.0"),sQuery(id+"F0.wireOp",EDGE,"E9.1.14.0"),sQuery(id+"F0.wireOp",EDGE,"E9.3.14.0"),sQuery(id+"F0.wireOp",EDGE,"E9.7.14.0"),sQuery(id+"F0.wireOp",EDGE,"E9.11.14.0"),sQuery(id+"F0.wireOp",EDGE,"E9.14.14.0"),sQuery(id+"F0.wireOp",EDGE,"E9.1.15.0"),sQuery(id+"F0.wireOp",EDGE,"E9.3.15.0"),sQuery(id+"F0.wireOp",EDGE,"E9.7.15.0"),sQuery(id+"F0.wireOp",EDGE,"E9.11.15.0"),sQuery(id+"F0.wireOp",EDGE,"E9.14.15.0"),sQuery(id+"F0.wireOp",EDGE,"E9.1.16.0"),sQuery(id+"F0.wireOp",EDGE,"E9.3.16.0"),sQuery(id+"F0.wireOp",EDGE,"E9.7.16.0"),sQuery(id+"F0.wireOp",EDGE,"E9.11.16.0"),sQuery(id+"F0.wireOp",EDGE,"E9.14.16.0"),sQuery(id+"F0.wireOp",EDGE,"E9.1.17.0"),sQuery(id+"F0.wireOp",EDGE,"E9.3.17.0"),sQuery(id+"F0.wireOp",EDGE,"E9.7.17.0"),sQuery(id+"F0.wireOp",EDGE,"E9.11.17.0"),sQuery(id+"F0.wireOp",EDGE,"E9.14.17.0"),sQuery(id+"F0.wireOp",EDGE,"E9.1.18.0"),sQuery(id+"F0.wireOp",EDGE,"E9.3.18.0"),sQuery(id+"F0.wireOp",EDGE,"E9.7.18.0"),sQuery(id+"F0.wireOp",EDGE,"E9.11.18.0"),sQuery(id+"F0.wireOp",EDGE,"E9.14.18.0"),sQuery(id+"F0.wireOp",EDGE,"E9.1.19.0"),sQuery(id+"F0.wireOp",EDGE,"E9.3.19.0"),sQuery(id+"F0.wireOp",EDGE,"E9.7.19.0"),sQuery(id+"F0.wireOp",EDGE,"E9.11.19.0"),sQuery(id+"F0.wireOp",EDGE,"E9.14.19.0"),sQuery(id+"F0.wireOp",EDGE,"E9.1.20.0"),sQuery(id+"F0.wireOp",EDGE,"E9.3.20.0"),sQuery(id+"F0.wireOp",EDGE,"E9.7.20.0"),sQuery(id+"F0.wireOp",EDGE,"E9.11.20.0"),sQuery(id+"F0.wireOp",EDGE,"E9.14.20.0"),sQuery(id+"F0.wireOp",EDGE,"E9.1.21.0"),sQuery(id+"F0.wireOp",EDGE,"E9.3.21.0"),sQuery(id+"F0.wireOp",EDGE,"E9.7.21.0"),sQuery(id+"F0.wireOp",EDGE,"E9.11.21.0"),sQuery(id+"F0.wireOp",EDGE,"E9.14.21.0"),sQuery(id+"F0.wireOp",EDGE,"E9.1.22.0"),sQuery(id+"F0.wireOp",EDGE,"E9.3.22.0"),sQuery(id+"F0.wireOp",EDGE,"E9.7.22.0"),sQuery(id+"F0.wireOp",EDGE,"E9.11.22.0"),sQuery(id+"F0.wireOp",EDGE,"E9.14.22.0"),sQuery(id+"F0.wireOp",EDGE,"E9.1.23.0"),sQuery(id+"F0.wireOp",EDGE,"E9.3.23.0"),sQuery(id+"F0.wireOp",EDGE,"E9.7.23.0"),sQuery(id+"F0.wireOp",EDGE,"E9.11.23.0"),sQuery(id+"F0.wireOp",EDGE,"E9.14.23.0"),sQuery(id+"F0.wireOp",EDGE,"E9.1.24.0"),sQuery(id+"F0.wireOp",EDGE,"E9.3.24.0"),sQuery(id+"F0.wireOp",EDGE,"E9.7.24.0"),sQuery(id+"F0.wireOp",EDGE,"E9.11.24.0"),sQuery(id+"F0.wireOp",EDGE,"E9.14.24.0"),sQuery(id+"F0.wireOp",EDGE,"E9.1.25.0"),sQuery(id+"F0.wireOp",EDGE,"E9.3.25.0"),sQuery(id+"F0.wireOp",EDGE,"E9.7.25.0"),sQuery(id+"F0.wireOp",EDGE,"E9.11.25.0"),sQuery(id+"F0.wireOp",EDGE,"E9.14.25.0"),sQuery(id+"F0.wireOp",EDGE,"E9.1.26.0"),sQuery(id+"F0.wireOp",EDGE,"E9.3.26.0"),sQuery(id+"F0.wireOp",EDGE,"E9.7.26.0"),sQuery(id+"F0.wireOp",EDGE,"E9.11.26.0"),sQuery(id+"F0.wireOp",EDGE,"E9.14.26.0"),sQuery(id+"F0.wireOp",EDGE,"E9.1.27.0"),sQuery(id+"F0.wireOp",EDGE,"E9.3.27.0"),sQuery(id+"F0.wireOp",EDGE,"E9.7.27.0"),sQuery(id+"F0.wireOp",EDGE,"E9.11.27.0"),sQuery(id+"F0.wireOp",EDGE,"E9.14.27.0"),sQuery(id+"F0.wireOp",EDGE,"E9.1.28.0"),sQuery(id+"F0.wireOp",EDGE,"E9.3.28.0"),sQuery(id+"F0.wireOp",EDGE,"E9.7.28.0"),sQuery(id+"F0.wireOp",EDGE,"E9.11.28.0"),sQuery(id+"F0.wireOp",EDGE,"E9.14.28.0"),sQuery(id+"F0.wireOp",EDGE,"E9.1.29.0"),sQuery(id+"F0.wireOp",EDGE,"E9.3.29.0"),sQuery(id+"F0.wireOp",EDGE,"E9.7.29.0"),sQuery(id+"F0.wireOp",EDGE,"E9.11.29.0"),sQuery(id+"F0.wireOp",EDGE,"E9.14.29.0"),sQuery(id+"F0.wireOp",EDGE,"E9.1.30.0"),sQuery(id+"F0.wireOp",EDGE,"E9.3.30.0"),sQuery(id+"F0.wireOp",EDGE,"E9.7.30.0"),sQuery(id+"F0.wireOp",EDGE,"E9.11.30.0"),sQuery(id+"F0.wireOp",EDGE,"E9.14.30.0"),sQuery(id+"F0.wireOp",EDGE,"E9.1.31.0"),sQuery(id+"F0.wireOp",EDGE,"E9.3.31.0"),sQuery(id+"F0.wireOp",EDGE,"E9.7.31.0"),sQuery(id+"F0.wireOp",EDGE,"E9.11.31.0"),sQuery(id+"F0.wireOp",EDGE,"E9.14.31.0"),sQuery(id+"F0.wireOp",EDGE,"E9.1.32.0"),sQuery(id+"F0.wireOp",EDGE,"E9.3.32.0"),sQuery(id+"F0.wireOp",EDGE,"E9.7.32.0"),sQuery(id+"F0.wireOp",EDGE,"E9.11.32.0"),sQuery(id+"F0.wireOp",EDGE,"E9.14.32.0"),sQuery(id+"F0.wireOp",EDGE,"E9.1.33.0"),sQuery(id+"F0.wireOp",EDGE,"E9.3.33.0"),sQuery(id+"F0.wireOp",EDGE,"E9.7.33.0"),sQuery(id+"F0.wireOp",EDGE,"E9.11.33.0"),sQuery(id+"F0.wireOp",EDGE,"E9.14.33.0"),sQuery(id+"F0.wireOp",EDGE,"E9.1.34.0"),sQuery(id+"F0.wireOp",EDGE,"E9.3.34.0"),sQuery(id+"F0.wireOp",EDGE,"E9.7.34.0"),sQuery(id+"F0.wireOp",EDGE,"E9.11.34.0"),sQuery(id+"F0.wireOp",EDGE,"E9.14.34.0"),sQuery(id+"F0.wireOp",EDGE,"E9.1.35.0"),sQuery(id+"F0.wireOp",EDGE,"E9.3.35.0"),sQuery(id+"F0.wireOp",EDGE,"E9.7.35.0"),sQuery(id+"F0.wireOp",EDGE,"E9.11.35.0"),sQuery(id+"F0.wireOp",EDGE,"E9.14.35.0"),sQuery(id+"F0.wireOp",EDGE,"E9.1.36.0"),sQuery(id+"F0.wireOp",EDGE,"E9.3.36.0"),sQuery(id+"F0.wireOp",EDGE,"E9.7.36.0"),sQuery(id+"F0.wireOp",EDGE,"E9.11.36.0"),sQuery(id+"F0.wireOp",EDGE,"E9.14.36.0"),sQuery(id+"F0.wireOp",EDGE,"E9.1.37.0"),sQuery(id+"F0.wireOp",EDGE,"E9.3.37.0"),sQuery(id+"F0.wireOp",EDGE,"E9.7.37.0"),sQuery(id+"F0.wireOp",EDGE,"E9.11.37.0"),sQuery(id+"F0.wireOp",EDGE,"E9.14.37.0"),sQuery(id+"F0.wireOp",EDGE,"E9.1.38.0"),sQuery(id+"F0.wireOp",EDGE,"E9.3.38.0"),sQuery(id+"F0.wireOp",EDGE,"E9.7.38.0"),sQuery(id+"F0.wireOp",EDGE,"E9.11.38.0"),sQuery(id+"F0.wireOp",EDGE,"E9.14.38.0"),sQuery(id+"F0.wireOp",EDGE,"E9.1.39.0"),sQuery(id+"F0.wireOp",EDGE,"E9.3.39.0"),sQuery(id+"F0.wireOp",EDGE,"E9.7.39.0"),sQuery(id+"F0.wireOp",EDGE,"E9.11.39.0"),sQuery(id+"F0.wireOp",EDGE,"E9.14.39.0"),sQuery(id+"F0.wireOp",EDGE,"E9.1.40.0"),sQuery(id+"F0.wireOp",EDGE,"E9.3.40.0"),sQuery(id+"F0.wireOp",EDGE,"E9.7.40.0"),sQuery(id+"F0.wireOp",EDGE,"E9.11.40.0"),sQuery(id+"F0.wireOp",EDGE,"E9.14.40.0"),sQuery(id+"F0.wireOp",EDGE,"E9.1.41.0"),sQuery(id+"F0.wireOp",EDGE,"E9.3.41.0"),sQuery(id+"F0.wireOp",EDGE,"E9.7.41.0"),sQuery(id+"F0.wireOp",EDGE,"E9.11.41.0"),sQuery(id+"F0.wireOp",EDGE,"E9.14.41.0"),sQuery(id+"F0.wireOp",EDGE,"E9.1.42.0"),sQuery(id+"F0.wireOp",EDGE,"E9.3.42.0"),sQuery(id+"F0.wireOp",EDGE,"E9.7.42.0"),sQuery(id+"F0.wireOp",EDGE,"E9.11.42.0"),sQuery(id+"F0.wireOp",EDGE,"E9.14.42.0"),sQuery(id+"F0.wireOp",EDGE,"E9.1.43.0"),sQuery(id+"F0.wireOp",EDGE,"E9.3.43.0"),sQuery(id+"F0.wireOp",EDGE,"E9.7.43.0"),sQuery(id+"F0.wireOp",EDGE,"E9.11.43.0"),sQuery(id+"F0.wireOp",EDGE,"E9.14.43.0"),sQuery(id+"F0.wireOp",EDGE,"E9.1.44.0"),sQuery(id+"F0.wireOp",EDGE,"E9.3.44.0"),sQuery(id+"F0.wireOp",EDGE,"E9.7.44.0"),sQuery(id+"F0.wireOp",EDGE,"E9.11.44.0"),sQuery(id+"F0.wireOp",EDGE,"E9.14.44.0"),sQuery(id+"F0.wireOp",EDGE,"E9.1.45.0"),sQuery(id+"F0.wireOp",EDGE,"E9.3.45.0"),sQuery(id+"F0.wireOp",EDGE,"E9.7.45.0"),sQuery(id+"F0.wireOp",EDGE,"E9.11.45.0"),sQuery(id+"F0.wireOp",EDGE,"E9.14.45.0"),sQuery(id+"F0.wireOp",EDGE,"E9.1.46.0"),sQuery(id+"F0.wireOp",EDGE,"E9.3.46.0"),sQuery(id+"F0.wireOp",EDGE,"E9.7.46.0"),sQuery(id+"F0.wireOp",EDGE,"E9.11.46.0"),sQuery(id+"F0.wireOp",EDGE,"E9.14.46.0"),sQuery(id+"F0.wireOp",EDGE,"E9.1.47.0"),sQuery(id+"F0.wireOp",EDGE,"E9.3.47.0"),sQuery(id+"F0.wireOp",EDGE,"E9.7.47.0"),sQuery(id+"F0.wireOp",EDGE,"E9.11.47.0"),sQuery(id+"F0.wireOp",EDGE,"E9.14.47.0"),sQuery(id+"F0.wireOp",EDGE,"E9.1.48.0"),sQuery(id+"F0.wireOp",EDGE,"E9.3.48.0"),sQuery(id+"F0.wireOp",EDGE,"E9.7.48.0"),sQuery(id+"F0.wireOp",EDGE,"E9.11.48.0"),sQuery(id+"F0.wireOp",EDGE,"E9.14.48.0"),sQuery(id+"F0.wireOp",EDGE,"E9.1.49.0"),sQuery(id+"F0.wireOp",EDGE,"E9.3.49.0"),sQuery(id+"F0.wireOp",EDGE,"E9.7.49.0"),sQuery(id+"F0.wireOp",EDGE,"E9.11.49.0"),sQuery(id+"F0.wireOp",EDGE,"E9.14.49.0"),sQuery(id+"F0.wireOp",EDGE,"E9.1.50.0"),sQuery(id+"F0.wireOp",EDGE,"E9.3.50.0"),sQuery(id+"F0.wireOp",EDGE,"E9.7.50.0"),sQuery(id+"F0.wireOp",EDGE,"E9.11.50.0"),sQuery(id+"F0.wireOp",EDGE,"E9.14.50.0"),sQuery(id+"F0.wireOp",EDGE,"E9.1.51.0"),sQuery(id+"F0.wireOp",EDGE,"E9.3.51.0"),sQuery(id+"F0.wireOp",EDGE,"E9.7.51.0"),sQuery(id+"F0.wireOp",EDGE,"E9.11.51.0"),sQuery(id+"F0.wireOp",EDGE,"E9.14.51.0"),sQuery(id+"F0.wireOp",EDGE,"E9.1.52.0"),sQuery(id+"F0.wireOp",EDGE,"E9.3.52.0"),sQuery(id+"F0.wireOp",EDGE,"E9.7.52.0"),sQuery(id+"F0.wireOp",EDGE,"E9.11.52.0"),sQuery(id+"F0.wireOp",EDGE,"E9.14.52.0"),sQuery(id+"F0.wireOp",EDGE,"E9.1.53.0"),sQuery(id+"F0.wireOp",EDGE,"E9.3.53.0"),sQuery(id+"F0.wireOp",EDGE,"E9.7.53.0"),sQuery(id+"F0.wireOp",EDGE,"E9.11.53.0"),sQuery(id+"F0.wireOp",EDGE,"E9.14.53.0"),sQuery(id+"F0.wireOp",EDGE,"E9.1.54.0"),sQuery(id+"F0.wireOp",EDGE,"E9.3.54.0"),sQuery(id+"F0.wireOp",EDGE,"E9.7.54.0"),sQuery(id+"F0.wireOp",EDGE,"E9.11.54.0"),sQuery(id+"F0.wireOp",EDGE,"E9.14.54.0"),sQuery(id+"F0.wireOp",EDGE,"E9.1.55.0"),sQuery(id+"F0.wireOp",EDGE,"E9.3.55.0"),sQuery(id+"F0.wireOp",EDGE,"E9.7.55.0"),sQuery(id+"F0.wireOp",EDGE,"E9.11.55.0"),sQuery(id+"F0.wireOp",EDGE,"E9.14.55.0"),sQuery(id+"F0.wireOp",EDGE,"E9.1.56.0"),sQuery(id+"F0.wireOp",EDGE,"E9.3.56.0"),sQuery(id+"F0.wireOp",EDGE,"E9.7.56.0"),sQuery(id+"F0.wireOp",EDGE,"E9.11.56.0"),sQuery(id+"F0.wireOp",EDGE,"E9.14.56.0"),sQuery(id+"F0.wireOp",EDGE,"E9.1.57.0"),sQuery(id+"F0.wireOp",EDGE,"E9.3.57.0"),sQuery(id+"F0.wireOp",EDGE,"E9.7.57.0"),sQuery(id+"F0.wireOp",EDGE,"E9.11.57.0"),sQuery(id+"F0.wireOp",EDGE,"E9.14.57.0"),sQuery(id+"F0.wireOp",EDGE,"E9.1.58.0"),sQuery(id+"F0.wireOp",EDGE,"E9.3.58.0"),sQuery(id+"F0.wireOp",EDGE,"E9.7.58.0"),sQuery(id+"F0.wireOp",EDGE,"E9.11.58.0"),sQuery(id+"F0.wireOp",EDGE,"E9.14.58.0"),sQuery(id+"F0.wireOp",EDGE,"E9.1.59.0"),sQuery(id+"F0.wireOp",EDGE,"E9.3.59.0"),sQuery(id+"F0.wireOp",EDGE,"E9.7.59.0"),sQuery(id+"F0.wireOp",EDGE,"E9.11.59.0"),sQuery(id+"F0.wireOp",EDGE,"E9.14.59.0"),sQuery(id+"F2.wireOp",EDGE,"E35.trimOffspring")])],"isStart":false})});
            var Q2;
            Q2=makeQuery(id+"F8.boolean.opBoolean","COPY",EDGE,{"derivedFrom":makeQuery(id+"F8.opExtrude","CAP_EDGE",EDGE,{"disambiguationData":[OSD([sQuery(id+"F0.wireOp",EDGE,"E0"),sQuery(id+"F0.wireOp",EDGE,"E1"),sQuery(id+"F0.wireOp",EDGE,"E3"),sQuery(id+"F0.wireOp",EDGE,"E4"),sQuery(id+"F0.wireOp",EDGE,"E5"),sQuery(id+"F0.wireOp",EDGE,"E6.trimOffspring"),sQuery(id+"F0.wireOp",EDGE,"E7"),sQuery(id+"F0.wireOp",EDGE,"E8.1.0"),sQuery(id+"F0.wireOp",EDGE,"E8.1.1"),sQuery(id+"F0.wireOp",EDGE,"E8.1.2"),sQuery(id+"F0.wireOp",EDGE,"E8.1.3"),sQuery(id+"F0.wireOp",EDGE,"E8.1.4"),sQuery(id+"F0.wireOp",EDGE,"E8.2.0"),sQuery(id+"F0.wireOp",EDGE,"E8.2.1"),sQuery(id+"F0.wireOp",EDGE,"E8.2.2"),sQuery(id+"F0.wireOp",EDGE,"E8.2.3"),sQuery(id+"F0.wireOp",EDGE,"E8.2.4"),sQuery(id+"F0.wireOp",EDGE,"E9.1.3.0"),sQuery(id+"F0.wireOp",EDGE,"E9.3.3.0"),sQuery(id+"F0.wireOp",EDGE,"E9.7.3.0"),sQuery(id+"F0.wireOp",EDGE,"E9.11.3.0"),sQuery(id+"F0.wireOp",EDGE,"E9.14.3.0"),sQuery(id+"F0.wireOp",EDGE,"E9.1.4.0"),sQuery(id+"F0.wireOp",EDGE,"E9.3.4.0"),sQuery(id+"F0.wireOp",EDGE,"E9.7.4.0"),sQuery(id+"F0.wireOp",EDGE,"E9.11.4.0"),sQuery(id+"F0.wireOp",EDGE,"E9.14.4.0"),sQuery(id+"F0.wireOp",EDGE,"E9.1.5.0"),sQuery(id+"F0.wireOp",EDGE,"E9.3.5.0"),sQuery(id+"F0.wireOp",EDGE,"E9.7.5.0"),sQuery(id+"F0.wireOp",EDGE,"E9.11.5.0"),sQuery(id+"F0.wireOp",EDGE,"E9.14.5.0"),sQuery(id+"F0.wireOp",EDGE,"E9.1.6.0"),sQuery(id+"F0.wireOp",EDGE,"E9.3.6.0"),sQuery(id+"F0.wireOp",EDGE,"E9.7.6.0"),sQuery(id+"F0.wireOp",EDGE,"E9.11.6.0"),sQuery(id+"F0.wireOp",EDGE,"E9.14.6.0"),sQuery(id+"F0.wireOp",EDGE,"E9.1.7.0"),sQuery(id+"F0.wireOp",EDGE,"E9.3.7.0"),sQuery(id+"F0.wireOp",EDGE,"E9.7.7.0"),sQuery(id+"F0.wireOp",EDGE,"E9.11.7.0"),sQuery(id+"F0.wireOp",EDGE,"E9.14.7.0"),sQuery(id+"F0.wireOp",EDGE,"E9.1.8.0"),sQuery(id+"F0.wireOp",EDGE,"E9.3.8.0"),sQuery(id+"F0.wireOp",EDGE,"E9.7.8.0"),sQuery(id+"F0.wireOp",EDGE,"E9.11.8.0"),sQuery(id+"F0.wireOp",EDGE,"E9.14.8.0"),sQuery(id+"F0.wireOp",EDGE,"E9.1.9.0"),sQuery(id+"F0.wireOp",EDGE,"E9.3.9.0"),sQuery(id+"F0.wireOp",EDGE,"E9.7.9.0"),sQuery(id+"F0.wireOp",EDGE,"E9.11.9.0"),sQuery(id+"F0.wireOp",EDGE,"E9.14.9.0"),sQuery(id+"F0.wireOp",EDGE,"E9.1.10.0"),sQuery(id+"F0.wireOp",EDGE,"E9.3.10.0"),sQuery(id+"F0.wireOp",EDGE,"E9.7.10.0"),sQuery(id+"F0.wireOp",EDGE,"E9.11.10.0"),sQuery(id+"F0.wireOp",EDGE,"E9.14.10.0"),sQuery(id+"F0.wireOp",EDGE,"E9.1.11.0"),sQuery(id+"F0.wireOp",EDGE,"E9.3.11.0"),sQuery(id+"F0.wireOp",EDGE,"E9.7.11.0"),sQuery(id+"F0.wireOp",EDGE,"E9.11.11.0"),sQuery(id+"F0.wireOp",EDGE,"E9.14.11.0"),sQuery(id+"F0.wireOp",EDGE,"E9.1.12.0"),sQuery(id+"F0.wireOp",EDGE,"E9.3.12.0"),sQuery(id+"F0.wireOp",EDGE,"E9.7.12.0"),sQuery(id+"F0.wireOp",EDGE,"E9.11.12.0"),sQuery(id+"F0.wireOp",EDGE,"E9.14.12.0"),sQuery(id+"F0.wireOp",EDGE,"E9.1.13.0"),sQuery(id+"F0.wireOp",EDGE,"E9.3.13.0"),sQuery(id+"F0.wireOp",EDGE,"E9.7.13.0"),sQuery(id+"F0.wireOp",EDGE,"E9.11.13.0"),sQuery(id+"F0.wireOp",EDGE,"E9.14.13.0"),sQuery(id+"F0.wireOp",EDGE,"E9.1.14.0"),sQuery(id+"F0.wireOp",EDGE,"E9.3.14.0"),sQuery(id+"F0.wireOp",EDGE,"E9.7.14.0"),sQuery(id+"F0.wireOp",EDGE,"E9.11.14.0"),sQuery(id+"F0.wireOp",EDGE,"E9.14.14.0"),sQuery(id+"F0.wireOp",EDGE,"E9.1.15.0"),sQuery(id+"F0.wireOp",EDGE,"E9.3.15.0"),sQuery(id+"F0.wireOp",EDGE,"E9.7.15.0"),sQuery(id+"F0.wireOp",EDGE,"E9.11.15.0"),sQuery(id+"F0.wireOp",EDGE,"E9.14.15.0"),sQuery(id+"F0.wireOp",EDGE,"E9.1.16.0"),sQuery(id+"F0.wireOp",EDGE,"E9.3.16.0"),sQuery(id+"F0.wireOp",EDGE,"E9.7.16.0"),sQuery(id+"F0.wireOp",EDGE,"E9.11.16.0"),sQuery(id+"F0.wireOp",EDGE,"E9.14.16.0"),sQuery(id+"F0.wireOp",EDGE,"E9.1.17.0"),sQuery(id+"F0.wireOp",EDGE,"E9.3.17.0"),sQuery(id+"F0.wireOp",EDGE,"E9.7.17.0"),sQuery(id+"F0.wireOp",EDGE,"E9.11.17.0"),sQuery(id+"F0.wireOp",EDGE,"E9.14.17.0"),sQuery(id+"F0.wireOp",EDGE,"E9.1.18.0"),sQuery(id+"F0.wireOp",EDGE,"E9.3.18.0"),sQuery(id+"F0.wireOp",EDGE,"E9.7.18.0"),sQuery(id+"F0.wireOp",EDGE,"E9.11.18.0"),sQuery(id+"F0.wireOp",EDGE,"E9.14.18.0"),sQuery(id+"F0.wireOp",EDGE,"E9.1.19.0"),sQuery(id+"F0.wireOp",EDGE,"E9.3.19.0"),sQuery(id+"F0.wireOp",EDGE,"E9.7.19.0"),sQuery(id+"F0.wireOp",EDGE,"E9.11.19.0"),sQuery(id+"F0.wireOp",EDGE,"E9.14.19.0"),sQuery(id+"F0.wireOp",EDGE,"E9.1.20.0"),sQuery(id+"F0.wireOp",EDGE,"E9.3.20.0"),sQuery(id+"F0.wireOp",EDGE,"E9.7.20.0"),sQuery(id+"F0.wireOp",EDGE,"E9.11.20.0"),sQuery(id+"F0.wireOp",EDGE,"E9.14.20.0"),sQuery(id+"F0.wireOp",EDGE,"E9.1.21.0"),sQuery(id+"F0.wireOp",EDGE,"E9.3.21.0"),sQuery(id+"F0.wireOp",EDGE,"E9.7.21.0"),sQuery(id+"F0.wireOp",EDGE,"E9.11.21.0"),sQuery(id+"F0.wireOp",EDGE,"E9.14.21.0"),sQuery(id+"F0.wireOp",EDGE,"E9.1.22.0"),sQuery(id+"F0.wireOp",EDGE,"E9.3.22.0"),sQuery(id+"F0.wireOp",EDGE,"E9.7.22.0"),sQuery(id+"F0.wireOp",EDGE,"E9.11.22.0"),sQuery(id+"F0.wireOp",EDGE,"E9.14.22.0"),sQuery(id+"F0.wireOp",EDGE,"E9.1.23.0"),sQuery(id+"F0.wireOp",EDGE,"E9.3.23.0"),sQuery(id+"F0.wireOp",EDGE,"E9.7.23.0"),sQuery(id+"F0.wireOp",EDGE,"E9.11.23.0"),sQuery(id+"F0.wireOp",EDGE,"E9.14.23.0"),sQuery(id+"F0.wireOp",EDGE,"E9.1.24.0"),sQuery(id+"F0.wireOp",EDGE,"E9.3.24.0"),sQuery(id+"F0.wireOp",EDGE,"E9.7.24.0"),sQuery(id+"F0.wireOp",EDGE,"E9.11.24.0"),sQuery(id+"F0.wireOp",EDGE,"E9.14.24.0"),sQuery(id+"F0.wireOp",EDGE,"E9.1.25.0"),sQuery(id+"F0.wireOp",EDGE,"E9.3.25.0"),sQuery(id+"F0.wireOp",EDGE,"E9.7.25.0"),sQuery(id+"F0.wireOp",EDGE,"E9.11.25.0"),sQuery(id+"F0.wireOp",EDGE,"E9.14.25.0"),sQuery(id+"F0.wireOp",EDGE,"E9.1.26.0"),sQuery(id+"F0.wireOp",EDGE,"E9.3.26.0"),sQuery(id+"F0.wireOp",EDGE,"E9.7.26.0"),sQuery(id+"F0.wireOp",EDGE,"E9.11.26.0"),sQuery(id+"F0.wireOp",EDGE,"E9.14.26.0"),sQuery(id+"F0.wireOp",EDGE,"E9.1.27.0"),sQuery(id+"F0.wireOp",EDGE,"E9.3.27.0"),sQuery(id+"F0.wireOp",EDGE,"E9.7.27.0"),sQuery(id+"F0.wireOp",EDGE,"E9.11.27.0"),sQuery(id+"F0.wireOp",EDGE,"E9.14.27.0"),sQuery(id+"F0.wireOp",EDGE,"E9.1.28.0"),sQuery(id+"F0.wireOp",EDGE,"E9.3.28.0"),sQuery(id+"F0.wireOp",EDGE,"E9.7.28.0"),sQuery(id+"F0.wireOp",EDGE,"E9.11.28.0"),sQuery(id+"F0.wireOp",EDGE,"E9.14.28.0"),sQuery(id+"F0.wireOp",EDGE,"E9.1.29.0"),sQuery(id+"F0.wireOp",EDGE,"E9.3.29.0"),sQuery(id+"F0.wireOp",EDGE,"E9.7.29.0"),sQuery(id+"F0.wireOp",EDGE,"E9.11.29.0"),sQuery(id+"F0.wireOp",EDGE,"E9.14.29.0"),sQuery(id+"F0.wireOp",EDGE,"E9.1.30.0"),sQuery(id+"F0.wireOp",EDGE,"E9.3.30.0"),sQuery(id+"F0.wireOp",EDGE,"E9.7.30.0"),sQuery(id+"F0.wireOp",EDGE,"E9.11.30.0"),sQuery(id+"F0.wireOp",EDGE,"E9.14.30.0"),sQuery(id+"F0.wireOp",EDGE,"E9.1.31.0"),sQuery(id+"F0.wireOp",EDGE,"E9.3.31.0"),sQuery(id+"F0.wireOp",EDGE,"E9.7.31.0"),sQuery(id+"F0.wireOp",EDGE,"E9.11.31.0"),sQuery(id+"F0.wireOp",EDGE,"E9.14.31.0"),sQuery(id+"F0.wireOp",EDGE,"E9.1.32.0"),sQuery(id+"F0.wireOp",EDGE,"E9.3.32.0"),sQuery(id+"F0.wireOp",EDGE,"E9.7.32.0"),sQuery(id+"F0.wireOp",EDGE,"E9.11.32.0"),sQuery(id+"F0.wireOp",EDGE,"E9.14.32.0"),sQuery(id+"F0.wireOp",EDGE,"E9.1.33.0"),sQuery(id+"F0.wireOp",EDGE,"E9.3.33.0"),sQuery(id+"F0.wireOp",EDGE,"E9.7.33.0"),sQuery(id+"F0.wireOp",EDGE,"E9.11.33.0"),sQuery(id+"F0.wireOp",EDGE,"E9.14.33.0"),sQuery(id+"F0.wireOp",EDGE,"E9.1.34.0"),sQuery(id+"F0.wireOp",EDGE,"E9.3.34.0"),sQuery(id+"F0.wireOp",EDGE,"E9.7.34.0"),sQuery(id+"F0.wireOp",EDGE,"E9.11.34.0"),sQuery(id+"F0.wireOp",EDGE,"E9.14.34.0"),sQuery(id+"F0.wireOp",EDGE,"E9.1.35.0"),sQuery(id+"F0.wireOp",EDGE,"E9.3.35.0"),sQuery(id+"F0.wireOp",EDGE,"E9.7.35.0"),sQuery(id+"F0.wireOp",EDGE,"E9.11.35.0"),sQuery(id+"F0.wireOp",EDGE,"E9.14.35.0"),sQuery(id+"F0.wireOp",EDGE,"E9.1.36.0"),sQuery(id+"F0.wireOp",EDGE,"E9.3.36.0"),sQuery(id+"F0.wireOp",EDGE,"E9.7.36.0"),sQuery(id+"F0.wireOp",EDGE,"E9.11.36.0"),sQuery(id+"F0.wireOp",EDGE,"E9.14.36.0"),sQuery(id+"F0.wireOp",EDGE,"E9.1.37.0"),sQuery(id+"F0.wireOp",EDGE,"E9.3.37.0"),sQuery(id+"F0.wireOp",EDGE,"E9.7.37.0"),sQuery(id+"F0.wireOp",EDGE,"E9.11.37.0"),sQuery(id+"F0.wireOp",EDGE,"E9.14.37.0"),sQuery(id+"F0.wireOp",EDGE,"E9.1.38.0"),sQuery(id+"F0.wireOp",EDGE,"E9.3.38.0"),sQuery(id+"F0.wireOp",EDGE,"E9.7.38.0"),sQuery(id+"F0.wireOp",EDGE,"E9.11.38.0"),sQuery(id+"F0.wireOp",EDGE,"E9.14.38.0"),sQuery(id+"F0.wireOp",EDGE,"E9.1.39.0"),sQuery(id+"F0.wireOp",EDGE,"E9.3.39.0"),sQuery(id+"F0.wireOp",EDGE,"E9.7.39.0"),sQuery(id+"F0.wireOp",EDGE,"E9.11.39.0"),sQuery(id+"F0.wireOp",EDGE,"E9.14.39.0"),sQuery(id+"F0.wireOp",EDGE,"E9.1.40.0"),sQuery(id+"F0.wireOp",EDGE,"E9.3.40.0"),sQuery(id+"F0.wireOp",EDGE,"E9.7.40.0"),sQuery(id+"F0.wireOp",EDGE,"E9.11.40.0"),sQuery(id+"F0.wireOp",EDGE,"E9.14.40.0"),sQuery(id+"F0.wireOp",EDGE,"E9.1.41.0"),sQuery(id+"F0.wireOp",EDGE,"E9.3.41.0"),sQuery(id+"F0.wireOp",EDGE,"E9.7.41.0"),sQuery(id+"F0.wireOp",EDGE,"E9.11.41.0"),sQuery(id+"F0.wireOp",EDGE,"E9.14.41.0"),sQuery(id+"F0.wireOp",EDGE,"E9.1.42.0"),sQuery(id+"F0.wireOp",EDGE,"E9.3.42.0"),sQuery(id+"F0.wireOp",EDGE,"E9.7.42.0"),sQuery(id+"F0.wireOp",EDGE,"E9.11.42.0"),sQuery(id+"F0.wireOp",EDGE,"E9.14.42.0"),sQuery(id+"F0.wireOp",EDGE,"E9.1.43.0"),sQuery(id+"F0.wireOp",EDGE,"E9.3.43.0"),sQuery(id+"F0.wireOp",EDGE,"E9.7.43.0"),sQuery(id+"F0.wireOp",EDGE,"E9.11.43.0"),sQuery(id+"F0.wireOp",EDGE,"E9.14.43.0"),sQuery(id+"F0.wireOp",EDGE,"E9.1.44.0"),sQuery(id+"F0.wireOp",EDGE,"E9.3.44.0"),sQuery(id+"F0.wireOp",EDGE,"E9.7.44.0"),sQuery(id+"F0.wireOp",EDGE,"E9.11.44.0"),sQuery(id+"F0.wireOp",EDGE,"E9.14.44.0"),sQuery(id+"F0.wireOp",EDGE,"E9.1.45.0"),sQuery(id+"F0.wireOp",EDGE,"E9.3.45.0"),sQuery(id+"F0.wireOp",EDGE,"E9.7.45.0"),sQuery(id+"F0.wireOp",EDGE,"E9.11.45.0"),sQuery(id+"F0.wireOp",EDGE,"E9.14.45.0"),sQuery(id+"F0.wireOp",EDGE,"E9.1.46.0"),sQuery(id+"F0.wireOp",EDGE,"E9.3.46.0"),sQuery(id+"F0.wireOp",EDGE,"E9.7.46.0"),sQuery(id+"F0.wireOp",EDGE,"E9.11.46.0"),sQuery(id+"F0.wireOp",EDGE,"E9.14.46.0"),sQuery(id+"F0.wireOp",EDGE,"E9.1.47.0"),sQuery(id+"F0.wireOp",EDGE,"E9.3.47.0"),sQuery(id+"F0.wireOp",EDGE,"E9.7.47.0"),sQuery(id+"F0.wireOp",EDGE,"E9.11.47.0"),sQuery(id+"F0.wireOp",EDGE,"E9.14.47.0"),sQuery(id+"F0.wireOp",EDGE,"E9.1.48.0"),sQuery(id+"F0.wireOp",EDGE,"E9.3.48.0"),sQuery(id+"F0.wireOp",EDGE,"E9.7.48.0"),sQuery(id+"F0.wireOp",EDGE,"E9.11.48.0"),sQuery(id+"F0.wireOp",EDGE,"E9.14.48.0"),sQuery(id+"F0.wireOp",EDGE,"E9.1.49.0"),sQuery(id+"F0.wireOp",EDGE,"E9.3.49.0"),sQuery(id+"F0.wireOp",EDGE,"E9.7.49.0"),sQuery(id+"F0.wireOp",EDGE,"E9.11.49.0"),sQuery(id+"F0.wireOp",EDGE,"E9.14.49.0"),sQuery(id+"F0.wireOp",EDGE,"E9.1.50.0"),sQuery(id+"F0.wireOp",EDGE,"E9.3.50.0"),sQuery(id+"F0.wireOp",EDGE,"E9.7.50.0"),sQuery(id+"F0.wireOp",EDGE,"E9.11.50.0"),sQuery(id+"F0.wireOp",EDGE,"E9.14.50.0"),sQuery(id+"F0.wireOp",EDGE,"E9.1.51.0"),sQuery(id+"F0.wireOp",EDGE,"E9.3.51.0"),sQuery(id+"F0.wireOp",EDGE,"E9.7.51.0"),sQuery(id+"F0.wireOp",EDGE,"E9.11.51.0"),sQuery(id+"F0.wireOp",EDGE,"E9.14.51.0"),sQuery(id+"F0.wireOp",EDGE,"E9.1.52.0"),sQuery(id+"F0.wireOp",EDGE,"E9.3.52.0"),sQuery(id+"F0.wireOp",EDGE,"E9.7.52.0"),sQuery(id+"F0.wireOp",EDGE,"E9.11.52.0"),sQuery(id+"F0.wireOp",EDGE,"E9.14.52.0"),sQuery(id+"F0.wireOp",EDGE,"E9.1.53.0"),sQuery(id+"F0.wireOp",EDGE,"E9.3.53.0"),sQuery(id+"F0.wireOp",EDGE,"E9.7.53.0"),sQuery(id+"F0.wireOp",EDGE,"E9.11.53.0"),sQuery(id+"F0.wireOp",EDGE,"E9.14.53.0"),sQuery(id+"F0.wireOp",EDGE,"E9.1.54.0"),sQuery(id+"F0.wireOp",EDGE,"E9.3.54.0"),sQuery(id+"F0.wireOp",EDGE,"E9.7.54.0"),sQuery(id+"F0.wireOp",EDGE,"E9.11.54.0"),sQuery(id+"F0.wireOp",EDGE,"E9.14.54.0"),sQuery(id+"F0.wireOp",EDGE,"E9.1.55.0"),sQuery(id+"F0.wireOp",EDGE,"E9.3.55.0"),sQuery(id+"F0.wireOp",EDGE,"E9.7.55.0"),sQuery(id+"F0.wireOp",EDGE,"E9.11.55.0"),sQuery(id+"F0.wireOp",EDGE,"E9.14.55.0"),sQuery(id+"F0.wireOp",EDGE,"E9.1.56.0"),sQuery(id+"F0.wireOp",EDGE,"E9.3.56.0"),sQuery(id+"F0.wireOp",EDGE,"E9.7.56.0"),sQuery(id+"F0.wireOp",EDGE,"E9.11.56.0"),sQuery(id+"F0.wireOp",EDGE,"E9.14.56.0"),sQuery(id+"F0.wireOp",EDGE,"E9.1.57.0"),sQuery(id+"F0.wireOp",EDGE,"E9.3.57.0"),sQuery(id+"F0.wireOp",EDGE,"E9.7.57.0"),sQuery(id+"F0.wireOp",EDGE,"E9.11.57.0"),sQuery(id+"F0.wireOp",EDGE,"E9.14.57.0"),sQuery(id+"F0.wireOp",EDGE,"E9.1.58.0"),sQuery(id+"F0.wireOp",EDGE,"E9.3.58.0"),sQuery(id+"F0.wireOp",EDGE,"E9.7.58.0"),sQuery(id+"F0.wireOp",EDGE,"E9.11.58.0"),sQuery(id+"F0.wireOp",EDGE,"E9.14.58.0"),sQuery(id+"F0.wireOp",EDGE,"E9.1.59.0"),sQuery(id+"F0.wireOp",EDGE,"E9.3.59.0"),sQuery(id+"F0.wireOp",EDGE,"E9.7.59.0"),sQuery(id+"F0.wireOp",EDGE,"E9.11.59.0"),sQuery(id+"F0.wireOp",EDGE,"E9.14.59.0"),sQuery(id+"F2.wireOp",EDGE,"E20.0")])],"isStart":false})});
            var Q3;
            Q3=makeQuery(id+"F8.boolean.opBoolean","COPY",EDGE,{"derivedFrom":makeQuery(id+"F8.opExtrude","CAP_EDGE",EDGE,{"disambiguationData":[OSD([sQuery(id+"F0.wireOp",EDGE,"E0"),sQuery(id+"F0.wireOp",EDGE,"E1"),sQuery(id+"F0.wireOp",EDGE,"E3"),sQuery(id+"F0.wireOp",EDGE,"E4"),sQuery(id+"F0.wireOp",EDGE,"E5"),sQuery(id+"F0.wireOp",EDGE,"E6.trimOffspring"),sQuery(id+"F0.wireOp",EDGE,"E7"),sQuery(id+"F0.wireOp",EDGE,"E8.1.0"),sQuery(id+"F0.wireOp",EDGE,"E8.1.1"),sQuery(id+"F0.wireOp",EDGE,"E8.1.2"),sQuery(id+"F0.wireOp",EDGE,"E8.1.3"),sQuery(id+"F0.wireOp",EDGE,"E8.1.4"),sQuery(id+"F0.wireOp",EDGE,"E8.2.0"),sQuery(id+"F0.wireOp",EDGE,"E8.2.1"),sQuery(id+"F0.wireOp",EDGE,"E8.2.2"),sQuery(id+"F0.wireOp",EDGE,"E8.2.3"),sQuery(id+"F0.wireOp",EDGE,"E8.2.4"),sQuery(id+"F0.wireOp",EDGE,"E9.1.3.0"),sQuery(id+"F0.wireOp",EDGE,"E9.3.3.0"),sQuery(id+"F0.wireOp",EDGE,"E9.7.3.0"),sQuery(id+"F0.wireOp",EDGE,"E9.11.3.0"),sQuery(id+"F0.wireOp",EDGE,"E9.14.3.0"),sQuery(id+"F0.wireOp",EDGE,"E9.1.4.0"),sQuery(id+"F0.wireOp",EDGE,"E9.3.4.0"),sQuery(id+"F0.wireOp",EDGE,"E9.7.4.0"),sQuery(id+"F0.wireOp",EDGE,"E9.11.4.0"),sQuery(id+"F0.wireOp",EDGE,"E9.14.4.0"),sQuery(id+"F0.wireOp",EDGE,"E9.1.5.0"),sQuery(id+"F0.wireOp",EDGE,"E9.3.5.0"),sQuery(id+"F0.wireOp",EDGE,"E9.7.5.0"),sQuery(id+"F0.wireOp",EDGE,"E9.11.5.0"),sQuery(id+"F0.wireOp",EDGE,"E9.14.5.0"),sQuery(id+"F0.wireOp",EDGE,"E9.1.6.0"),sQuery(id+"F0.wireOp",EDGE,"E9.3.6.0"),sQuery(id+"F0.wireOp",EDGE,"E9.7.6.0"),sQuery(id+"F0.wireOp",EDGE,"E9.11.6.0"),sQuery(id+"F0.wireOp",EDGE,"E9.14.6.0"),sQuery(id+"F0.wireOp",EDGE,"E9.1.7.0"),sQuery(id+"F0.wireOp",EDGE,"E9.3.7.0"),sQuery(id+"F0.wireOp",EDGE,"E9.7.7.0"),sQuery(id+"F0.wireOp",EDGE,"E9.11.7.0"),sQuery(id+"F0.wireOp",EDGE,"E9.14.7.0"),sQuery(id+"F0.wireOp",EDGE,"E9.1.8.0"),sQuery(id+"F0.wireOp",EDGE,"E9.3.8.0"),sQuery(id+"F0.wireOp",EDGE,"E9.7.8.0"),sQuery(id+"F0.wireOp",EDGE,"E9.11.8.0"),sQuery(id+"F0.wireOp",EDGE,"E9.14.8.0"),sQuery(id+"F0.wireOp",EDGE,"E9.1.9.0"),sQuery(id+"F0.wireOp",EDGE,"E9.3.9.0"),sQuery(id+"F0.wireOp",EDGE,"E9.7.9.0"),sQuery(id+"F0.wireOp",EDGE,"E9.11.9.0"),sQuery(id+"F0.wireOp",EDGE,"E9.14.9.0"),sQuery(id+"F0.wireOp",EDGE,"E9.1.10.0"),sQuery(id+"F0.wireOp",EDGE,"E9.3.10.0"),sQuery(id+"F0.wireOp",EDGE,"E9.7.10.0"),sQuery(id+"F0.wireOp",EDGE,"E9.11.10.0"),sQuery(id+"F0.wireOp",EDGE,"E9.14.10.0"),sQuery(id+"F0.wireOp",EDGE,"E9.1.11.0"),sQuery(id+"F0.wireOp",EDGE,"E9.3.11.0"),sQuery(id+"F0.wireOp",EDGE,"E9.7.11.0"),sQuery(id+"F0.wireOp",EDGE,"E9.11.11.0"),sQuery(id+"F0.wireOp",EDGE,"E9.14.11.0"),sQuery(id+"F0.wireOp",EDGE,"E9.1.12.0"),sQuery(id+"F0.wireOp",EDGE,"E9.3.12.0"),sQuery(id+"F0.wireOp",EDGE,"E9.7.12.0"),sQuery(id+"F0.wireOp",EDGE,"E9.11.12.0"),sQuery(id+"F0.wireOp",EDGE,"E9.14.12.0"),sQuery(id+"F0.wireOp",EDGE,"E9.1.13.0"),sQuery(id+"F0.wireOp",EDGE,"E9.3.13.0"),sQuery(id+"F0.wireOp",EDGE,"E9.7.13.0"),sQuery(id+"F0.wireOp",EDGE,"E9.11.13.0"),sQuery(id+"F0.wireOp",EDGE,"E9.14.13.0"),sQuery(id+"F0.wireOp",EDGE,"E9.1.14.0"),sQuery(id+"F0.wireOp",EDGE,"E9.3.14.0"),sQuery(id+"F0.wireOp",EDGE,"E9.7.14.0"),sQuery(id+"F0.wireOp",EDGE,"E9.11.14.0"),sQuery(id+"F0.wireOp",EDGE,"E9.14.14.0"),sQuery(id+"F0.wireOp",EDGE,"E9.1.15.0"),sQuery(id+"F0.wireOp",EDGE,"E9.3.15.0"),sQuery(id+"F0.wireOp",EDGE,"E9.7.15.0"),sQuery(id+"F0.wireOp",EDGE,"E9.11.15.0"),sQuery(id+"F0.wireOp",EDGE,"E9.14.15.0"),sQuery(id+"F0.wireOp",EDGE,"E9.1.16.0"),sQuery(id+"F0.wireOp",EDGE,"E9.3.16.0"),sQuery(id+"F0.wireOp",EDGE,"E9.7.16.0"),sQuery(id+"F0.wireOp",EDGE,"E9.11.16.0"),sQuery(id+"F0.wireOp",EDGE,"E9.14.16.0"),sQuery(id+"F0.wireOp",EDGE,"E9.1.17.0"),sQuery(id+"F0.wireOp",EDGE,"E9.3.17.0"),sQuery(id+"F0.wireOp",EDGE,"E9.7.17.0"),sQuery(id+"F0.wireOp",EDGE,"E9.11.17.0"),sQuery(id+"F0.wireOp",EDGE,"E9.14.17.0"),sQuery(id+"F0.wireOp",EDGE,"E9.1.18.0"),sQuery(id+"F0.wireOp",EDGE,"E9.3.18.0"),sQuery(id+"F0.wireOp",EDGE,"E9.7.18.0"),sQuery(id+"F0.wireOp",EDGE,"E9.11.18.0"),sQuery(id+"F0.wireOp",EDGE,"E9.14.18.0"),sQuery(id+"F0.wireOp",EDGE,"E9.1.19.0"),sQuery(id+"F0.wireOp",EDGE,"E9.3.19.0"),sQuery(id+"F0.wireOp",EDGE,"E9.7.19.0"),sQuery(id+"F0.wireOp",EDGE,"E9.11.19.0"),sQuery(id+"F0.wireOp",EDGE,"E9.14.19.0"),sQuery(id+"F0.wireOp",EDGE,"E9.1.20.0"),sQuery(id+"F0.wireOp",EDGE,"E9.3.20.0"),sQuery(id+"F0.wireOp",EDGE,"E9.7.20.0"),sQuery(id+"F0.wireOp",EDGE,"E9.11.20.0"),sQuery(id+"F0.wireOp",EDGE,"E9.14.20.0"),sQuery(id+"F0.wireOp",EDGE,"E9.1.21.0"),sQuery(id+"F0.wireOp",EDGE,"E9.3.21.0"),sQuery(id+"F0.wireOp",EDGE,"E9.7.21.0"),sQuery(id+"F0.wireOp",EDGE,"E9.11.21.0"),sQuery(id+"F0.wireOp",EDGE,"E9.14.21.0"),sQuery(id+"F0.wireOp",EDGE,"E9.1.22.0"),sQuery(id+"F0.wireOp",EDGE,"E9.3.22.0"),sQuery(id+"F0.wireOp",EDGE,"E9.7.22.0"),sQuery(id+"F0.wireOp",EDGE,"E9.11.22.0"),sQuery(id+"F0.wireOp",EDGE,"E9.14.22.0"),sQuery(id+"F0.wireOp",EDGE,"E9.1.23.0"),sQuery(id+"F0.wireOp",EDGE,"E9.3.23.0"),sQuery(id+"F0.wireOp",EDGE,"E9.7.23.0"),sQuery(id+"F0.wireOp",EDGE,"E9.11.23.0"),sQuery(id+"F0.wireOp",EDGE,"E9.14.23.0"),sQuery(id+"F0.wireOp",EDGE,"E9.1.24.0"),sQuery(id+"F0.wireOp",EDGE,"E9.3.24.0"),sQuery(id+"F0.wireOp",EDGE,"E9.7.24.0"),sQuery(id+"F0.wireOp",EDGE,"E9.11.24.0"),sQuery(id+"F0.wireOp",EDGE,"E9.14.24.0"),sQuery(id+"F0.wireOp",EDGE,"E9.1.25.0"),sQuery(id+"F0.wireOp",EDGE,"E9.3.25.0"),sQuery(id+"F0.wireOp",EDGE,"E9.7.25.0"),sQuery(id+"F0.wireOp",EDGE,"E9.11.25.0"),sQuery(id+"F0.wireOp",EDGE,"E9.14.25.0"),sQuery(id+"F0.wireOp",EDGE,"E9.1.26.0"),sQuery(id+"F0.wireOp",EDGE,"E9.3.26.0"),sQuery(id+"F0.wireOp",EDGE,"E9.7.26.0"),sQuery(id+"F0.wireOp",EDGE,"E9.11.26.0"),sQuery(id+"F0.wireOp",EDGE,"E9.14.26.0"),sQuery(id+"F0.wireOp",EDGE,"E9.1.27.0"),sQuery(id+"F0.wireOp",EDGE,"E9.3.27.0"),sQuery(id+"F0.wireOp",EDGE,"E9.7.27.0"),sQuery(id+"F0.wireOp",EDGE,"E9.11.27.0"),sQuery(id+"F0.wireOp",EDGE,"E9.14.27.0"),sQuery(id+"F0.wireOp",EDGE,"E9.1.28.0"),sQuery(id+"F0.wireOp",EDGE,"E9.3.28.0"),sQuery(id+"F0.wireOp",EDGE,"E9.7.28.0"),sQuery(id+"F0.wireOp",EDGE,"E9.11.28.0"),sQuery(id+"F0.wireOp",EDGE,"E9.14.28.0"),sQuery(id+"F0.wireOp",EDGE,"E9.1.29.0"),sQuery(id+"F0.wireOp",EDGE,"E9.3.29.0"),sQuery(id+"F0.wireOp",EDGE,"E9.7.29.0"),sQuery(id+"F0.wireOp",EDGE,"E9.11.29.0"),sQuery(id+"F0.wireOp",EDGE,"E9.14.29.0"),sQuery(id+"F0.wireOp",EDGE,"E9.1.30.0"),sQuery(id+"F0.wireOp",EDGE,"E9.3.30.0"),sQuery(id+"F0.wireOp",EDGE,"E9.7.30.0"),sQuery(id+"F0.wireOp",EDGE,"E9.11.30.0"),sQuery(id+"F0.wireOp",EDGE,"E9.14.30.0"),sQuery(id+"F0.wireOp",EDGE,"E9.1.31.0"),sQuery(id+"F0.wireOp",EDGE,"E9.3.31.0"),sQuery(id+"F0.wireOp",EDGE,"E9.7.31.0"),sQuery(id+"F0.wireOp",EDGE,"E9.11.31.0"),sQuery(id+"F0.wireOp",EDGE,"E9.14.31.0"),sQuery(id+"F0.wireOp",EDGE,"E9.1.32.0"),sQuery(id+"F0.wireOp",EDGE,"E9.3.32.0"),sQuery(id+"F0.wireOp",EDGE,"E9.7.32.0"),sQuery(id+"F0.wireOp",EDGE,"E9.11.32.0"),sQuery(id+"F0.wireOp",EDGE,"E9.14.32.0"),sQuery(id+"F0.wireOp",EDGE,"E9.1.33.0"),sQuery(id+"F0.wireOp",EDGE,"E9.3.33.0"),sQuery(id+"F0.wireOp",EDGE,"E9.7.33.0"),sQuery(id+"F0.wireOp",EDGE,"E9.11.33.0"),sQuery(id+"F0.wireOp",EDGE,"E9.14.33.0"),sQuery(id+"F0.wireOp",EDGE,"E9.1.34.0"),sQuery(id+"F0.wireOp",EDGE,"E9.3.34.0"),sQuery(id+"F0.wireOp",EDGE,"E9.7.34.0"),sQuery(id+"F0.wireOp",EDGE,"E9.11.34.0"),sQuery(id+"F0.wireOp",EDGE,"E9.14.34.0"),sQuery(id+"F0.wireOp",EDGE,"E9.1.35.0"),sQuery(id+"F0.wireOp",EDGE,"E9.3.35.0"),sQuery(id+"F0.wireOp",EDGE,"E9.7.35.0"),sQuery(id+"F0.wireOp",EDGE,"E9.11.35.0"),sQuery(id+"F0.wireOp",EDGE,"E9.14.35.0"),sQuery(id+"F0.wireOp",EDGE,"E9.1.36.0"),sQuery(id+"F0.wireOp",EDGE,"E9.3.36.0"),sQuery(id+"F0.wireOp",EDGE,"E9.7.36.0"),sQuery(id+"F0.wireOp",EDGE,"E9.11.36.0"),sQuery(id+"F0.wireOp",EDGE,"E9.14.36.0"),sQuery(id+"F0.wireOp",EDGE,"E9.1.37.0"),sQuery(id+"F0.wireOp",EDGE,"E9.3.37.0"),sQuery(id+"F0.wireOp",EDGE,"E9.7.37.0"),sQuery(id+"F0.wireOp",EDGE,"E9.11.37.0"),sQuery(id+"F0.wireOp",EDGE,"E9.14.37.0"),sQuery(id+"F0.wireOp",EDGE,"E9.1.38.0"),sQuery(id+"F0.wireOp",EDGE,"E9.3.38.0"),sQuery(id+"F0.wireOp",EDGE,"E9.7.38.0"),sQuery(id+"F0.wireOp",EDGE,"E9.11.38.0"),sQuery(id+"F0.wireOp",EDGE,"E9.14.38.0"),sQuery(id+"F0.wireOp",EDGE,"E9.1.39.0"),sQuery(id+"F0.wireOp",EDGE,"E9.3.39.0"),sQuery(id+"F0.wireOp",EDGE,"E9.7.39.0"),sQuery(id+"F0.wireOp",EDGE,"E9.11.39.0"),sQuery(id+"F0.wireOp",EDGE,"E9.14.39.0"),sQuery(id+"F0.wireOp",EDGE,"E9.1.40.0"),sQuery(id+"F0.wireOp",EDGE,"E9.3.40.0"),sQuery(id+"F0.wireOp",EDGE,"E9.7.40.0"),sQuery(id+"F0.wireOp",EDGE,"E9.11.40.0"),sQuery(id+"F0.wireOp",EDGE,"E9.14.40.0"),sQuery(id+"F0.wireOp",EDGE,"E9.1.41.0"),sQuery(id+"F0.wireOp",EDGE,"E9.3.41.0"),sQuery(id+"F0.wireOp",EDGE,"E9.7.41.0"),sQuery(id+"F0.wireOp",EDGE,"E9.11.41.0"),sQuery(id+"F0.wireOp",EDGE,"E9.14.41.0"),sQuery(id+"F0.wireOp",EDGE,"E9.1.42.0"),sQuery(id+"F0.wireOp",EDGE,"E9.3.42.0"),sQuery(id+"F0.wireOp",EDGE,"E9.7.42.0"),sQuery(id+"F0.wireOp",EDGE,"E9.11.42.0"),sQuery(id+"F0.wireOp",EDGE,"E9.14.42.0"),sQuery(id+"F0.wireOp",EDGE,"E9.1.43.0"),sQuery(id+"F0.wireOp",EDGE,"E9.3.43.0"),sQuery(id+"F0.wireOp",EDGE,"E9.7.43.0"),sQuery(id+"F0.wireOp",EDGE,"E9.11.43.0"),sQuery(id+"F0.wireOp",EDGE,"E9.14.43.0"),sQuery(id+"F0.wireOp",EDGE,"E9.1.44.0"),sQuery(id+"F0.wireOp",EDGE,"E9.3.44.0"),sQuery(id+"F0.wireOp",EDGE,"E9.7.44.0"),sQuery(id+"F0.wireOp",EDGE,"E9.11.44.0"),sQuery(id+"F0.wireOp",EDGE,"E9.14.44.0"),sQuery(id+"F0.wireOp",EDGE,"E9.1.45.0"),sQuery(id+"F0.wireOp",EDGE,"E9.3.45.0"),sQuery(id+"F0.wireOp",EDGE,"E9.7.45.0"),sQuery(id+"F0.wireOp",EDGE,"E9.11.45.0"),sQuery(id+"F0.wireOp",EDGE,"E9.14.45.0"),sQuery(id+"F0.wireOp",EDGE,"E9.1.46.0"),sQuery(id+"F0.wireOp",EDGE,"E9.3.46.0"),sQuery(id+"F0.wireOp",EDGE,"E9.7.46.0"),sQuery(id+"F0.wireOp",EDGE,"E9.11.46.0"),sQuery(id+"F0.wireOp",EDGE,"E9.14.46.0"),sQuery(id+"F0.wireOp",EDGE,"E9.1.47.0"),sQuery(id+"F0.wireOp",EDGE,"E9.3.47.0"),sQuery(id+"F0.wireOp",EDGE,"E9.7.47.0"),sQuery(id+"F0.wireOp",EDGE,"E9.11.47.0"),sQuery(id+"F0.wireOp",EDGE,"E9.14.47.0"),sQuery(id+"F0.wireOp",EDGE,"E9.1.48.0"),sQuery(id+"F0.wireOp",EDGE,"E9.3.48.0"),sQuery(id+"F0.wireOp",EDGE,"E9.7.48.0"),sQuery(id+"F0.wireOp",EDGE,"E9.11.48.0"),sQuery(id+"F0.wireOp",EDGE,"E9.14.48.0"),sQuery(id+"F0.wireOp",EDGE,"E9.1.49.0"),sQuery(id+"F0.wireOp",EDGE,"E9.3.49.0"),sQuery(id+"F0.wireOp",EDGE,"E9.7.49.0"),sQuery(id+"F0.wireOp",EDGE,"E9.11.49.0"),sQuery(id+"F0.wireOp",EDGE,"E9.14.49.0"),sQuery(id+"F0.wireOp",EDGE,"E9.1.50.0"),sQuery(id+"F0.wireOp",EDGE,"E9.3.50.0"),sQuery(id+"F0.wireOp",EDGE,"E9.7.50.0"),sQuery(id+"F0.wireOp",EDGE,"E9.11.50.0"),sQuery(id+"F0.wireOp",EDGE,"E9.14.50.0"),sQuery(id+"F0.wireOp",EDGE,"E9.1.51.0"),sQuery(id+"F0.wireOp",EDGE,"E9.3.51.0"),sQuery(id+"F0.wireOp",EDGE,"E9.7.51.0"),sQuery(id+"F0.wireOp",EDGE,"E9.11.51.0"),sQuery(id+"F0.wireOp",EDGE,"E9.14.51.0"),sQuery(id+"F0.wireOp",EDGE,"E9.1.52.0"),sQuery(id+"F0.wireOp",EDGE,"E9.3.52.0"),sQuery(id+"F0.wireOp",EDGE,"E9.7.52.0"),sQuery(id+"F0.wireOp",EDGE,"E9.11.52.0"),sQuery(id+"F0.wireOp",EDGE,"E9.14.52.0"),sQuery(id+"F0.wireOp",EDGE,"E9.1.53.0"),sQuery(id+"F0.wireOp",EDGE,"E9.3.53.0"),sQuery(id+"F0.wireOp",EDGE,"E9.7.53.0"),sQuery(id+"F0.wireOp",EDGE,"E9.11.53.0"),sQuery(id+"F0.wireOp",EDGE,"E9.14.53.0"),sQuery(id+"F0.wireOp",EDGE,"E9.1.54.0"),sQuery(id+"F0.wireOp",EDGE,"E9.3.54.0"),sQuery(id+"F0.wireOp",EDGE,"E9.7.54.0"),sQuery(id+"F0.wireOp",EDGE,"E9.11.54.0"),sQuery(id+"F0.wireOp",EDGE,"E9.14.54.0"),sQuery(id+"F0.wireOp",EDGE,"E9.1.55.0"),sQuery(id+"F0.wireOp",EDGE,"E9.3.55.0"),sQuery(id+"F0.wireOp",EDGE,"E9.7.55.0"),sQuery(id+"F0.wireOp",EDGE,"E9.11.55.0"),sQuery(id+"F0.wireOp",EDGE,"E9.14.55.0"),sQuery(id+"F0.wireOp",EDGE,"E9.1.56.0"),sQuery(id+"F0.wireOp",EDGE,"E9.3.56.0"),sQuery(id+"F0.wireOp",EDGE,"E9.7.56.0"),sQuery(id+"F0.wireOp",EDGE,"E9.11.56.0"),sQuery(id+"F0.wireOp",EDGE,"E9.14.56.0"),sQuery(id+"F0.wireOp",EDGE,"E9.1.57.0"),sQuery(id+"F0.wireOp",EDGE,"E9.3.57.0"),sQuery(id+"F0.wireOp",EDGE,"E9.7.57.0"),sQuery(id+"F0.wireOp",EDGE,"E9.11.57.0"),sQuery(id+"F0.wireOp",EDGE,"E9.14.57.0"),sQuery(id+"F0.wireOp",EDGE,"E9.1.58.0"),sQuery(id+"F0.wireOp",EDGE,"E9.3.58.0"),sQuery(id+"F0.wireOp",EDGE,"E9.7.58.0"),sQuery(id+"F0.wireOp",EDGE,"E9.11.58.0"),sQuery(id+"F0.wireOp",EDGE,"E9.14.58.0"),sQuery(id+"F0.wireOp",EDGE,"E9.1.59.0"),sQuery(id+"F0.wireOp",EDGE,"E9.3.59.0"),sQuery(id+"F0.wireOp",EDGE,"E9.7.59.0"),sQuery(id+"F0.wireOp",EDGE,"E9.11.59.0"),sQuery(id+"F0.wireOp",EDGE,"E9.14.59.0"),sQuery(id+"F2.wireOp",EDGE,"E26")])],"isStart":false})});
            var Q4;
            Q4=makeQuery(id+"F8.boolean.opBoolean","COPY",EDGE,{"derivedFrom":makeQuery(id+"F8.opExtrude","CAP_EDGE",EDGE,{"disambiguationData":[OSD([sQuery(id+"F0.wireOp",EDGE,"E0"),sQuery(id+"F0.wireOp",EDGE,"E1"),sQuery(id+"F0.wireOp",EDGE,"E3"),sQuery(id+"F0.wireOp",EDGE,"E4"),sQuery(id+"F0.wireOp",EDGE,"E5"),sQuery(id+"F0.wireOp",EDGE,"E6.trimOffspring"),sQuery(id+"F0.wireOp",EDGE,"E7"),sQuery(id+"F0.wireOp",EDGE,"E8.1.0"),sQuery(id+"F0.wireOp",EDGE,"E8.1.1"),sQuery(id+"F0.wireOp",EDGE,"E8.1.2"),sQuery(id+"F0.wireOp",EDGE,"E8.1.3"),sQuery(id+"F0.wireOp",EDGE,"E8.1.4"),sQuery(id+"F0.wireOp",EDGE,"E8.2.0"),sQuery(id+"F0.wireOp",EDGE,"E8.2.1"),sQuery(id+"F0.wireOp",EDGE,"E8.2.2"),sQuery(id+"F0.wireOp",EDGE,"E8.2.3"),sQuery(id+"F0.wireOp",EDGE,"E8.2.4"),sQuery(id+"F0.wireOp",EDGE,"E9.1.3.0"),sQuery(id+"F0.wireOp",EDGE,"E9.3.3.0"),sQuery(id+"F0.wireOp",EDGE,"E9.7.3.0"),sQuery(id+"F0.wireOp",EDGE,"E9.11.3.0"),sQuery(id+"F0.wireOp",EDGE,"E9.14.3.0"),sQuery(id+"F0.wireOp",EDGE,"E9.1.4.0"),sQuery(id+"F0.wireOp",EDGE,"E9.3.4.0"),sQuery(id+"F0.wireOp",EDGE,"E9.7.4.0"),sQuery(id+"F0.wireOp",EDGE,"E9.11.4.0"),sQuery(id+"F0.wireOp",EDGE,"E9.14.4.0"),sQuery(id+"F0.wireOp",EDGE,"E9.1.5.0"),sQuery(id+"F0.wireOp",EDGE,"E9.3.5.0"),sQuery(id+"F0.wireOp",EDGE,"E9.7.5.0"),sQuery(id+"F0.wireOp",EDGE,"E9.11.5.0"),sQuery(id+"F0.wireOp",EDGE,"E9.14.5.0"),sQuery(id+"F0.wireOp",EDGE,"E9.1.6.0"),sQuery(id+"F0.wireOp",EDGE,"E9.3.6.0"),sQuery(id+"F0.wireOp",EDGE,"E9.7.6.0"),sQuery(id+"F0.wireOp",EDGE,"E9.11.6.0"),sQuery(id+"F0.wireOp",EDGE,"E9.14.6.0"),sQuery(id+"F0.wireOp",EDGE,"E9.1.7.0"),sQuery(id+"F0.wireOp",EDGE,"E9.3.7.0"),sQuery(id+"F0.wireOp",EDGE,"E9.7.7.0"),sQuery(id+"F0.wireOp",EDGE,"E9.11.7.0"),sQuery(id+"F0.wireOp",EDGE,"E9.14.7.0"),sQuery(id+"F0.wireOp",EDGE,"E9.1.8.0"),sQuery(id+"F0.wireOp",EDGE,"E9.3.8.0"),sQuery(id+"F0.wireOp",EDGE,"E9.7.8.0"),sQuery(id+"F0.wireOp",EDGE,"E9.11.8.0"),sQuery(id+"F0.wireOp",EDGE,"E9.14.8.0"),sQuery(id+"F0.wireOp",EDGE,"E9.1.9.0"),sQuery(id+"F0.wireOp",EDGE,"E9.3.9.0"),sQuery(id+"F0.wireOp",EDGE,"E9.7.9.0"),sQuery(id+"F0.wireOp",EDGE,"E9.11.9.0"),sQuery(id+"F0.wireOp",EDGE,"E9.14.9.0"),sQuery(id+"F0.wireOp",EDGE,"E9.1.10.0"),sQuery(id+"F0.wireOp",EDGE,"E9.3.10.0"),sQuery(id+"F0.wireOp",EDGE,"E9.7.10.0"),sQuery(id+"F0.wireOp",EDGE,"E9.11.10.0"),sQuery(id+"F0.wireOp",EDGE,"E9.14.10.0"),sQuery(id+"F0.wireOp",EDGE,"E9.1.11.0"),sQuery(id+"F0.wireOp",EDGE,"E9.3.11.0"),sQuery(id+"F0.wireOp",EDGE,"E9.7.11.0"),sQuery(id+"F0.wireOp",EDGE,"E9.11.11.0"),sQuery(id+"F0.wireOp",EDGE,"E9.14.11.0"),sQuery(id+"F0.wireOp",EDGE,"E9.1.12.0"),sQuery(id+"F0.wireOp",EDGE,"E9.3.12.0"),sQuery(id+"F0.wireOp",EDGE,"E9.7.12.0"),sQuery(id+"F0.wireOp",EDGE,"E9.11.12.0"),sQuery(id+"F0.wireOp",EDGE,"E9.14.12.0"),sQuery(id+"F0.wireOp",EDGE,"E9.1.13.0"),sQuery(id+"F0.wireOp",EDGE,"E9.3.13.0"),sQuery(id+"F0.wireOp",EDGE,"E9.7.13.0"),sQuery(id+"F0.wireOp",EDGE,"E9.11.13.0"),sQuery(id+"F0.wireOp",EDGE,"E9.14.13.0"),sQuery(id+"F0.wireOp",EDGE,"E9.1.14.0"),sQuery(id+"F0.wireOp",EDGE,"E9.3.14.0"),sQuery(id+"F0.wireOp",EDGE,"E9.7.14.0"),sQuery(id+"F0.wireOp",EDGE,"E9.11.14.0"),sQuery(id+"F0.wireOp",EDGE,"E9.14.14.0"),sQuery(id+"F0.wireOp",EDGE,"E9.1.15.0"),sQuery(id+"F0.wireOp",EDGE,"E9.3.15.0"),sQuery(id+"F0.wireOp",EDGE,"E9.7.15.0"),sQuery(id+"F0.wireOp",EDGE,"E9.11.15.0"),sQuery(id+"F0.wireOp",EDGE,"E9.14.15.0"),sQuery(id+"F0.wireOp",EDGE,"E9.1.16.0"),sQuery(id+"F0.wireOp",EDGE,"E9.3.16.0"),sQuery(id+"F0.wireOp",EDGE,"E9.7.16.0"),sQuery(id+"F0.wireOp",EDGE,"E9.11.16.0"),sQuery(id+"F0.wireOp",EDGE,"E9.14.16.0"),sQuery(id+"F0.wireOp",EDGE,"E9.1.17.0"),sQuery(id+"F0.wireOp",EDGE,"E9.3.17.0"),sQuery(id+"F0.wireOp",EDGE,"E9.7.17.0"),sQuery(id+"F0.wireOp",EDGE,"E9.11.17.0"),sQuery(id+"F0.wireOp",EDGE,"E9.14.17.0"),sQuery(id+"F0.wireOp",EDGE,"E9.1.18.0"),sQuery(id+"F0.wireOp",EDGE,"E9.3.18.0"),sQuery(id+"F0.wireOp",EDGE,"E9.7.18.0"),sQuery(id+"F0.wireOp",EDGE,"E9.11.18.0"),sQuery(id+"F0.wireOp",EDGE,"E9.14.18.0"),sQuery(id+"F0.wireOp",EDGE,"E9.1.19.0"),sQuery(id+"F0.wireOp",EDGE,"E9.3.19.0"),sQuery(id+"F0.wireOp",EDGE,"E9.7.19.0"),sQuery(id+"F0.wireOp",EDGE,"E9.11.19.0"),sQuery(id+"F0.wireOp",EDGE,"E9.14.19.0"),sQuery(id+"F0.wireOp",EDGE,"E9.1.20.0"),sQuery(id+"F0.wireOp",EDGE,"E9.3.20.0"),sQuery(id+"F0.wireOp",EDGE,"E9.7.20.0"),sQuery(id+"F0.wireOp",EDGE,"E9.11.20.0"),sQuery(id+"F0.wireOp",EDGE,"E9.14.20.0"),sQuery(id+"F0.wireOp",EDGE,"E9.1.21.0"),sQuery(id+"F0.wireOp",EDGE,"E9.3.21.0"),sQuery(id+"F0.wireOp",EDGE,"E9.7.21.0"),sQuery(id+"F0.wireOp",EDGE,"E9.11.21.0"),sQuery(id+"F0.wireOp",EDGE,"E9.14.21.0"),sQuery(id+"F0.wireOp",EDGE,"E9.1.22.0"),sQuery(id+"F0.wireOp",EDGE,"E9.3.22.0"),sQuery(id+"F0.wireOp",EDGE,"E9.7.22.0"),sQuery(id+"F0.wireOp",EDGE,"E9.11.22.0"),sQuery(id+"F0.wireOp",EDGE,"E9.14.22.0"),sQuery(id+"F0.wireOp",EDGE,"E9.1.23.0"),sQuery(id+"F0.wireOp",EDGE,"E9.3.23.0"),sQuery(id+"F0.wireOp",EDGE,"E9.7.23.0"),sQuery(id+"F0.wireOp",EDGE,"E9.11.23.0"),sQuery(id+"F0.wireOp",EDGE,"E9.14.23.0"),sQuery(id+"F0.wireOp",EDGE,"E9.1.24.0"),sQuery(id+"F0.wireOp",EDGE,"E9.3.24.0"),sQuery(id+"F0.wireOp",EDGE,"E9.7.24.0"),sQuery(id+"F0.wireOp",EDGE,"E9.11.24.0"),sQuery(id+"F0.wireOp",EDGE,"E9.14.24.0"),sQuery(id+"F0.wireOp",EDGE,"E9.1.25.0"),sQuery(id+"F0.wireOp",EDGE,"E9.3.25.0"),sQuery(id+"F0.wireOp",EDGE,"E9.7.25.0"),sQuery(id+"F0.wireOp",EDGE,"E9.11.25.0"),sQuery(id+"F0.wireOp",EDGE,"E9.14.25.0"),sQuery(id+"F0.wireOp",EDGE,"E9.1.26.0"),sQuery(id+"F0.wireOp",EDGE,"E9.3.26.0"),sQuery(id+"F0.wireOp",EDGE,"E9.7.26.0"),sQuery(id+"F0.wireOp",EDGE,"E9.11.26.0"),sQuery(id+"F0.wireOp",EDGE,"E9.14.26.0"),sQuery(id+"F0.wireOp",EDGE,"E9.1.27.0"),sQuery(id+"F0.wireOp",EDGE,"E9.3.27.0"),sQuery(id+"F0.wireOp",EDGE,"E9.7.27.0"),sQuery(id+"F0.wireOp",EDGE,"E9.11.27.0"),sQuery(id+"F0.wireOp",EDGE,"E9.14.27.0"),sQuery(id+"F0.wireOp",EDGE,"E9.1.28.0"),sQuery(id+"F0.wireOp",EDGE,"E9.3.28.0"),sQuery(id+"F0.wireOp",EDGE,"E9.7.28.0"),sQuery(id+"F0.wireOp",EDGE,"E9.11.28.0"),sQuery(id+"F0.wireOp",EDGE,"E9.14.28.0"),sQuery(id+"F0.wireOp",EDGE,"E9.1.29.0"),sQuery(id+"F0.wireOp",EDGE,"E9.3.29.0"),sQuery(id+"F0.wireOp",EDGE,"E9.7.29.0"),sQuery(id+"F0.wireOp",EDGE,"E9.11.29.0"),sQuery(id+"F0.wireOp",EDGE,"E9.14.29.0"),sQuery(id+"F0.wireOp",EDGE,"E9.1.30.0"),sQuery(id+"F0.wireOp",EDGE,"E9.3.30.0"),sQuery(id+"F0.wireOp",EDGE,"E9.7.30.0"),sQuery(id+"F0.wireOp",EDGE,"E9.11.30.0"),sQuery(id+"F0.wireOp",EDGE,"E9.14.30.0"),sQuery(id+"F0.wireOp",EDGE,"E9.1.31.0"),sQuery(id+"F0.wireOp",EDGE,"E9.3.31.0"),sQuery(id+"F0.wireOp",EDGE,"E9.7.31.0"),sQuery(id+"F0.wireOp",EDGE,"E9.11.31.0"),sQuery(id+"F0.wireOp",EDGE,"E9.14.31.0"),sQuery(id+"F0.wireOp",EDGE,"E9.1.32.0"),sQuery(id+"F0.wireOp",EDGE,"E9.3.32.0"),sQuery(id+"F0.wireOp",EDGE,"E9.7.32.0"),sQuery(id+"F0.wireOp",EDGE,"E9.11.32.0"),sQuery(id+"F0.wireOp",EDGE,"E9.14.32.0"),sQuery(id+"F0.wireOp",EDGE,"E9.1.33.0"),sQuery(id+"F0.wireOp",EDGE,"E9.3.33.0"),sQuery(id+"F0.wireOp",EDGE,"E9.7.33.0"),sQuery(id+"F0.wireOp",EDGE,"E9.11.33.0"),sQuery(id+"F0.wireOp",EDGE,"E9.14.33.0"),sQuery(id+"F0.wireOp",EDGE,"E9.1.34.0"),sQuery(id+"F0.wireOp",EDGE,"E9.3.34.0"),sQuery(id+"F0.wireOp",EDGE,"E9.7.34.0"),sQuery(id+"F0.wireOp",EDGE,"E9.11.34.0"),sQuery(id+"F0.wireOp",EDGE,"E9.14.34.0"),sQuery(id+"F0.wireOp",EDGE,"E9.1.35.0"),sQuery(id+"F0.wireOp",EDGE,"E9.3.35.0"),sQuery(id+"F0.wireOp",EDGE,"E9.7.35.0"),sQuery(id+"F0.wireOp",EDGE,"E9.11.35.0"),sQuery(id+"F0.wireOp",EDGE,"E9.14.35.0"),sQuery(id+"F0.wireOp",EDGE,"E9.1.36.0"),sQuery(id+"F0.wireOp",EDGE,"E9.3.36.0"),sQuery(id+"F0.wireOp",EDGE,"E9.7.36.0"),sQuery(id+"F0.wireOp",EDGE,"E9.11.36.0"),sQuery(id+"F0.wireOp",EDGE,"E9.14.36.0"),sQuery(id+"F0.wireOp",EDGE,"E9.1.37.0"),sQuery(id+"F0.wireOp",EDGE,"E9.3.37.0"),sQuery(id+"F0.wireOp",EDGE,"E9.7.37.0"),sQuery(id+"F0.wireOp",EDGE,"E9.11.37.0"),sQuery(id+"F0.wireOp",EDGE,"E9.14.37.0"),sQuery(id+"F0.wireOp",EDGE,"E9.1.38.0"),sQuery(id+"F0.wireOp",EDGE,"E9.3.38.0"),sQuery(id+"F0.wireOp",EDGE,"E9.7.38.0"),sQuery(id+"F0.wireOp",EDGE,"E9.11.38.0"),sQuery(id+"F0.wireOp",EDGE,"E9.14.38.0"),sQuery(id+"F0.wireOp",EDGE,"E9.1.39.0"),sQuery(id+"F0.wireOp",EDGE,"E9.3.39.0"),sQuery(id+"F0.wireOp",EDGE,"E9.7.39.0"),sQuery(id+"F0.wireOp",EDGE,"E9.11.39.0"),sQuery(id+"F0.wireOp",EDGE,"E9.14.39.0"),sQuery(id+"F0.wireOp",EDGE,"E9.1.40.0"),sQuery(id+"F0.wireOp",EDGE,"E9.3.40.0"),sQuery(id+"F0.wireOp",EDGE,"E9.7.40.0"),sQuery(id+"F0.wireOp",EDGE,"E9.11.40.0"),sQuery(id+"F0.wireOp",EDGE,"E9.14.40.0"),sQuery(id+"F0.wireOp",EDGE,"E9.1.41.0"),sQuery(id+"F0.wireOp",EDGE,"E9.3.41.0"),sQuery(id+"F0.wireOp",EDGE,"E9.7.41.0"),sQuery(id+"F0.wireOp",EDGE,"E9.11.41.0"),sQuery(id+"F0.wireOp",EDGE,"E9.14.41.0"),sQuery(id+"F0.wireOp",EDGE,"E9.1.42.0"),sQuery(id+"F0.wireOp",EDGE,"E9.3.42.0"),sQuery(id+"F0.wireOp",EDGE,"E9.7.42.0"),sQuery(id+"F0.wireOp",EDGE,"E9.11.42.0"),sQuery(id+"F0.wireOp",EDGE,"E9.14.42.0"),sQuery(id+"F0.wireOp",EDGE,"E9.1.43.0"),sQuery(id+"F0.wireOp",EDGE,"E9.3.43.0"),sQuery(id+"F0.wireOp",EDGE,"E9.7.43.0"),sQuery(id+"F0.wireOp",EDGE,"E9.11.43.0"),sQuery(id+"F0.wireOp",EDGE,"E9.14.43.0"),sQuery(id+"F0.wireOp",EDGE,"E9.1.44.0"),sQuery(id+"F0.wireOp",EDGE,"E9.3.44.0"),sQuery(id+"F0.wireOp",EDGE,"E9.7.44.0"),sQuery(id+"F0.wireOp",EDGE,"E9.11.44.0"),sQuery(id+"F0.wireOp",EDGE,"E9.14.44.0"),sQuery(id+"F0.wireOp",EDGE,"E9.1.45.0"),sQuery(id+"F0.wireOp",EDGE,"E9.3.45.0"),sQuery(id+"F0.wireOp",EDGE,"E9.7.45.0"),sQuery(id+"F0.wireOp",EDGE,"E9.11.45.0"),sQuery(id+"F0.wireOp",EDGE,"E9.14.45.0"),sQuery(id+"F0.wireOp",EDGE,"E9.1.46.0"),sQuery(id+"F0.wireOp",EDGE,"E9.3.46.0"),sQuery(id+"F0.wireOp",EDGE,"E9.7.46.0"),sQuery(id+"F0.wireOp",EDGE,"E9.11.46.0"),sQuery(id+"F0.wireOp",EDGE,"E9.14.46.0"),sQuery(id+"F0.wireOp",EDGE,"E9.1.47.0"),sQuery(id+"F0.wireOp",EDGE,"E9.3.47.0"),sQuery(id+"F0.wireOp",EDGE,"E9.7.47.0"),sQuery(id+"F0.wireOp",EDGE,"E9.11.47.0"),sQuery(id+"F0.wireOp",EDGE,"E9.14.47.0"),sQuery(id+"F0.wireOp",EDGE,"E9.1.48.0"),sQuery(id+"F0.wireOp",EDGE,"E9.3.48.0"),sQuery(id+"F0.wireOp",EDGE,"E9.7.48.0"),sQuery(id+"F0.wireOp",EDGE,"E9.11.48.0"),sQuery(id+"F0.wireOp",EDGE,"E9.14.48.0"),sQuery(id+"F0.wireOp",EDGE,"E9.1.49.0"),sQuery(id+"F0.wireOp",EDGE,"E9.3.49.0"),sQuery(id+"F0.wireOp",EDGE,"E9.7.49.0"),sQuery(id+"F0.wireOp",EDGE,"E9.11.49.0"),sQuery(id+"F0.wireOp",EDGE,"E9.14.49.0"),sQuery(id+"F0.wireOp",EDGE,"E9.1.50.0"),sQuery(id+"F0.wireOp",EDGE,"E9.3.50.0"),sQuery(id+"F0.wireOp",EDGE,"E9.7.50.0"),sQuery(id+"F0.wireOp",EDGE,"E9.11.50.0"),sQuery(id+"F0.wireOp",EDGE,"E9.14.50.0"),sQuery(id+"F0.wireOp",EDGE,"E9.1.51.0"),sQuery(id+"F0.wireOp",EDGE,"E9.3.51.0"),sQuery(id+"F0.wireOp",EDGE,"E9.7.51.0"),sQuery(id+"F0.wireOp",EDGE,"E9.11.51.0"),sQuery(id+"F0.wireOp",EDGE,"E9.14.51.0"),sQuery(id+"F0.wireOp",EDGE,"E9.1.52.0"),sQuery(id+"F0.wireOp",EDGE,"E9.3.52.0"),sQuery(id+"F0.wireOp",EDGE,"E9.7.52.0"),sQuery(id+"F0.wireOp",EDGE,"E9.11.52.0"),sQuery(id+"F0.wireOp",EDGE,"E9.14.52.0"),sQuery(id+"F0.wireOp",EDGE,"E9.1.53.0"),sQuery(id+"F0.wireOp",EDGE,"E9.3.53.0"),sQuery(id+"F0.wireOp",EDGE,"E9.7.53.0"),sQuery(id+"F0.wireOp",EDGE,"E9.11.53.0"),sQuery(id+"F0.wireOp",EDGE,"E9.14.53.0"),sQuery(id+"F0.wireOp",EDGE,"E9.1.54.0"),sQuery(id+"F0.wireOp",EDGE,"E9.3.54.0"),sQuery(id+"F0.wireOp",EDGE,"E9.7.54.0"),sQuery(id+"F0.wireOp",EDGE,"E9.11.54.0"),sQuery(id+"F0.wireOp",EDGE,"E9.14.54.0"),sQuery(id+"F0.wireOp",EDGE,"E9.1.55.0"),sQuery(id+"F0.wireOp",EDGE,"E9.3.55.0"),sQuery(id+"F0.wireOp",EDGE,"E9.7.55.0"),sQuery(id+"F0.wireOp",EDGE,"E9.11.55.0"),sQuery(id+"F0.wireOp",EDGE,"E9.14.55.0"),sQuery(id+"F0.wireOp",EDGE,"E9.1.56.0"),sQuery(id+"F0.wireOp",EDGE,"E9.3.56.0"),sQuery(id+"F0.wireOp",EDGE,"E9.7.56.0"),sQuery(id+"F0.wireOp",EDGE,"E9.11.56.0"),sQuery(id+"F0.wireOp",EDGE,"E9.14.56.0"),sQuery(id+"F0.wireOp",EDGE,"E9.1.57.0"),sQuery(id+"F0.wireOp",EDGE,"E9.3.57.0"),sQuery(id+"F0.wireOp",EDGE,"E9.7.57.0"),sQuery(id+"F0.wireOp",EDGE,"E9.11.57.0"),sQuery(id+"F0.wireOp",EDGE,"E9.14.57.0"),sQuery(id+"F0.wireOp",EDGE,"E9.1.58.0"),sQuery(id+"F0.wireOp",EDGE,"E9.3.58.0"),sQuery(id+"F0.wireOp",EDGE,"E9.7.58.0"),sQuery(id+"F0.wireOp",EDGE,"E9.11.58.0"),sQuery(id+"F0.wireOp",EDGE,"E9.14.58.0"),sQuery(id+"F0.wireOp",EDGE,"E9.1.59.0"),sQuery(id+"F0.wireOp",EDGE,"E9.3.59.0"),sQuery(id+"F0.wireOp",EDGE,"E9.7.59.0"),sQuery(id+"F0.wireOp",EDGE,"E9.11.59.0"),sQuery(id+"F0.wireOp",EDGE,"E9.14.59.0"),sQuery(id+"F2.wireOp",EDGE,"E37.trimOffspring")])],"isStart":false})});
            var Q5;
            Q5=makeQuery(id+"F6.boolean.opBoolean","INTERSECT",EDGE,{"derivedFrom":[makeQuery(id+"F4.boolean.opBoolean","COPY",FACE,{"derivedFrom":makeQuery(id+"F4.opExtrude","CAP_FACE",FACE,{"disambiguationData":[OSD([sQuery(id+"F3.wireOp",EDGE,"E42"),sQuery(id+"F3.wireOp",EDGE,"E43")])],"isStart":false})}),makeQuery(id+"F6.opExtrude","SWEPT_FACE",FACE,{"disambiguationData":[OSD([sQuery(id+"F2.wireOp",EDGE,"E20.0")])]})]});
            var Q6;
            Q6=makeQuery(id+"F6.boolean.opBoolean","INTERSECT",EDGE,{"derivedFrom":[makeQuery(id+"F4.boolean.opBoolean","COPY",FACE,{"derivedFrom":makeQuery(id+"F4.opExtrude","CAP_FACE",FACE,{"disambiguationData":[OSD([sQuery(id+"F3.wireOp",EDGE,"E42"),sQuery(id+"F3.wireOp",EDGE,"E43")])],"isStart":false})}),makeQuery(id+"F6.opExtrude","SWEPT_FACE",FACE,{"disambiguationData":[OSD([sQuery(id+"F2.wireOp",EDGE,"E19")])]})]});
            var Q7;
            Q7=makeQuery(id+"F6.boolean.opBoolean","INTERSECT",EDGE,{"derivedFrom":[makeQuery(id+"F4.boolean.opBoolean","COPY",FACE,{"derivedFrom":makeQuery(id+"F4.opExtrude","CAP_FACE",FACE,{"disambiguationData":[OSD([sQuery(id+"F3.wireOp",EDGE,"E42"),sQuery(id+"F3.wireOp",EDGE,"E43")])],"isStart":false})}),makeQuery(id+"F6.opExtrude","SWEPT_FACE",FACE,{"disambiguationData":[OSD([sQuery(id+"F2.wireOp",EDGE,"E22.0")])]})]});
            var Q8;
            Q8=makeQuery(id+"F6.boolean.opBoolean","INTERSECT",EDGE,{"derivedFrom":[makeQuery(id+"F4.boolean.opBoolean","COPY",FACE,{"derivedFrom":makeQuery(id+"F4.opExtrude","CAP_FACE",FACE,{"disambiguationData":[OSD([sQuery(id+"F3.wireOp",EDGE,"E42"),sQuery(id+"F3.wireOp",EDGE,"E43")])],"isStart":false})}),makeQuery(id+"F6.opExtrude","SWEPT_FACE",FACE,{"disambiguationData":[OSD([sQuery(id+"F2.wireOp",EDGE,"E36.trimOffspring")])]})]});
            fillet(context, id + "F9", {"entities" : qUnion([Q0, Q1, Q2, Q3, Q4, Q5, Q6, Q7, Q8]), "radius" : 1 * mm, "tangentPropagation" : true, "allowEdgeOverflow" : false});
        }
        {
            var Q0;
            Q0=makeQuery(id+"F4.boolean.opBoolean","COPY",EDGE,{"derivedFrom":makeQuery(id+"F4.opExtrude","CAP_EDGE",EDGE,{"disambiguationData":[OSD([sQuery(id+"F3.wireOp",EDGE,"E43")])],"isStart":false})});
            var Q1;
            Q1=makeQuery(id+"F8.boolean.opBoolean","COPY",EDGE,{"derivedFrom":makeQuery(id+"F8.opExtrude","CAP_EDGE",EDGE,{"disambiguationData":[OSD([sQuery(id+"F7.wireOp",EDGE,"E47")])],"isStart":false})});
            var Q2;
            Q2=makeQuery(id+"F4.boolean.opBoolean","COPY",EDGE,{"derivedFrom":makeQuery(id+"F4.opExtrude","CAP_EDGE",EDGE,{"disambiguationData":[OSD([sQuery(id+"F3.wireOp",EDGE,"E42")])],"isStart":false})});
            var Q3;
            Q3=makeQuery(id+"F8.boolean.opBoolean","COPY",EDGE,{"derivedFrom":makeQuery(id+"F8.opExtrude","CAP_EDGE",EDGE,{"disambiguationData":[OSD([sQuery(id+"F7.wireOp",EDGE,"E44")])],"isStart":false})});
            fillet(context, id + "F10", {"entities" : qUnion([Q0, Q1, Q2, Q3]), "radius" : 1 * mm, "tangentPropagation" : true, "allowEdgeOverflow" : false});
        }
    });
